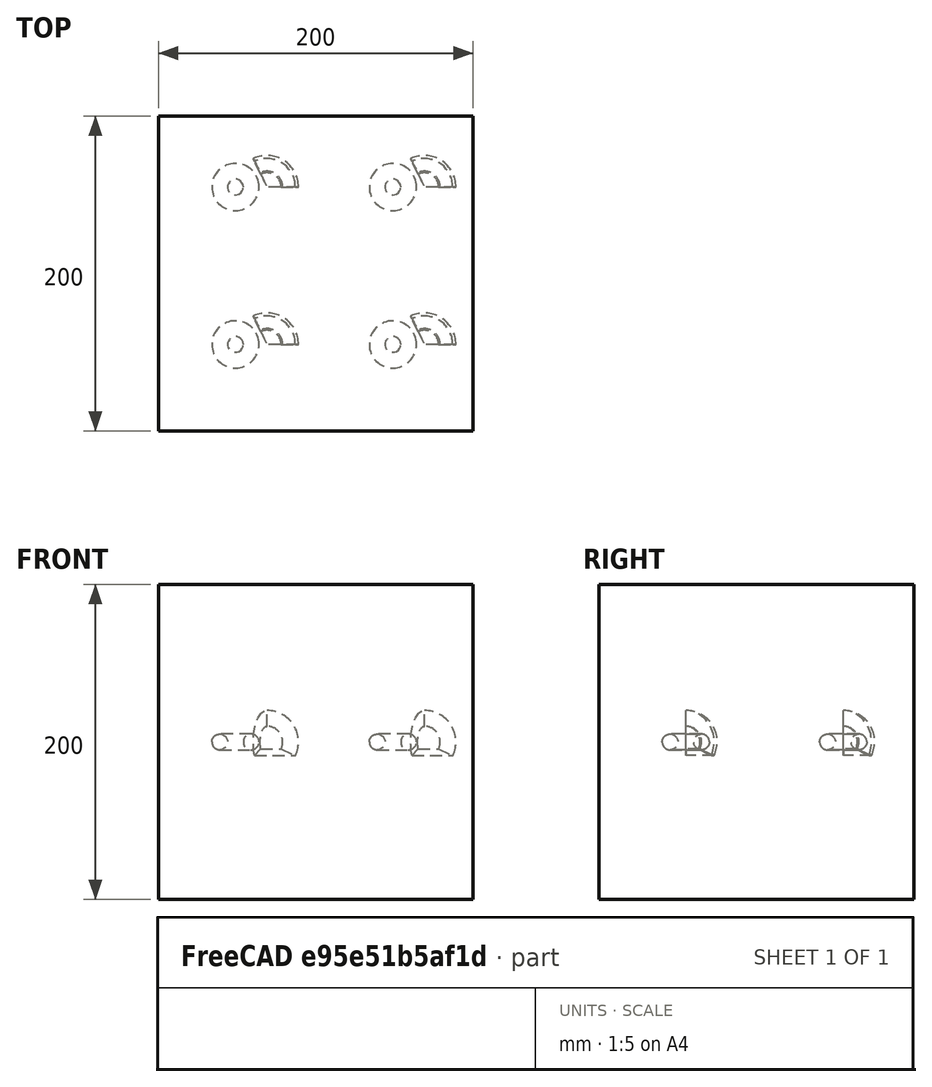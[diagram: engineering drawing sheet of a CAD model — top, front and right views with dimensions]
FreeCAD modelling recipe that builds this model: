
FCSTD DOCUMENT  (FreeCAD 0.19RUnknown)
Label: arrayTest-6
License: All rights reserved
LicenseURL: http://en.wikipedia.org/wiki/All_rights_reserved
objects: App::DocumentObjectGroupPython×1248, Part::FeaturePython×4, App::Part×2, Part::MultiFuse×1
note: 5 computed .brp shape members not serialized (recipe doc carries the construction recipe); baked Part::Feature solids carry a one-line shape summary decoded from their .brp

FEATURE [App::DocumentObjectGroupPython] HALFPI  # scripted group (container) (typed FeaturePython)
  name = HALFPI
  value = pi/2.
FEATURE [App::DocumentObjectGroupPython] PI  # scripted group (container) (typed FeaturePython)
  name = PI
  value = 1.*pi
FEATURE [App::DocumentObjectGroupPython] TWOPI  # scripted group (container) (typed FeaturePython)
  name = TWOPI
  value = 2.*pi
FEATURE [App::DocumentObjectGroupPython] Constants  # scripted group (container) (typed FeaturePython)
  Group = -> [HALFPI,PI,TWOPI]
FEATURE [App::DocumentObjectGroupPython] Variables  # scripted group (container) (typed FeaturePython)
FEATURE [App::DocumentObjectGroupPython] Quantities  # scripted group (container) (typed FeaturePython)
FEATURE [App::DocumentObjectGroupPython] Isotopes  # scripted group (container) (typed FeaturePython)
FEATURE [App::DocumentObjectGroupPython] Elements  # scripted group (container) (typed FeaturePython)
FEATURE [App::DocumentObjectGroupPython] G4Isotopes  # scripted group (container) (typed FeaturePython)
FEATURE [App::DocumentObjectGroupPython] H_element  # scripted group (container) (typed FeaturePython)
  Z = 1
  atom_value = 1.008
  formula = H
  name = H_element
FEATURE [App::DocumentObjectGroupPython] He_element  # scripted group (container) (typed FeaturePython)
  Z = 2
  atom_value = 4.0026
  formula = He
  name = He_element
FEATURE [App::DocumentObjectGroupPython] Li_element  # scripted group (container) (typed FeaturePython)
  Z = 3
  atom_value = 6.94
  formula = Li
  name = Li_element
FEATURE [App::DocumentObjectGroupPython] Be_element  # scripted group (container) (typed FeaturePython)
  Z = 4
  atom_value = 9.01218
  formula = Be
  name = Be_element
FEATURE [App::DocumentObjectGroupPython] B_element  # scripted group (container) (typed FeaturePython)
  Z = 5
  atom_value = 10.81
  formula = B
  name = B_element
FEATURE [App::DocumentObjectGroupPython] C_element  # scripted group (container) (typed FeaturePython)
  Z = 6
  atom_value = 12.011
  formula = C
  name = C_element
FEATURE [App::DocumentObjectGroupPython] N_element  # scripted group (container) (typed FeaturePython)
  Z = 7
  atom_value = 14.007
  formula = N
  name = N_element
FEATURE [App::DocumentObjectGroupPython] O_element  # scripted group (container) (typed FeaturePython)
  Z = 8
  atom_value = 15.999
  formula = O
  name = O_element
FEATURE [App::DocumentObjectGroupPython] F_element  # scripted group (container) (typed FeaturePython)
  Z = 9
  atom_value = 18.9984
  formula = F
  name = F_element
FEATURE [App::DocumentObjectGroupPython] Ne_element  # scripted group (container) (typed FeaturePython)
  Z = 10
  atom_value = 20.1797
  formula = Ne
  name = Ne_element
FEATURE [App::DocumentObjectGroupPython] Na_element  # scripted group (container) (typed FeaturePython)
  Z = 11
  atom_value = 22.9898
  formula = Na
  name = Na_element
FEATURE [App::DocumentObjectGroupPython] Mg_element  # scripted group (container) (typed FeaturePython)
  Z = 12
  atom_value = 24.305
  formula = Mg
  name = Mg_element
FEATURE [App::DocumentObjectGroupPython] Al_element  # scripted group (container) (typed FeaturePython)
  Z = 13
  atom_value = 26.9815
  formula = Al
  name = Al_element
FEATURE [App::DocumentObjectGroupPython] Si_element  # scripted group (container) (typed FeaturePython)
  Z = 14
  atom_value = 28.085
  formula = Si
  name = Si_element
FEATURE [App::DocumentObjectGroupPython] P_element  # scripted group (container) (typed FeaturePython)
  Z = 15
  atom_value = 30.9738
  formula = P
  name = P_element
FEATURE [App::DocumentObjectGroupPython] S_element  # scripted group (container) (typed FeaturePython)
  Z = 16
  atom_value = 32.06
  formula = S
  name = S_element
FEATURE [App::DocumentObjectGroupPython] Cl_element  # scripted group (container) (typed FeaturePython)
  Z = 17
  atom_value = 35.45
  formula = Cl
  name = Cl_element
FEATURE [App::DocumentObjectGroupPython] Ar_element  # scripted group (container) (typed FeaturePython)
  Z = 18
  atom_value = 39.95
  formula = Ar
  name = Ar_element
FEATURE [App::DocumentObjectGroupPython] K_element  # scripted group (container) (typed FeaturePython)
  Z = 19
  atom_value = 39.0983
  formula = K
  name = K_element
FEATURE [App::DocumentObjectGroupPython] Ca_element  # scripted group (container) (typed FeaturePython)
  Z = 20
  atom_value = 40.078
  formula = Ca
  name = Ca_element
FEATURE [App::DocumentObjectGroupPython] Sc_element  # scripted group (container) (typed FeaturePython)
  Z = 21
  atom_value = 44.9559
  formula = Sc
  name = Sc_element
FEATURE [App::DocumentObjectGroupPython] Ti_element  # scripted group (container) (typed FeaturePython)
  Z = 22
  atom_value = 47.867
  formula = Ti
  name = Ti_element
FEATURE [App::DocumentObjectGroupPython] V_element  # scripted group (container) (typed FeaturePython)
  Z = 23
  atom_value = 50.9415
  formula = V
  name = V_element
FEATURE [App::DocumentObjectGroupPython] Cr_element  # scripted group (container) (typed FeaturePython)
  Z = 24
  atom_value = 51.9961
  formula = Cr
  name = Cr_element
FEATURE [App::DocumentObjectGroupPython] Mn_element  # scripted group (container) (typed FeaturePython)
  Z = 25
  atom_value = 54.938
  formula = Mn
  name = Mn_element
FEATURE [App::DocumentObjectGroupPython] Fe_element  # scripted group (container) (typed FeaturePython)
  Z = 26
  atom_value = 55.845
  formula = Fe
  name = Fe_element
FEATURE [App::DocumentObjectGroupPython] Co_element  # scripted group (container) (typed FeaturePython)
  Z = 27
  atom_value = 58.9332
  formula = Co
  name = Co_element
FEATURE [App::DocumentObjectGroupPython] Ni_element  # scripted group (container) (typed FeaturePython)
  Z = 28
  atom_value = 58.6934
  formula = Ni
  name = Ni_element
FEATURE [App::DocumentObjectGroupPython] Cu_element  # scripted group (container) (typed FeaturePython)
  Z = 29
  atom_value = 63.546
  formula = Cu
  name = Cu_element
FEATURE [App::DocumentObjectGroupPython] Zn_element  # scripted group (container) (typed FeaturePython)
  Z = 30
  atom_value = 65.38
  formula = Zn
  name = Zn_element
FEATURE [App::DocumentObjectGroupPython] Ga_element  # scripted group (container) (typed FeaturePython)
  Z = 31
  atom_value = 69.723
  formula = Ga
  name = Ga_element
FEATURE [App::DocumentObjectGroupPython] Ge_element  # scripted group (container) (typed FeaturePython)
  Z = 32
  atom_value = 72.63
  formula = Ge
  name = Ge_element
FEATURE [App::DocumentObjectGroupPython] As_element  # scripted group (container) (typed FeaturePython)
  Z = 33
  atom_value = 74.9216
  formula = As
  name = As_element
FEATURE [App::DocumentObjectGroupPython] Se_element  # scripted group (container) (typed FeaturePython)
  Z = 34
  atom_value = 78.971
  formula = Se
  name = Se_element
FEATURE [App::DocumentObjectGroupPython] Br_element  # scripted group (container) (typed FeaturePython)
  Z = 35
  atom_value = 79.904
  formula = Br
  name = Br_element
FEATURE [App::DocumentObjectGroupPython] Kr_element  # scripted group (container) (typed FeaturePython)
  Z = 36
  atom_value = 83.798
  formula = Kr
  name = Kr_element
FEATURE [App::DocumentObjectGroupPython] Rb_element  # scripted group (container) (typed FeaturePython)
  Z = 37
  atom_value = 85.4678
  formula = Rb
  name = Rb_element
FEATURE [App::DocumentObjectGroupPython] Sr_element  # scripted group (container) (typed FeaturePython)
  Z = 38
  atom_value = 87.62
  formula = Sr
  name = Sr_element
FEATURE [App::DocumentObjectGroupPython] Y_element  # scripted group (container) (typed FeaturePython)
  Z = 39
  atom_value = 88.9058
  formula = Y
  name = Y_element
FEATURE [App::DocumentObjectGroupPython] Zr_element  # scripted group (container) (typed FeaturePython)
  Z = 40
  atom_value = 91.224
  formula = Zr
  name = Zr_element
FEATURE [App::DocumentObjectGroupPython] Nb_element  # scripted group (container) (typed FeaturePython)
  Z = 41
  atom_value = 92.9064
  formula = Nb
  name = Nb_element
FEATURE [App::DocumentObjectGroupPython] Mo_element  # scripted group (container) (typed FeaturePython)
  Z = 42
  atom_value = 95.95
  formula = Mo
  name = Mo_element
FEATURE [App::DocumentObjectGroupPython] Tc_element  # scripted group (container) (typed FeaturePython)
  Z = 43
  atom_value = 97
  formula = Tc
  name = Tc_element
FEATURE [App::DocumentObjectGroupPython] Ru_element  # scripted group (container) (typed FeaturePython)
  Z = 44
  atom_value = 101.07
  formula = Ru
  name = Ru_element
FEATURE [App::DocumentObjectGroupPython] Rh_element  # scripted group (container) (typed FeaturePython)
  Z = 45
  atom_value = 102.905
  formula = Rh
  name = Rh_element
FEATURE [App::DocumentObjectGroupPython] Pd_element  # scripted group (container) (typed FeaturePython)
  Z = 46
  atom_value = 106.42
  formula = Pd
  name = Pd_element
FEATURE [App::DocumentObjectGroupPython] Ag_element  # scripted group (container) (typed FeaturePython)
  Z = 47
  atom_value = 107.868
  formula = Ag
  name = Ag_element
FEATURE [App::DocumentObjectGroupPython] Cd_element  # scripted group (container) (typed FeaturePython)
  Z = 48
  atom_value = 112.414
  formula = Cd
  name = Cd_element
FEATURE [App::DocumentObjectGroupPython] In_element  # scripted group (container) (typed FeaturePython)
  Z = 49
  atom_value = 114.818
  formula = In
  name = In_element
FEATURE [App::DocumentObjectGroupPython] Sn_element  # scripted group (container) (typed FeaturePython)
  Z = 50
  atom_value = 118.71
  formula = Sn
  name = Sn_element
FEATURE [App::DocumentObjectGroupPython] Sb_element  # scripted group (container) (typed FeaturePython)
  Z = 51
  atom_value = 121.76
  formula = Sb
  name = Sb_element
FEATURE [App::DocumentObjectGroupPython] Te_element  # scripted group (container) (typed FeaturePython)
  Z = 52
  atom_value = 127.6
  formula = Te
  name = Te_element
FEATURE [App::DocumentObjectGroupPython] I_element  # scripted group (container) (typed FeaturePython)
  Z = 53
  atom_value = 126.904
  formula = I
  name = I_element
FEATURE [App::DocumentObjectGroupPython] Xe_element  # scripted group (container) (typed FeaturePython)
  Z = 54
  atom_value = 131.293
  formula = Xe
  name = Xe_element
FEATURE [App::DocumentObjectGroupPython] Cs_element  # scripted group (container) (typed FeaturePython)
  Z = 55
  atom_value = 132.905
  formula = Cs
  name = Cs_element
FEATURE [App::DocumentObjectGroupPython] Ba_element  # scripted group (container) (typed FeaturePython)
  Z = 56
  atom_value = 137.327
  formula = Ba
  name = Ba_element
FEATURE [App::DocumentObjectGroupPython] La_element  # scripted group (container) (typed FeaturePython)
  Z = 57
  atom_value = 138.905
  formula = La
  name = La_element
FEATURE [App::DocumentObjectGroupPython] Ce_element  # scripted group (container) (typed FeaturePython)
  Z = 58
  atom_value = 140.116
  formula = Ce
  name = Ce_element
FEATURE [App::DocumentObjectGroupPython] Pr_element  # scripted group (container) (typed FeaturePython)
  Z = 59
  atom_value = 140.908
  formula = Pr
  name = Pr_element
FEATURE [App::DocumentObjectGroupPython] Nd_element  # scripted group (container) (typed FeaturePython)
  Z = 60
  atom_value = 144.242
  formula = Nd
  name = Nd_element
FEATURE [App::DocumentObjectGroupPython] Pm_element  # scripted group (container) (typed FeaturePython)
  Z = 61
  atom_value = 145
  formula = Pm
  name = Pm_element
FEATURE [App::DocumentObjectGroupPython] Sm_element  # scripted group (container) (typed FeaturePython)
  Z = 62
  atom_value = 150.36
  formula = Sm
  name = Sm_element
FEATURE [App::DocumentObjectGroupPython] Eu_element  # scripted group (container) (typed FeaturePython)
  Z = 63
  atom_value = 151.964
  formula = Eu
  name = Eu_element
FEATURE [App::DocumentObjectGroupPython] Gd_element  # scripted group (container) (typed FeaturePython)
  Z = 64
  atom_value = 157.25
  formula = Gd
  name = Gd_element
FEATURE [App::DocumentObjectGroupPython] Tb_element  # scripted group (container) (typed FeaturePython)
  Z = 65
  atom_value = 158.925
  formula = Tb
  name = Tb_element
FEATURE [App::DocumentObjectGroupPython] Dy_element  # scripted group (container) (typed FeaturePython)
  Z = 66
  atom_value = 162.5
  formula = Dy
  name = Dy_element
FEATURE [App::DocumentObjectGroupPython] Ho_element  # scripted group (container) (typed FeaturePython)
  Z = 67
  atom_value = 164.93
  formula = Ho
  name = Ho_element
FEATURE [App::DocumentObjectGroupPython] Er_element  # scripted group (container) (typed FeaturePython)
  Z = 68
  atom_value = 167.259
  formula = Er
  name = Er_element
FEATURE [App::DocumentObjectGroupPython] Tm_element  # scripted group (container) (typed FeaturePython)
  Z = 69
  atom_value = 168.934
  formula = Tm
  name = Tm_element
FEATURE [App::DocumentObjectGroupPython] Yb_element  # scripted group (container) (typed FeaturePython)
  Z = 70
  atom_value = 173.045
  formula = Yb
  name = Yb_element
FEATURE [App::DocumentObjectGroupPython] Lu_element  # scripted group (container) (typed FeaturePython)
  Z = 71
  atom_value = 174.967
  formula = Lu
  name = Lu_element
FEATURE [App::DocumentObjectGroupPython] Hf_element  # scripted group (container) (typed FeaturePython)
  Z = 72
  atom_value = 178.49
  formula = Hf
  name = Hf_element
FEATURE [App::DocumentObjectGroupPython] Ta_element  # scripted group (container) (typed FeaturePython)
  Z = 73
  atom_value = 180.948
  formula = Ta
  name = Ta_element
FEATURE [App::DocumentObjectGroupPython] W_element  # scripted group (container) (typed FeaturePython)
  Z = 74
  atom_value = 183.84
  formula = W
  name = W_element
FEATURE [App::DocumentObjectGroupPython] Re_element  # scripted group (container) (typed FeaturePython)
  Z = 75
  atom_value = 186.207
  formula = Re
  name = Re_element
FEATURE [App::DocumentObjectGroupPython] Os_element  # scripted group (container) (typed FeaturePython)
  Z = 76
  atom_value = 190.23
  formula = Os
  name = Os_element
FEATURE [App::DocumentObjectGroupPython] Ir_element  # scripted group (container) (typed FeaturePython)
  Z = 77
  atom_value = 192.217
  formula = Ir
  name = Ir_element
FEATURE [App::DocumentObjectGroupPython] Pt_element  # scripted group (container) (typed FeaturePython)
  Z = 78
  atom_value = 195.084
  formula = Pt
  name = Pt_element
FEATURE [App::DocumentObjectGroupPython] Au_element  # scripted group (container) (typed FeaturePython)
  Z = 79
  atom_value = 196.967
  formula = Au
  name = Au_element
FEATURE [App::DocumentObjectGroupPython] Hg_element  # scripted group (container) (typed FeaturePython)
  Z = 80
  atom_value = 200.592
  formula = Hg
  name = Hg_element
FEATURE [App::DocumentObjectGroupPython] Tl_element  # scripted group (container) (typed FeaturePython)
  Z = 81
  atom_value = 204.38
  formula = Tl
  name = Tl_element
FEATURE [App::DocumentObjectGroupPython] Pb_element  # scripted group (container) (typed FeaturePython)
  Z = 82
  atom_value = 207.2
  formula = Pb
  name = Pb_element
FEATURE [App::DocumentObjectGroupPython] Bi_element  # scripted group (container) (typed FeaturePython)
  Z = 83
  atom_value = 208.98
  formula = Bi
  name = Bi_element
FEATURE [App::DocumentObjectGroupPython] Po_element  # scripted group (container) (typed FeaturePython)
  Z = 84
  atom_value = 209
  formula = Po
  name = Po_element
FEATURE [App::DocumentObjectGroupPython] At_element  # scripted group (container) (typed FeaturePython)
  Z = 85
  atom_value = 210
  formula = At
  name = At_element
FEATURE [App::DocumentObjectGroupPython] Rn_element  # scripted group (container) (typed FeaturePython)
  Z = 86
  atom_value = 222
  formula = Rn
  name = Rn_element
FEATURE [App::DocumentObjectGroupPython] Fr_element  # scripted group (container) (typed FeaturePython)
  Z = 87
  atom_value = 223
  formula = Fr
  name = Fr_element
FEATURE [App::DocumentObjectGroupPython] Ra_element  # scripted group (container) (typed FeaturePython)
  Z = 88
  atom_value = 226
  formula = Ra
  name = Ra_element
FEATURE [App::DocumentObjectGroupPython] Ac_element  # scripted group (container) (typed FeaturePython)
  Z = 89
  atom_value = 227
  formula = Ac
  name = Ac_element
FEATURE [App::DocumentObjectGroupPython] Th_element  # scripted group (container) (typed FeaturePython)
  Z = 90
  atom_value = 232.038
  formula = Th
  name = Th_element
FEATURE [App::DocumentObjectGroupPython] Pa_element  # scripted group (container) (typed FeaturePython)
  Z = 91
  atom_value = 231.036
  formula = Pa
  name = Pa_element
FEATURE [App::DocumentObjectGroupPython] U_element  # scripted group (container) (typed FeaturePython)
  Z = 92
  atom_value = 238.029
  formula = U
  name = U_element
FEATURE [App::DocumentObjectGroupPython] Np_element  # scripted group (container) (typed FeaturePython)
  Z = 93
  atom_value = 237
  formula = Np
  name = Np_element
FEATURE [App::DocumentObjectGroupPython] Pu_element  # scripted group (container) (typed FeaturePython)
  Z = 94
  atom_value = 244
  formula = Pu
  name = Pu_element
FEATURE [App::DocumentObjectGroupPython] Am_element  # scripted group (container) (typed FeaturePython)
  Z = 95
  atom_value = 243
  formula = Am
  name = Am_element
FEATURE [App::DocumentObjectGroupPython] Cm_element  # scripted group (container) (typed FeaturePython)
  Z = 96
  atom_value = 247
  formula = Cm
  name = Cm_element
FEATURE [App::DocumentObjectGroupPython] Bk_element  # scripted group (container) (typed FeaturePython)
  Z = 97
  atom_value = 247
  formula = Bk
  name = Bk_element
FEATURE [App::DocumentObjectGroupPython] Cf_element  # scripted group (container) (typed FeaturePython)
  Z = 98
  atom_value = 251
  formula = Cf
  name = Cf_element
FEATURE [App::DocumentObjectGroupPython] G4Elements  # scripted group (container) (typed FeaturePython)
  Group = -> [H_element,He_element,Li_element,Be_element,B_element,C_element,N_element,O_element,F_element,Ne_element,Na_element,Mg_element,Al_element,Si_element,P_element,S_element,Cl_element,Ar_element,K_element,Ca_element,Sc_element,Ti_element,V_element,Cr_element,Mn_element,Fe_element,Co_element,Ni_element,Cu_element,Zn_element,Ga_element,Ge_element,As_element,Se_element,Br_element,Kr_element,Rb_element,+61 more]
FEATURE [App::DocumentObjectGroupPython] H_element001  label="H_element : 0.101"  # scripted group (container) (typed FeaturePython)
  n = 0.101327
FEATURE [App::DocumentObjectGroupPython] C_element001  label="C_element : 0.775"  # scripted group (container) (typed FeaturePython)
  n = 0.7755
FEATURE [App::DocumentObjectGroupPython] N_element001  label="N_element : 0.035"  # scripted group (container) (typed FeaturePython)
  n = 0.035057
FEATURE [App::DocumentObjectGroupPython] O_element001  label="O_element : 0.052"  # scripted group (container) (typed FeaturePython)
  n = 0.0523159
FEATURE [App::DocumentObjectGroupPython] F_element001  label="F_element : 0.017"  # scripted group (container) (typed FeaturePython)
  n = 0.017422
FEATURE [App::DocumentObjectGroupPython] Ca_element001  label="Ca_element : 0.018"  # scripted group (container) (typed FeaturePython)
  n = 0.018378
FEATURE [App::DocumentObjectGroupPython] G4_A_150_TISSUE  label="G4_A-150_TISSUE"  # scripted group (container) (typed FeaturePython)
  Dunit = g/cm3
  Dvalue = 1.127
  Group = -> [H_element001,C_element001,N_element001,O_element001,F_element001,Ca_element001]
  conduct = 2
  density = 1
  expand = 3
  formula = G4_A-150_TISSUE
  name = G4_A-150_TISSUE
  specific = 4
FEATURE [App::DocumentObjectGroupPython] C_element002  label="C_element : 3"  # scripted group (container) (typed FeaturePython)
  n = 3
  ref = C_element
FEATURE [App::DocumentObjectGroupPython] H_element002  label="H_element : 6"  # scripted group (container) (typed FeaturePython)
  n = 6
  ref = H_element
FEATURE [App::DocumentObjectGroupPython] O_element002  label="O_element : 1"  # scripted group (container) (typed FeaturePython)
  n = 1
  ref = O_element
FEATURE [App::DocumentObjectGroupPython] G4_ACETONE  # scripted group (container) (typed FeaturePython)
  Dunit = g/cm3
  Dvalue = 0.7899
  Group = -> [C_element002,H_element002,O_element002]
  conduct = 2
  density = 1
  expand = 3
  formula = G4_ACETONE
  name = G4_ACETONE
  specific = 4
FEATURE [App::DocumentObjectGroupPython] C_element003  label="C_element : 2"  # scripted group (container) (typed FeaturePython)
  n = 2
  ref = C_element
FEATURE [App::DocumentObjectGroupPython] H_element003  label="H_element : 2"  # scripted group (container) (typed FeaturePython)
  n = 2
  ref = H_element
FEATURE [App::DocumentObjectGroupPython] G4_ACETYLENE  # scripted group (container) (typed FeaturePython)
  Dunit = g/cm3
  Dvalue = 0.0010967
  Group = -> [C_element003,H_element003]
  conduct = 2
  density = 1
  expand = 3
  formula = G4_ACETYLENE
  name = G4_ACETYLENE
  specific = 4
FEATURE [App::DocumentObjectGroupPython] C_element004  label="C_element : 5"  # scripted group (container) (typed FeaturePython)
  n = 5
  ref = C_element
FEATURE [App::DocumentObjectGroupPython] H_element004  label="H_element : 5"  # scripted group (container) (typed FeaturePython)
  n = 5
  ref = H_element
FEATURE [App::DocumentObjectGroupPython] N_element002  label="N_element : 5"  # scripted group (container) (typed FeaturePython)
  n = 5
  ref = N_element
FEATURE [App::DocumentObjectGroupPython] G4_ADENINE  # scripted group (container) (typed FeaturePython)
  Dunit = g/cm3
  Dvalue = 1.6
  Group = -> [C_element004,H_element004,N_element002]
  conduct = 2
  density = 1
  expand = 3
  formula = G4_ADENINE
  name = G4_ADENINE
  specific = 4
FEATURE [App::DocumentObjectGroupPython] H_element005  label="H_element : 0.114"  # scripted group (container) (typed FeaturePython)
  n = 0.114
FEATURE [App::DocumentObjectGroupPython] C_element005  label="C_element : 0.598"  # scripted group (container) (typed FeaturePython)
  n = 0.598
FEATURE [App::DocumentObjectGroupPython] N_element003  label="N_element : 0.007"  # scripted group (container) (typed FeaturePython)
  n = 0.007
FEATURE [App::DocumentObjectGroupPython] O_element003  label="O_element : 0.278"  # scripted group (container) (typed FeaturePython)
  n = 0.278
FEATURE [App::DocumentObjectGroupPython] Na_element001  label="Na_element : 0.001"  # scripted group (container) (typed FeaturePython)
  n = 0.001
FEATURE [App::DocumentObjectGroupPython] S_element001  label="S_element : 0.001"  # scripted group (container) (typed FeaturePython)
  n = 0.001
FEATURE [App::DocumentObjectGroupPython] Cl_element001  label="Cl_element : 0.001"  # scripted group (container) (typed FeaturePython)
  n = 0.001
FEATURE [App::DocumentObjectGroupPython] G4_ADIPOSE_TISSUE_ICRP  # scripted group (container) (typed FeaturePython)
  Dunit = g/cm3
  Dvalue = 0.95
  Group = -> [H_element005,C_element005,N_element003,O_element003,Na_element001,S_element001,Cl_element001]
  conduct = 2
  density = 1
  expand = 3
  formula = G4_ADIPOSE_TISSUE_ICRP
  name = G4_ADIPOSE_TISSUE_ICRP
  specific = 4
FEATURE [App::DocumentObjectGroupPython] C_element006  label="C_element : 0.000"  # scripted group (container) (typed FeaturePython)
  n = 0.000124
FEATURE [App::DocumentObjectGroupPython] N_element004  label="N_element : 0.755"  # scripted group (container) (typed FeaturePython)
  n = 0.755268
FEATURE [App::DocumentObjectGroupPython] O_element004  label="O_element : 0.232"  # scripted group (container) (typed FeaturePython)
  n = 0.231781
FEATURE [App::DocumentObjectGroupPython] Ar_element001  label="Ar_element : 0.013"  # scripted group (container) (typed FeaturePython)
  n = 0.012827
FEATURE [App::DocumentObjectGroupPython] G4_AIR  # scripted group (container) (typed FeaturePython)
  Dunit = g/cm3
  Dvalue = 0.00120479
  Group = -> [C_element006,N_element004,O_element004,Ar_element001]
  conduct = 2
  density = 1
  expand = 3
  formula = G4_AIR
  name = G4_AIR
  specific = 4
FEATURE [App::DocumentObjectGroupPython] C_element007  label="C_element : 006"  # scripted group (container) (typed FeaturePython)
  n = 3
  ref = C_element
FEATURE [App::DocumentObjectGroupPython] H_element006  label="H_element : 7"  # scripted group (container) (typed FeaturePython)
  n = 7
  ref = H_element
FEATURE [App::DocumentObjectGroupPython] N_element005  label="N_element : 1"  # scripted group (container) (typed FeaturePython)
  n = 1
  ref = N_element
FEATURE [App::DocumentObjectGroupPython] O_element005  label="O_element : 2"  # scripted group (container) (typed FeaturePython)
  n = 2
  ref = O_element
FEATURE [App::DocumentObjectGroupPython] G4_ALANINE  # scripted group (container) (typed FeaturePython)
  Dunit = g/cm3
  Dvalue = 1.42
  Group = -> [C_element007,H_element006,N_element005,O_element005]
  conduct = 2
  density = 1
  expand = 3
  formula = G4_ALANINE
  name = G4_ALANINE
  specific = 4
FEATURE [App::DocumentObjectGroupPython] Al_element001  label="Al_element : 2"  # scripted group (container) (typed FeaturePython)
  n = 2
  ref = Al_element
FEATURE [App::DocumentObjectGroupPython] O_element006  label="O_element : 3"  # scripted group (container) (typed FeaturePython)
  n = 3
  ref = O_element
FEATURE [App::DocumentObjectGroupPython] G4_ALUMINUM_OXIDE  # scripted group (container) (typed FeaturePython)
  Dunit = g/cm3
  Dvalue = 3.97
  Group = -> [Al_element001,O_element006]
  conduct = 2
  density = 1
  expand = 3
  formula = G4_ALUMINUM_OXIDE
  name = G4_ALUMINUM_OXIDE
  specific = 4
FEATURE [App::DocumentObjectGroupPython] H_element007  label="H_element : 0.106"  # scripted group (container) (typed FeaturePython)
  n = 0.10593
FEATURE [App::DocumentObjectGroupPython] C_element008  label="C_element : 0.789"  # scripted group (container) (typed FeaturePython)
  n = 0.788974
FEATURE [App::DocumentObjectGroupPython] O_element007  label="O_element : 0.105"  # scripted group (container) (typed FeaturePython)
  n = 0.105096
FEATURE [App::DocumentObjectGroupPython] G4_AMBER  # scripted group (container) (typed FeaturePython)
  Dunit = g/cm3
  Dvalue = 1.1
  Group = -> [H_element007,C_element008,O_element007]
  conduct = 2
  density = 1
  expand = 3
  formula = G4_AMBER
  name = G4_AMBER
  specific = 4
FEATURE [App::DocumentObjectGroupPython] N_element006  label="N_element : 006"  # scripted group (container) (typed FeaturePython)
  n = 1
  ref = N_element
FEATURE [App::DocumentObjectGroupPython] H_element008  label="H_element : 3"  # scripted group (container) (typed FeaturePython)
  n = 3
  ref = H_element
FEATURE [App::DocumentObjectGroupPython] G4_AMMONIA  # scripted group (container) (typed FeaturePython)
  Dunit = g/cm3
  Dvalue = 0.000826019
  Group = -> [N_element006,H_element008]
  conduct = 2
  density = 1
  expand = 3
  formula = G4_AMMONIA
  name = G4_AMMONIA
  specific = 4
FEATURE [App::DocumentObjectGroupPython] C_element009  label="C_element : 6"  # scripted group (container) (typed FeaturePython)
  n = 6
  ref = C_element
FEATURE [App::DocumentObjectGroupPython] H_element009  label="H_element : 008"  # scripted group (container) (typed FeaturePython)
  n = 7
  ref = H_element
FEATURE [App::DocumentObjectGroupPython] N_element007  label="N_element : 007"  # scripted group (container) (typed FeaturePython)
  n = 1
  ref = N_element
FEATURE [App::DocumentObjectGroupPython] G4_ANILINE  # scripted group (container) (typed FeaturePython)
  Dunit = g/cm3
  Dvalue = 1.0235
  Group = -> [C_element009,H_element009,N_element007]
  conduct = 2
  density = 1
  expand = 3
  formula = G4_ANILINE
  name = G4_ANILINE
  specific = 4
FEATURE [App::DocumentObjectGroupPython] C_element010  label="C_element : 14"  # scripted group (container) (typed FeaturePython)
  n = 14
  ref = C_element
FEATURE [App::DocumentObjectGroupPython] H_element010  label="H_element : 10"  # scripted group (container) (typed FeaturePython)
  n = 10
  ref = H_element
FEATURE [App::DocumentObjectGroupPython] G4_ANTHRACENE  # scripted group (container) (typed FeaturePython)
  Dunit = g/cm3
  Dvalue = 1.283
  Group = -> [C_element010,H_element010]
  conduct = 2
  density = 1
  expand = 3
  formula = G4_ANTHRACENE
  name = G4_ANTHRACENE
  specific = 4
FEATURE [App::DocumentObjectGroupPython] H_element011  label="H_element : 0.065"  # scripted group (container) (typed FeaturePython)
  n = 0.0654709
FEATURE [App::DocumentObjectGroupPython] C_element011  label="C_element : 0.537"  # scripted group (container) (typed FeaturePython)
  n = 0.536944
FEATURE [App::DocumentObjectGroupPython] N_element008  label="N_element : 0.021"  # scripted group (container) (typed FeaturePython)
  n = 0.0215
FEATURE [App::DocumentObjectGroupPython] O_element008  label="O_element : 0.032"  # scripted group (container) (typed FeaturePython)
  n = 0.032085
FEATURE [App::DocumentObjectGroupPython] F_element002  label="F_element : 0.167"  # scripted group (container) (typed FeaturePython)
  n = 0.167411
FEATURE [App::DocumentObjectGroupPython] Ca_element002  label="Ca_element : 0.177"  # scripted group (container) (typed FeaturePython)
  n = 0.176589
FEATURE [App::DocumentObjectGroupPython] G4_B_100_BONE  label="G4_B-100_BONE"  # scripted group (container) (typed FeaturePython)
  Dunit = g/cm3
  Dvalue = 1.45
  Group = -> [H_element011,C_element011,N_element008,O_element008,F_element002,Ca_element002]
  conduct = 2
  density = 1
  expand = 3
  formula = G4_B-100_BONE
  name = G4_B-100_BONE
  specific = 4
FEATURE [App::DocumentObjectGroupPython] H_element012  label="H_element : 0.057"  # scripted group (container) (typed FeaturePython)
  n = 0.057441
FEATURE [App::DocumentObjectGroupPython] C_element012  label="C_element : 0.790"  # scripted group (container) (typed FeaturePython)
  n = 0.774591
FEATURE [App::DocumentObjectGroupPython] O_element009  label="O_element : 0.168"  # scripted group (container) (typed FeaturePython)
  n = 0.167968
FEATURE [App::DocumentObjectGroupPython] G4_BAKELITE  # scripted group (container) (typed FeaturePython)
  Dunit = g/cm3
  Dvalue = 1.25
  Group = -> [H_element012,C_element012,O_element009]
  conduct = 2
  density = 1
  expand = 3
  formula = G4_BAKELITE
  name = G4_BAKELITE
  specific = 4
FEATURE [App::DocumentObjectGroupPython] Ba_element001  label="Ba_element : 1"  # scripted group (container) (typed FeaturePython)
  n = 1
  ref = Ba_element
FEATURE [App::DocumentObjectGroupPython] F_element003  label="F_element : 2"  # scripted group (container) (typed FeaturePython)
  n = 2
  ref = F_element
FEATURE [App::DocumentObjectGroupPython] G4_BARIUM_FLUORIDE  # scripted group (container) (typed FeaturePython)
  Dunit = g/cm3
  Dvalue = 4.89
  Group = -> [Ba_element001,F_element003]
  conduct = 2
  density = 1
  expand = 3
  formula = G4_BARIUM_FLUORIDE
  name = G4_BARIUM_FLUORIDE
  specific = 4
FEATURE [App::DocumentObjectGroupPython] Ba_element002  label="Ba_element : 002"  # scripted group (container) (typed FeaturePython)
  n = 1
  ref = Ba_element
FEATURE [App::DocumentObjectGroupPython] S_element002  label="S_element : 1"  # scripted group (container) (typed FeaturePython)
  n = 1
  ref = S_element
FEATURE [App::DocumentObjectGroupPython] O_element010  label="O_element : 4"  # scripted group (container) (typed FeaturePython)
  n = 4
  ref = O_element
FEATURE [App::DocumentObjectGroupPython] G4_BARIUM_SULFATE  # scripted group (container) (typed FeaturePython)
  Dunit = g/cm3
  Dvalue = 4.5
  Group = -> [Ba_element002,S_element002,O_element010]
  conduct = 2
  density = 1
  expand = 3
  formula = G4_BARIUM_SULFATE
  name = G4_BARIUM_SULFATE
  specific = 4
FEATURE [App::DocumentObjectGroupPython] C_element013  label="C_element : 007"  # scripted group (container) (typed FeaturePython)
  n = 6
  ref = C_element
FEATURE [App::DocumentObjectGroupPython] H_element013  label="H_element : 009"  # scripted group (container) (typed FeaturePython)
  n = 6
  ref = H_element
FEATURE [App::DocumentObjectGroupPython] G4_BENZENE  # scripted group (container) (typed FeaturePython)
  Dunit = g/cm3
  Dvalue = 0.87865
  Group = -> [C_element013,H_element013]
  conduct = 2
  density = 1
  expand = 3
  formula = G4_BENZENE
  name = G4_BENZENE
  specific = 4
FEATURE [App::DocumentObjectGroupPython] Be_element001  label="Be_element : 1"  # scripted group (container) (typed FeaturePython)
  n = 1
  ref = Be_element
FEATURE [App::DocumentObjectGroupPython] O_element011  label="O_element : 005"  # scripted group (container) (typed FeaturePython)
  n = 1
  ref = O_element
FEATURE [App::DocumentObjectGroupPython] G4_BERYLLIUM_OXIDE  # scripted group (container) (typed FeaturePython)
  Dunit = g/cm3
  Dvalue = 3.01
  Group = -> [Be_element001,O_element011]
  conduct = 2
  density = 1
  expand = 3
  formula = G4_BERYLLIUM_OXIDE
  name = G4_BERYLLIUM_OXIDE
  specific = 4
FEATURE [App::DocumentObjectGroupPython] Bi_element001  label="Bi_element : 4"  # scripted group (container) (typed FeaturePython)
  n = 4
  ref = Bi_element
FEATURE [App::DocumentObjectGroupPython] Ge_element001  label="Ge_element : 3"  # scripted group (container) (typed FeaturePython)
  n = 3
  ref = Ge_element
FEATURE [App::DocumentObjectGroupPython] O_element012  label="O_element : 12"  # scripted group (container) (typed FeaturePython)
  n = 12
  ref = O_element
FEATURE [App::DocumentObjectGroupPython] G4_BGO  # scripted group (container) (typed FeaturePython)
  Dunit = g/cm3
  Dvalue = 7.13
  Group = -> [Bi_element001,Ge_element001,O_element012]
  conduct = 2
  density = 1
  expand = 3
  formula = G4_BGO
  name = G4_BGO
  specific = 4
FEATURE [App::DocumentObjectGroupPython] H_element014  label="H_element : 0.102"  # scripted group (container) (typed FeaturePython)
  n = 0.102
FEATURE [App::DocumentObjectGroupPython] C_element014  label="C_element : 0.110"  # scripted group (container) (typed FeaturePython)
  n = 0.11
FEATURE [App::DocumentObjectGroupPython] N_element009  label="N_element : 0.033"  # scripted group (container) (typed FeaturePython)
  n = 0.033
FEATURE [App::DocumentObjectGroupPython] O_element013  label="O_element : 0.745"  # scripted group (container) (typed FeaturePython)
  n = 0.745
FEATURE [App::DocumentObjectGroupPython] Na_element002  label="Na_element : 0.002"  # scripted group (container) (typed FeaturePython)
  n = 0.001
FEATURE [App::DocumentObjectGroupPython] P_element001  label="P_element : 0.001"  # scripted group (container) (typed FeaturePython)
  n = 0.001
FEATURE [App::DocumentObjectGroupPython] S_element003  label="S_element : 0.002"  # scripted group (container) (typed FeaturePython)
  n = 0.002
FEATURE [App::DocumentObjectGroupPython] Cl_element002  label="Cl_element : 0.003"  # scripted group (container) (typed FeaturePython)
  n = 0.003
FEATURE [App::DocumentObjectGroupPython] K_element001  label="K_element : 0.002"  # scripted group (container) (typed FeaturePython)
  n = 0.002
FEATURE [App::DocumentObjectGroupPython] Fe_element001  label="Fe_element : 0.001"  # scripted group (container) (typed FeaturePython)
  n = 0.001
FEATURE [App::DocumentObjectGroupPython] G4_BLOOD_ICRP  # scripted group (container) (typed FeaturePython)
  Dunit = g/cm3
  Dvalue = 1.06
  Group = -> [H_element014,C_element014,N_element009,O_element013,Na_element002,P_element001,S_element003,Cl_element002,K_element001,Fe_element001]
  conduct = 2
  density = 1
  expand = 3
  formula = G4_BLOOD_ICRP
  name = G4_BLOOD_ICRP
  specific = 4
FEATURE [App::DocumentObjectGroupPython] H_element015  label="H_element : 0.064"  # scripted group (container) (typed FeaturePython)
  n = 0.064
FEATURE [App::DocumentObjectGroupPython] C_element015  label="C_element : 0.278"  # scripted group (container) (typed FeaturePython)
  n = 0.278
FEATURE [App::DocumentObjectGroupPython] N_element010  label="N_element : 0.027"  # scripted group (container) (typed FeaturePython)
  n = 0.027
FEATURE [App::DocumentObjectGroupPython] O_element014  label="O_element : 0.410"  # scripted group (container) (typed FeaturePython)
  n = 0.41
FEATURE [App::DocumentObjectGroupPython] Mg_element001  label="Mg_element : 0.002"  # scripted group (container) (typed FeaturePython)
  n = 0.002
FEATURE [App::DocumentObjectGroupPython] P_element002  label="P_element : 0.070"  # scripted group (container) (typed FeaturePython)
  n = 0.07
FEATURE [App::DocumentObjectGroupPython] S_element004  label="S_element : 0.003"  # scripted group (container) (typed FeaturePython)
  n = 0.002
FEATURE [App::DocumentObjectGroupPython] Ca_element003  label="Ca_element : 0.147"  # scripted group (container) (typed FeaturePython)
  n = 0.147
FEATURE [App::DocumentObjectGroupPython] G4_BONE_COMPACT_ICRU  # scripted group (container) (typed FeaturePython)
  Dunit = g/cm3
  Dvalue = 1.85
  Group = -> [H_element015,C_element015,N_element010,O_element014,Mg_element001,P_element002,S_element004,Ca_element003]
  conduct = 2
  density = 1
  expand = 3
  formula = G4_BONE_COMPACT_ICRU
  name = G4_BONE_COMPACT_ICRU
  specific = 4
FEATURE [App::DocumentObjectGroupPython] H_element016  label="H_element : 0.034"  # scripted group (container) (typed FeaturePython)
  n = 0.034
FEATURE [App::DocumentObjectGroupPython] C_element016  label="C_element : 0.155"  # scripted group (container) (typed FeaturePython)
  n = 0.155
FEATURE [App::DocumentObjectGroupPython] N_element011  label="N_element : 0.042"  # scripted group (container) (typed FeaturePython)
  n = 0.042
FEATURE [App::DocumentObjectGroupPython] O_element015  label="O_element : 0.435"  # scripted group (container) (typed FeaturePython)
  n = 0.435
FEATURE [App::DocumentObjectGroupPython] Na_element003  label="Na_element : 0.003"  # scripted group (container) (typed FeaturePython)
  n = 0.001
FEATURE [App::DocumentObjectGroupPython] Mg_element002  label="Mg_element : 0.003"  # scripted group (container) (typed FeaturePython)
  n = 0.002
FEATURE [App::DocumentObjectGroupPython] P_element003  label="P_element : 0.103"  # scripted group (container) (typed FeaturePython)
  n = 0.103
FEATURE [App::DocumentObjectGroupPython] S_element005  label="S_element : 0.004"  # scripted group (container) (typed FeaturePython)
  n = 0.003
FEATURE [App::DocumentObjectGroupPython] Ca_element004  label="Ca_element : 0.225"  # scripted group (container) (typed FeaturePython)
  n = 0.225
FEATURE [App::DocumentObjectGroupPython] G4_BONE_CORTICAL_ICRP  # scripted group (container) (typed FeaturePython)
  Dunit = g/cm3
  Dvalue = 1.92
  Group = -> [H_element016,C_element016,N_element011,O_element015,Na_element003,Mg_element002,P_element003,S_element005,Ca_element004]
  conduct = 2
  density = 1
  expand = 3
  formula = G4_BONE_CORTICAL_ICRP
  name = G4_BONE_CORTICAL_ICRP
  specific = 4
FEATURE [App::DocumentObjectGroupPython] B_element001  label="B_element : 4"  # scripted group (container) (typed FeaturePython)
  n = 4
  ref = B_element
FEATURE [App::DocumentObjectGroupPython] C_element017  label="C_element : 1"  # scripted group (container) (typed FeaturePython)
  n = 1
  ref = C_element
FEATURE [App::DocumentObjectGroupPython] G4_BORON_CARBIDE  # scripted group (container) (typed FeaturePython)
  Dunit = g/cm3
  Dvalue = 2.52
  Group = -> [B_element001,C_element017]
  conduct = 2
  density = 1
  expand = 3
  formula = G4_BORON_CARBIDE
  name = G4_BORON_CARBIDE
  specific = 4
FEATURE [App::DocumentObjectGroupPython] B_element002  label="B_element : 2"  # scripted group (container) (typed FeaturePython)
  n = 2
  ref = B_element
FEATURE [App::DocumentObjectGroupPython] O_element016  label="O_element : 006"  # scripted group (container) (typed FeaturePython)
  n = 3
  ref = O_element
FEATURE [App::DocumentObjectGroupPython] G4_BORON_OXIDE  # scripted group (container) (typed FeaturePython)
  Dunit = g/cm3
  Dvalue = 1.812
  Group = -> [B_element002,O_element016]
  conduct = 2
  density = 1
  expand = 3
  formula = G4_BORON_OXIDE
  name = G4_BORON_OXIDE
  specific = 4
FEATURE [App::DocumentObjectGroupPython] H_element017  label="H_element : 0.107"  # scripted group (container) (typed FeaturePython)
  n = 0.107
FEATURE [App::DocumentObjectGroupPython] C_element018  label="C_element : 0.145"  # scripted group (container) (typed FeaturePython)
  n = 0.145
FEATURE [App::DocumentObjectGroupPython] N_element012  label="N_element : 0.022"  # scripted group (container) (typed FeaturePython)
  n = 0.022
FEATURE [App::DocumentObjectGroupPython] O_element017  label="O_element : 0.712"  # scripted group (container) (typed FeaturePython)
  n = 0.712
FEATURE [App::DocumentObjectGroupPython] Na_element004  label="Na_element : 0.004"  # scripted group (container) (typed FeaturePython)
  n = 0.002
FEATURE [App::DocumentObjectGroupPython] P_element004  label="P_element : 0.004"  # scripted group (container) (typed FeaturePython)
  n = 0.004
FEATURE [App::DocumentObjectGroupPython] S_element006  label="S_element : 0.005"  # scripted group (container) (typed FeaturePython)
  n = 0.002
FEATURE [App::DocumentObjectGroupPython] Cl_element003  label="Cl_element : 0.004"  # scripted group (container) (typed FeaturePython)
  n = 0.003
FEATURE [App::DocumentObjectGroupPython] K_element002  label="K_element : 0.003"  # scripted group (container) (typed FeaturePython)
  n = 0.003
FEATURE [App::DocumentObjectGroupPython] G4_BRAIN_ICRP  # scripted group (container) (typed FeaturePython)
  Dunit = g/cm3
  Dvalue = 1.04
  Group = -> [H_element017,C_element018,N_element012,O_element017,Na_element004,P_element004,S_element006,Cl_element003,K_element002]
  conduct = 2
  density = 1
  expand = 3
  formula = G4_BRAIN_ICRP
  name = G4_BRAIN_ICRP
  specific = 4
FEATURE [App::DocumentObjectGroupPython] C_element019  label="C_element : 4"  # scripted group (container) (typed FeaturePython)
  n = 4
  ref = C_element
FEATURE [App::DocumentObjectGroupPython] H_element018  label="H_element : 010"  # scripted group (container) (typed FeaturePython)
  n = 10
  ref = H_element
FEATURE [App::DocumentObjectGroupPython] G4_BUTANE  # scripted group (container) (typed FeaturePython)
  Dunit = g/cm3
  Dvalue = 0.00249343
  Group = -> [C_element019,H_element018]
  conduct = 2
  density = 1
  expand = 3
  formula = G4_BUTANE
  name = G4_BUTANE
  specific = 4
FEATURE [App::DocumentObjectGroupPython] C_element020  label="C_element : 008"  # scripted group (container) (typed FeaturePython)
  n = 4
  ref = C_element
FEATURE [App::DocumentObjectGroupPython] H_element019  label="H_element : 011"  # scripted group (container) (typed FeaturePython)
  n = 10
  ref = H_element
FEATURE [App::DocumentObjectGroupPython] O_element018  label="O_element : 007"  # scripted group (container) (typed FeaturePython)
  n = 1
  ref = O_element
FEATURE [App::DocumentObjectGroupPython] G4_N_BUTYL_ALCOHOL  label="G4_N-BUTYL_ALCOHOL"  # scripted group (container) (typed FeaturePython)
  Dunit = g/cm3
  Dvalue = 0.8098
  Group = -> [C_element020,H_element019,O_element018]
  conduct = 2
  density = 1
  expand = 3
  formula = G4_N-BUTYL_ALCOHOL
  name = G4_N-BUTYL_ALCOHOL
  specific = 4
FEATURE [App::DocumentObjectGroupPython] H_element020  label="H_element : 0.025"  # scripted group (container) (typed FeaturePython)
  n = 0.02468
FEATURE [App::DocumentObjectGroupPython] C_element021  label="C_element : 0.502"  # scripted group (container) (typed FeaturePython)
  n = 0.501611
FEATURE [App::DocumentObjectGroupPython] O_element019  label="O_element : 0.005"  # scripted group (container) (typed FeaturePython)
  n = 0.004527
FEATURE [App::DocumentObjectGroupPython] F_element004  label="F_element : 0.465"  # scripted group (container) (typed FeaturePython)
  n = 0.465209
FEATURE [App::DocumentObjectGroupPython] Si_element001  label="Si_element : 0.004"  # scripted group (container) (typed FeaturePython)
  n = 0.003973
FEATURE [App::DocumentObjectGroupPython] G4_C_552  label="G4_C-552"  # scripted group (container) (typed FeaturePython)
  Dunit = g/cm3
  Dvalue = 1.76
  Group = -> [H_element020,C_element021,O_element019,F_element004,Si_element001]
  conduct = 2
  density = 1
  expand = 3
  formula = G4_C-552
  name = G4_C-552
  specific = 4
FEATURE [App::DocumentObjectGroupPython] Cd_element001  label="Cd_element : 1"  # scripted group (container) (typed FeaturePython)
  n = 1
  ref = Cd_element
FEATURE [App::DocumentObjectGroupPython] Te_element001  label="Te_element : 1"  # scripted group (container) (typed FeaturePython)
  n = 1
  ref = Te_element
FEATURE [App::DocumentObjectGroupPython] G4_CADMIUM_TELLURIDE  # scripted group (container) (typed FeaturePython)
  Dunit = g/cm3
  Dvalue = 6.2
  Group = -> [Cd_element001,Te_element001]
  conduct = 2
  density = 1
  expand = 3
  formula = G4_CADMIUM_TELLURIDE
  name = G4_CADMIUM_TELLURIDE
  specific = 4
FEATURE [App::DocumentObjectGroupPython] Cd_element002  label="Cd_element : 002"  # scripted group (container) (typed FeaturePython)
  n = 1
  ref = Cd_element
FEATURE [App::DocumentObjectGroupPython] W_element001  label="W_element : 1"  # scripted group (container) (typed FeaturePython)
  n = 1
  ref = W_element
FEATURE [App::DocumentObjectGroupPython] O_element020  label="O_element : 008"  # scripted group (container) (typed FeaturePython)
  n = 4
  ref = O_element
FEATURE [App::DocumentObjectGroupPython] G4_CADMIUM_TUNGSTATE  # scripted group (container) (typed FeaturePython)
  Dunit = g/cm3
  Dvalue = 7.9
  Group = -> [Cd_element002,W_element001,O_element020]
  conduct = 2
  density = 1
  expand = 3
  formula = G4_CADMIUM_TUNGSTATE
  name = G4_CADMIUM_TUNGSTATE
  specific = 4
FEATURE [App::DocumentObjectGroupPython] Ca_element005  label="Ca_element : 1"  # scripted group (container) (typed FeaturePython)
  n = 1
  ref = Ca_element
FEATURE [App::DocumentObjectGroupPython] C_element022  label="C_element : 009"  # scripted group (container) (typed FeaturePython)
  n = 1
  ref = C_element
FEATURE [App::DocumentObjectGroupPython] O_element021  label="O_element : 009"  # scripted group (container) (typed FeaturePython)
  n = 3
  ref = O_element
FEATURE [App::DocumentObjectGroupPython] G4_CALCIUM_CARBONATE  # scripted group (container) (typed FeaturePython)
  Dunit = g/cm3
  Dvalue = 2.8
  Group = -> [Ca_element005,C_element022,O_element021]
  conduct = 2
  density = 1
  expand = 3
  formula = G4_CALCIUM_CARBONATE
  name = G4_CALCIUM_CARBONATE
  specific = 4
FEATURE [App::DocumentObjectGroupPython] Ca_element006  label="Ca_element : 002"  # scripted group (container) (typed FeaturePython)
  n = 1
  ref = Ca_element
FEATURE [App::DocumentObjectGroupPython] F_element005  label="F_element : 003"  # scripted group (container) (typed FeaturePython)
  n = 2
  ref = F_element
FEATURE [App::DocumentObjectGroupPython] G4_CALCIUM_FLUORIDE  # scripted group (container) (typed FeaturePython)
  Dunit = g/cm3
  Dvalue = 3.18
  Group = -> [Ca_element006,F_element005]
  conduct = 2
  density = 1
  expand = 3
  formula = G4_CALCIUM_FLUORIDE
  name = G4_CALCIUM_FLUORIDE
  specific = 4
FEATURE [App::DocumentObjectGroupPython] Ca_element007  label="Ca_element : 003"  # scripted group (container) (typed FeaturePython)
  n = 1
  ref = Ca_element
FEATURE [App::DocumentObjectGroupPython] O_element022  label="O_element : 010"  # scripted group (container) (typed FeaturePython)
  n = 1
  ref = O_element
FEATURE [App::DocumentObjectGroupPython] G4_CALCIUM_OXIDE  # scripted group (container) (typed FeaturePython)
  Dunit = g/cm3
  Dvalue = 3.3
  Group = -> [Ca_element007,O_element022]
  conduct = 2
  density = 1
  expand = 3
  formula = G4_CALCIUM_OXIDE
  name = G4_CALCIUM_OXIDE
  specific = 4
FEATURE [App::DocumentObjectGroupPython] Ca_element008  label="Ca_element : 004"  # scripted group (container) (typed FeaturePython)
  n = 1
  ref = Ca_element
FEATURE [App::DocumentObjectGroupPython] S_element007  label="S_element : 002"  # scripted group (container) (typed FeaturePython)
  n = 1
  ref = S_element
FEATURE [App::DocumentObjectGroupPython] O_element023  label="O_element : 011"  # scripted group (container) (typed FeaturePython)
  n = 4
  ref = O_element
FEATURE [App::DocumentObjectGroupPython] G4_CALCIUM_SULFATE  # scripted group (container) (typed FeaturePython)
  Dunit = g/cm3
  Dvalue = 2.96
  Group = -> [Ca_element008,S_element007,O_element023]
  conduct = 2
  density = 1
  expand = 3
  formula = G4_CALCIUM_SULFATE
  name = G4_CALCIUM_SULFATE
  specific = 4
FEATURE [App::DocumentObjectGroupPython] Ca_element009  label="Ca_element : 005"  # scripted group (container) (typed FeaturePython)
  n = 1
  ref = Ca_element
FEATURE [App::DocumentObjectGroupPython] W_element002  label="W_element : 002"  # scripted group (container) (typed FeaturePython)
  n = 1
  ref = W_element
FEATURE [App::DocumentObjectGroupPython] O_element024  label="O_element : 012"  # scripted group (container) (typed FeaturePython)
  n = 4
  ref = O_element
FEATURE [App::DocumentObjectGroupPython] G4_CALCIUM_TUNGSTATE  # scripted group (container) (typed FeaturePython)
  Dunit = g/cm3
  Dvalue = 6.062
  Group = -> [Ca_element009,W_element002,O_element024]
  conduct = 2
  density = 1
  expand = 3
  formula = G4_CALCIUM_TUNGSTATE
  name = G4_CALCIUM_TUNGSTATE
  specific = 4
FEATURE [App::DocumentObjectGroupPython] C_element023  label="C_element : 010"  # scripted group (container) (typed FeaturePython)
  n = 1
  ref = C_element
FEATURE [App::DocumentObjectGroupPython] O_element025  label="O_element : 013"  # scripted group (container) (typed FeaturePython)
  n = 2
  ref = O_element
FEATURE [App::DocumentObjectGroupPython] G4_CARBON_DIOXIDE  # scripted group (container) (typed FeaturePython)
  Dunit = g/cm3
  Dvalue = 0.00184212
  Group = -> [C_element023,O_element025]
  conduct = 2
  density = 1
  expand = 3
  formula = G4_CARBON_DIOXIDE
  name = G4_CARBON_DIOXIDE
  specific = 4
FEATURE [App::DocumentObjectGroupPython] C_element024  label="C_element : 011"  # scripted group (container) (typed FeaturePython)
  n = 1
  ref = C_element
FEATURE [App::DocumentObjectGroupPython] Cl_element004  label="Cl_element : 4"  # scripted group (container) (typed FeaturePython)
  n = 4
  ref = Cl_element
FEATURE [App::DocumentObjectGroupPython] G4_CARBON_TETRACHLORIDE  # scripted group (container) (typed FeaturePython)
  Dunit = g/cm3
  Dvalue = 1.594
  Group = -> [C_element024,Cl_element004]
  conduct = 2
  density = 1
  expand = 3
  formula = G4_CARBON_TETRACHLORIDE
  name = G4_CARBON_TETRACHLORIDE
  specific = 4
FEATURE [App::DocumentObjectGroupPython] C_element025  label="C_element : 012"  # scripted group (container) (typed FeaturePython)
  n = 6
  ref = C_element
FEATURE [App::DocumentObjectGroupPython] H_element021  label="H_element : 012"  # scripted group (container) (typed FeaturePython)
  n = 10
  ref = H_element
FEATURE [App::DocumentObjectGroupPython] O_element026  label="O_element : 5"  # scripted group (container) (typed FeaturePython)
  n = 5
  ref = O_element
FEATURE [App::DocumentObjectGroupPython] G4_CELLULOSE_CELLOPHANE  # scripted group (container) (typed FeaturePython)
  Dunit = g/cm3
  Dvalue = 1.42
  Group = -> [C_element025,H_element021,O_element026]
  conduct = 2
  density = 1
  expand = 3
  formula = G4_CELLULOSE_CELLOPHANE
  name = G4_CELLULOSE_CELLOPHANE
  specific = 4
FEATURE [App::DocumentObjectGroupPython] H_element022  label="H_element : 0.067"  # scripted group (container) (typed FeaturePython)
  n = 0.067125
FEATURE [App::DocumentObjectGroupPython] C_element026  label="C_element : 0.545"  # scripted group (container) (typed FeaturePython)
  n = 0.545403
FEATURE [App::DocumentObjectGroupPython] O_element027  label="O_element : 0.387"  # scripted group (container) (typed FeaturePython)
  n = 0.387472
FEATURE [App::DocumentObjectGroupPython] G4_CELLULOSE_BUTYRATE  # scripted group (container) (typed FeaturePython)
  Dunit = g/cm3
  Dvalue = 1.2
  Group = -> [H_element022,C_element026,O_element027]
  conduct = 2
  density = 1
  expand = 3
  formula = G4_CELLULOSE_BUTYRATE
  name = G4_CELLULOSE_BUTYRATE
  specific = 4
FEATURE [App::DocumentObjectGroupPython] H_element023  label="H_element : 0.029"  # scripted group (container) (typed FeaturePython)
  n = 0.029216
FEATURE [App::DocumentObjectGroupPython] C_element027  label="C_element : 0.271"  # scripted group (container) (typed FeaturePython)
  n = 0.271296
FEATURE [App::DocumentObjectGroupPython] N_element013  label="N_element : 0.121"  # scripted group (container) (typed FeaturePython)
  n = 0.121276
FEATURE [App::DocumentObjectGroupPython] O_element028  label="O_element : 0.578"  # scripted group (container) (typed FeaturePython)
  n = 0.578212
FEATURE [App::DocumentObjectGroupPython] G4_CELLULOSE_NITRATE  # scripted group (container) (typed FeaturePython)
  Dunit = g/cm3
  Dvalue = 1.49
  Group = -> [H_element023,C_element027,N_element013,O_element028]
  conduct = 2
  density = 1
  expand = 3
  formula = G4_CELLULOSE_NITRATE
  name = G4_CELLULOSE_NITRATE
  specific = 4
FEATURE [App::DocumentObjectGroupPython] H_element024  label="H_element : 0.108"  # scripted group (container) (typed FeaturePython)
  n = 0.107596
FEATURE [App::DocumentObjectGroupPython] N_element014  label="N_element : 0.001"  # scripted group (container) (typed FeaturePython)
  n = 0.0008
FEATURE [App::DocumentObjectGroupPython] O_element029  label="O_element : 0.875"  # scripted group (container) (typed FeaturePython)
  n = 0.874976
FEATURE [App::DocumentObjectGroupPython] S_element008  label="S_element : 0.015"  # scripted group (container) (typed FeaturePython)
  n = 0.014627
FEATURE [App::DocumentObjectGroupPython] Ce_element001  label="Ce_element : 0.002"  # scripted group (container) (typed FeaturePython)
  n = 0.002001
FEATURE [App::DocumentObjectGroupPython] G4_CERIC_SULFATE  # scripted group (container) (typed FeaturePython)
  Dunit = g/cm3
  Dvalue = 1.03
  Group = -> [H_element024,N_element014,O_element029,S_element008,Ce_element001]
  conduct = 2
  density = 1
  expand = 3
  formula = G4_CERIC_SULFATE
  name = G4_CERIC_SULFATE
  specific = 4
FEATURE [App::DocumentObjectGroupPython] Cs_element001  label="Cs_element : 1"  # scripted group (container) (typed FeaturePython)
  n = 1
  ref = Cs_element
FEATURE [App::DocumentObjectGroupPython] F_element006  label="F_element : 1"  # scripted group (container) (typed FeaturePython)
  n = 1
  ref = F_element
FEATURE [App::DocumentObjectGroupPython] G4_CESIUM_FLUORIDE  # scripted group (container) (typed FeaturePython)
  Dunit = g/cm3
  Dvalue = 4.115
  Group = -> [Cs_element001,F_element006]
  conduct = 2
  density = 1
  expand = 3
  formula = G4_CESIUM_FLUORIDE
  name = G4_CESIUM_FLUORIDE
  specific = 4
FEATURE [App::DocumentObjectGroupPython] Cs_element002  label="Cs_element : 002"  # scripted group (container) (typed FeaturePython)
  n = 1
  ref = Cs_element
FEATURE [App::DocumentObjectGroupPython] I_element001  label="I_element : 1"  # scripted group (container) (typed FeaturePython)
  n = 1
  ref = I_element
FEATURE [App::DocumentObjectGroupPython] G4_CESIUM_IODIDE  # scripted group (container) (typed FeaturePython)
  Dunit = g/cm3
  Dvalue = 4.51
  Group = -> [Cs_element002,I_element001]
  conduct = 2
  density = 1
  expand = 3
  formula = G4_CESIUM_IODIDE
  name = G4_CESIUM_IODIDE
  specific = 4
FEATURE [App::DocumentObjectGroupPython] C_element028  label="C_element : 013"  # scripted group (container) (typed FeaturePython)
  n = 6
  ref = C_element
FEATURE [App::DocumentObjectGroupPython] H_element025  label="H_element : 013"  # scripted group (container) (typed FeaturePython)
  n = 5
  ref = H_element
FEATURE [App::DocumentObjectGroupPython] Cl_element005  label="Cl_element : 1"  # scripted group (container) (typed FeaturePython)
  n = 1
  ref = Cl_element
FEATURE [App::DocumentObjectGroupPython] G4_CHLOROBENZENE  # scripted group (container) (typed FeaturePython)
  Dunit = g/cm3
  Dvalue = 1.1058
  Group = -> [C_element028,H_element025,Cl_element005]
  conduct = 2
  density = 1
  expand = 3
  formula = G4_CHLOROBENZENE
  name = G4_CHLOROBENZENE
  specific = 4
FEATURE [App::DocumentObjectGroupPython] C_element029  label="C_element : 014"  # scripted group (container) (typed FeaturePython)
  n = 1
  ref = C_element
FEATURE [App::DocumentObjectGroupPython] H_element026  label="H_element : 1"  # scripted group (container) (typed FeaturePython)
  n = 1
  ref = H_element
FEATURE [App::DocumentObjectGroupPython] Cl_element006  label="Cl_element : 3"  # scripted group (container) (typed FeaturePython)
  n = 3
  ref = Cl_element
FEATURE [App::DocumentObjectGroupPython] G4_CHLOROFORM  # scripted group (container) (typed FeaturePython)
  Dunit = g/cm3
  Dvalue = 1.4832
  Group = -> [C_element029,H_element026,Cl_element006]
  conduct = 2
  density = 1
  expand = 3
  formula = G4_CHLOROFORM
  name = G4_CHLOROFORM
  specific = 4
FEATURE [App::DocumentObjectGroupPython] H_element027  label="H_element : 0.010"  # scripted group (container) (typed FeaturePython)
  n = 0.01
FEATURE [App::DocumentObjectGroupPython] C_element030  label="C_element : 0.001"  # scripted group (container) (typed FeaturePython)
  n = 0.001
FEATURE [App::DocumentObjectGroupPython] O_element030  label="O_element : 0.529"  # scripted group (container) (typed FeaturePython)
  n = 0.529107
FEATURE [App::DocumentObjectGroupPython] Na_element005  label="Na_element : 0.016"  # scripted group (container) (typed FeaturePython)
  n = 0.016
FEATURE [App::DocumentObjectGroupPython] Mg_element003  label="Mg_element : 0.004"  # scripted group (container) (typed FeaturePython)
  n = 0.002
FEATURE [App::DocumentObjectGroupPython] Al_element002  label="Al_element : 0.034"  # scripted group (container) (typed FeaturePython)
  n = 0.033872
FEATURE [App::DocumentObjectGroupPython] Si_element002  label="Si_element : 0.337"  # scripted group (container) (typed FeaturePython)
  n = 0.337021
FEATURE [App::DocumentObjectGroupPython] K_element003  label="K_element : 0.013"  # scripted group (container) (typed FeaturePython)
  n = 0.013
FEATURE [App::DocumentObjectGroupPython] Ca_element010  label="Ca_element : 0.044"  # scripted group (container) (typed FeaturePython)
  n = 0.044
FEATURE [App::DocumentObjectGroupPython] Fe_element002  label="Fe_element : 0.014"  # scripted group (container) (typed FeaturePython)
  n = 0.014
FEATURE [App::DocumentObjectGroupPython] G4_CONCRETE  # scripted group (container) (typed FeaturePython)
  Dunit = g/cm3
  Dvalue = 2.3
  Group = -> [H_element027,C_element030,O_element030,Na_element005,Mg_element003,Al_element002,Si_element002,K_element003,Ca_element010,Fe_element002]
  conduct = 2
  density = 1
  expand = 3
  formula = G4_CONCRETE
  name = G4_CONCRETE
  specific = 4
FEATURE [App::DocumentObjectGroupPython] C_element031  label="C_element : 015"  # scripted group (container) (typed FeaturePython)
  n = 6
  ref = C_element
FEATURE [App::DocumentObjectGroupPython] H_element028  label="H_element : 12"  # scripted group (container) (typed FeaturePython)
  n = 12
  ref = H_element
FEATURE [App::DocumentObjectGroupPython] G4_CYCLOHEXANE  # scripted group (container) (typed FeaturePython)
  Dunit = g/cm3
  Dvalue = 0.779
  Group = -> [C_element031,H_element028]
  conduct = 2
  density = 1
  expand = 3
  formula = G4_CYCLOHEXANE
  name = G4_CYCLOHEXANE
  specific = 4
FEATURE [App::DocumentObjectGroupPython] C_element032  label="C_element : 016"  # scripted group (container) (typed FeaturePython)
  n = 6
  ref = C_element
FEATURE [App::DocumentObjectGroupPython] H_element029  label="H_element : 4"  # scripted group (container) (typed FeaturePython)
  n = 4
  ref = H_element
FEATURE [App::DocumentObjectGroupPython] Cl_element007  label="Cl_element : 2"  # scripted group (container) (typed FeaturePython)
  n = 2
  ref = Cl_element
FEATURE [App::DocumentObjectGroupPython] G4_1_2_DICHLOROBENZENE  label="G4_1.2-DICHLOROBENZENE"  # scripted group (container) (typed FeaturePython)
  Dunit = g/cm3
  Dvalue = 1.3048
  Group = -> [C_element032,H_element029,Cl_element007]
  conduct = 2
  density = 1
  expand = 3
  formula = G4_1.2-DICHLOROBENZENE
  name = G4_1.2-DICHLOROBENZENE
  specific = 4
FEATURE [App::DocumentObjectGroupPython] C_element033  label="C_element : 017"  # scripted group (container) (typed FeaturePython)
  n = 4
  ref = C_element
FEATURE [App::DocumentObjectGroupPython] H_element030  label="H_element : 8"  # scripted group (container) (typed FeaturePython)
  n = 8
  ref = H_element
FEATURE [App::DocumentObjectGroupPython] O_element031  label="O_element : 014"  # scripted group (container) (typed FeaturePython)
  n = 1
  ref = O_element
FEATURE [App::DocumentObjectGroupPython] Cl_element008  label="Cl_element : 005"  # scripted group (container) (typed FeaturePython)
  n = 2
  ref = Cl_element
FEATURE [App::DocumentObjectGroupPython] G4_DICHLORODIETHYL_ETHER  # scripted group (container) (typed FeaturePython)
  Dunit = g/cm3
  Dvalue = 1.2199
  Group = -> [C_element033,H_element030,O_element031,Cl_element008]
  conduct = 2
  density = 1
  expand = 3
  formula = G4_DICHLORODIETHYL_ETHER
  name = G4_DICHLORODIETHYL_ETHER
  specific = 4
FEATURE [App::DocumentObjectGroupPython] C_element034  label="C_element : 018"  # scripted group (container) (typed FeaturePython)
  n = 2
  ref = C_element
FEATURE [App::DocumentObjectGroupPython] H_element031  label="H_element : 014"  # scripted group (container) (typed FeaturePython)
  n = 4
  ref = H_element
FEATURE [App::DocumentObjectGroupPython] Cl_element009  label="Cl_element : 006"  # scripted group (container) (typed FeaturePython)
  n = 2
  ref = Cl_element
FEATURE [App::DocumentObjectGroupPython] G4_1_2_DICHLOROETHANE  label="G4_1.2-DICHLOROETHANE"  # scripted group (container) (typed FeaturePython)
  Dunit = g/cm3
  Dvalue = 1.2351
  Group = -> [C_element034,H_element031,Cl_element009]
  conduct = 2
  density = 1
  expand = 3
  formula = G4_1.2-DICHLOROETHANE
  name = G4_1.2-DICHLOROETHANE
  specific = 4
FEATURE [App::DocumentObjectGroupPython] C_element035  label="C_element : 019"  # scripted group (container) (typed FeaturePython)
  n = 4
  ref = C_element
FEATURE [App::DocumentObjectGroupPython] H_element032  label="H_element : 015"  # scripted group (container) (typed FeaturePython)
  n = 10
  ref = H_element
FEATURE [App::DocumentObjectGroupPython] O_element032  label="O_element : 015"  # scripted group (container) (typed FeaturePython)
  n = 1
  ref = O_element
FEATURE [App::DocumentObjectGroupPython] G4_DIETHYL_ETHER  # scripted group (container) (typed FeaturePython)
  Dunit = g/cm3
  Dvalue = 0.71378
  Group = -> [C_element035,H_element032,O_element032]
  conduct = 2
  density = 1
  expand = 3
  formula = G4_DIETHYL_ETHER
  name = G4_DIETHYL_ETHER
  specific = 4
FEATURE [App::DocumentObjectGroupPython] C_element036  label="C_element : 020"  # scripted group (container) (typed FeaturePython)
  n = 3
  ref = C_element
FEATURE [App::DocumentObjectGroupPython] H_element033  label="H_element : 016"  # scripted group (container) (typed FeaturePython)
  n = 7
  ref = H_element
FEATURE [App::DocumentObjectGroupPython] N_element015  label="N_element : 008"  # scripted group (container) (typed FeaturePython)
  n = 1
  ref = N_element
FEATURE [App::DocumentObjectGroupPython] O_element033  label="O_element : 016"  # scripted group (container) (typed FeaturePython)
  n = 1
  ref = O_element
FEATURE [App::DocumentObjectGroupPython] G4_N_N_DIMETHYL_FORMAMIDE  label="G4_N.N-DIMETHYL_FORMAMIDE"  # scripted group (container) (typed FeaturePython)
  Dunit = g/cm3
  Dvalue = 0.9487
  Group = -> [C_element036,H_element033,N_element015,O_element033]
  conduct = 2
  density = 1
  expand = 3
  formula = G4_N.N-DIMETHYL_FORMAMIDE
  name = G4_N.N-DIMETHYL_FORMAMIDE
  specific = 4
FEATURE [App::DocumentObjectGroupPython] C_element037  label="C_element : 021"  # scripted group (container) (typed FeaturePython)
  n = 2
  ref = C_element
FEATURE [App::DocumentObjectGroupPython] H_element034  label="H_element : 017"  # scripted group (container) (typed FeaturePython)
  n = 6
  ref = H_element
FEATURE [App::DocumentObjectGroupPython] O_element034  label="O_element : 017"  # scripted group (container) (typed FeaturePython)
  n = 1
  ref = O_element
FEATURE [App::DocumentObjectGroupPython] S_element009  label="S_element : 003"  # scripted group (container) (typed FeaturePython)
  n = 1
  ref = S_element
FEATURE [App::DocumentObjectGroupPython] G4_DIMETHYL_SULFOXIDE  # scripted group (container) (typed FeaturePython)
  Dunit = g/cm3
  Dvalue = 1.1014
  Group = -> [C_element037,H_element034,O_element034,S_element009]
  conduct = 2
  density = 1
  expand = 3
  formula = G4_DIMETHYL_SULFOXIDE
  name = G4_DIMETHYL_SULFOXIDE
  specific = 4
FEATURE [App::DocumentObjectGroupPython] C_element038  label="C_element : 022"  # scripted group (container) (typed FeaturePython)
  n = 2
  ref = C_element
FEATURE [App::DocumentObjectGroupPython] H_element035  label="H_element : 018"  # scripted group (container) (typed FeaturePython)
  n = 6
  ref = H_element
FEATURE [App::DocumentObjectGroupPython] G4_ETHANE  # scripted group (container) (typed FeaturePython)
  Dunit = g/cm3
  Dvalue = 0.00125324
  Group = -> [C_element038,H_element035]
  conduct = 2
  density = 1
  expand = 3
  formula = G4_ETHANE
  name = G4_ETHANE
  specific = 4
FEATURE [App::DocumentObjectGroupPython] C_element039  label="C_element : 023"  # scripted group (container) (typed FeaturePython)
  n = 2
  ref = C_element
FEATURE [App::DocumentObjectGroupPython] H_element036  label="H_element : 019"  # scripted group (container) (typed FeaturePython)
  n = 6
  ref = H_element
FEATURE [App::DocumentObjectGroupPython] O_element035  label="O_element : 018"  # scripted group (container) (typed FeaturePython)
  n = 1
  ref = O_element
FEATURE [App::DocumentObjectGroupPython] G4_ETHYL_ALCOHOL  # scripted group (container) (typed FeaturePython)
  Dunit = g/cm3
  Dvalue = 0.7893
  Group = -> [C_element039,H_element036,O_element035]
  conduct = 2
  density = 1
  expand = 3
  formula = G4_ETHYL_ALCOHOL
  name = G4_ETHYL_ALCOHOL
  specific = 4
FEATURE [App::DocumentObjectGroupPython] H_element037  label="H_element : 0.090"  # scripted group (container) (typed FeaturePython)
  n = 0.090027
FEATURE [App::DocumentObjectGroupPython] C_element040  label="C_element : 0.585"  # scripted group (container) (typed FeaturePython)
  n = 0.585182
FEATURE [App::DocumentObjectGroupPython] O_element036  label="O_element : 0.325"  # scripted group (container) (typed FeaturePython)
  n = 0.324791
FEATURE [App::DocumentObjectGroupPython] G4_ETHYL_CELLULOSE  # scripted group (container) (typed FeaturePython)
  Dunit = g/cm3
  Dvalue = 1.13
  Group = -> [H_element037,C_element040,O_element036]
  conduct = 2
  density = 1
  expand = 3
  formula = G4_ETHYL_CELLULOSE
  name = G4_ETHYL_CELLULOSE
  specific = 4
FEATURE [App::DocumentObjectGroupPython] C_element041  label="C_element : 024"  # scripted group (container) (typed FeaturePython)
  n = 2
  ref = C_element
FEATURE [App::DocumentObjectGroupPython] H_element038  label="H_element : 020"  # scripted group (container) (typed FeaturePython)
  n = 4
  ref = H_element
FEATURE [App::DocumentObjectGroupPython] G4_ETHYLENE  # scripted group (container) (typed FeaturePython)
  Dunit = g/cm3
  Dvalue = 0.00117497
  Group = -> [C_element041,H_element038]
  conduct = 2
  density = 1
  expand = 3
  formula = G4_ETHYLENE
  name = G4_ETHYLENE
  specific = 4
FEATURE [App::DocumentObjectGroupPython] H_element039  label="H_element : 0.096"  # scripted group (container) (typed FeaturePython)
  n = 0.096
FEATURE [App::DocumentObjectGroupPython] C_element042  label="C_element : 0.195"  # scripted group (container) (typed FeaturePython)
  n = 0.195
FEATURE [App::DocumentObjectGroupPython] N_element016  label="N_element : 0.057"  # scripted group (container) (typed FeaturePython)
  n = 0.057
FEATURE [App::DocumentObjectGroupPython] O_element037  label="O_element : 0.646"  # scripted group (container) (typed FeaturePython)
  n = 0.646
FEATURE [App::DocumentObjectGroupPython] Na_element006  label="Na_element : 0.017"  # scripted group (container) (typed FeaturePython)
  n = 0.001
FEATURE [App::DocumentObjectGroupPython] P_element005  label="P_element : 0.104"  # scripted group (container) (typed FeaturePython)
  n = 0.001
FEATURE [App::DocumentObjectGroupPython] S_element010  label="S_element : 0.016"  # scripted group (container) (typed FeaturePython)
  n = 0.003
FEATURE [App::DocumentObjectGroupPython] Cl_element010  label="Cl_element : 0.005"  # scripted group (container) (typed FeaturePython)
  n = 0.001
FEATURE [App::DocumentObjectGroupPython] G4_EYE_LENS_ICRP  # scripted group (container) (typed FeaturePython)
  Dunit = g/cm3
  Dvalue = 1.07
  Group = -> [H_element039,C_element042,N_element016,O_element037,Na_element006,P_element005,S_element010,Cl_element010]
  conduct = 2
  density = 1
  expand = 3
  formula = G4_EYE_LENS_ICRP
  name = G4_EYE_LENS_ICRP
  specific = 4
FEATURE [App::DocumentObjectGroupPython] Fe_element003  label="Fe_element : 2"  # scripted group (container) (typed FeaturePython)
  n = 2
  ref = Fe_element
FEATURE [App::DocumentObjectGroupPython] O_element038  label="O_element : 019"  # scripted group (container) (typed FeaturePython)
  n = 3
  ref = O_element
FEATURE [App::DocumentObjectGroupPython] G4_FERRIC_OXIDE  # scripted group (container) (typed FeaturePython)
  Dunit = g/cm3
  Dvalue = 5.2
  Group = -> [Fe_element003,O_element038]
  conduct = 2
  density = 1
  expand = 3
  formula = G4_FERRIC_OXIDE
  name = G4_FERRIC_OXIDE
  specific = 4
FEATURE [App::DocumentObjectGroupPython] Fe_element004  label="Fe_element : 1"  # scripted group (container) (typed FeaturePython)
  n = 1
  ref = Fe_element
FEATURE [App::DocumentObjectGroupPython] B_element003  label="B_element : 1"  # scripted group (container) (typed FeaturePython)
  n = 1
  ref = B_element
FEATURE [App::DocumentObjectGroupPython] G4_FERROBORIDE  # scripted group (container) (typed FeaturePython)
  Dunit = g/cm3
  Dvalue = 7.15
  Group = -> [Fe_element004,B_element003]
  conduct = 2
  density = 1
  expand = 3
  formula = G4_FERROBORIDE
  name = G4_FERROBORIDE
  specific = 4
FEATURE [App::DocumentObjectGroupPython] Fe_element005  label="Fe_element : 003"  # scripted group (container) (typed FeaturePython)
  n = 1
  ref = Fe_element
FEATURE [App::DocumentObjectGroupPython] O_element039  label="O_element : 020"  # scripted group (container) (typed FeaturePython)
  n = 1
  ref = O_element
FEATURE [App::DocumentObjectGroupPython] G4_FERROUS_OXIDE  # scripted group (container) (typed FeaturePython)
  Dunit = g/cm3
  Dvalue = 5.7
  Group = -> [Fe_element005,O_element039]
  conduct = 2
  density = 1
  expand = 3
  formula = G4_FERROUS_OXIDE
  name = G4_FERROUS_OXIDE
  specific = 4
FEATURE [App::DocumentObjectGroupPython] H_element040  label="H_element : 0.115"  # scripted group (container) (typed FeaturePython)
  n = 0.108259
FEATURE [App::DocumentObjectGroupPython] N_element017  label="N_element : 0.000"  # scripted group (container) (typed FeaturePython)
  n = 2.7e-05
FEATURE [App::DocumentObjectGroupPython] O_element040  label="O_element : 0.879"  # scripted group (container) (typed FeaturePython)
  n = 0.878636
FEATURE [App::DocumentObjectGroupPython] Na_element007  label="Na_element : 0.000"  # scripted group (container) (typed FeaturePython)
  n = 2.2e-05
FEATURE [App::DocumentObjectGroupPython] S_element011  label="S_element : 0.013"  # scripted group (container) (typed FeaturePython)
  n = 0.012968
FEATURE [App::DocumentObjectGroupPython] Cl_element011  label="Cl_element : 0.000"  # scripted group (container) (typed FeaturePython)
  n = 3.4e-05
FEATURE [App::DocumentObjectGroupPython] Fe_element006  label="Fe_element : 0.000"  # scripted group (container) (typed FeaturePython)
  n = 5.4e-05
FEATURE [App::DocumentObjectGroupPython] G4_FERROUS_SULFATE  # scripted group (container) (typed FeaturePython)
  Dunit = g/cm3
  Dvalue = 1.024
  Group = -> [H_element040,N_element017,O_element040,Na_element007,S_element011,Cl_element011,Fe_element006]
  conduct = 2
  density = 1
  expand = 3
  formula = G4_FERROUS_SULFATE
  name = G4_FERROUS_SULFATE
  specific = 4
FEATURE [App::DocumentObjectGroupPython] C_element043  label="C_element : 0.099"  # scripted group (container) (typed FeaturePython)
  n = 0.099335
FEATURE [App::DocumentObjectGroupPython] F_element007  label="F_element : 0.314"  # scripted group (container) (typed FeaturePython)
  n = 0.314247
FEATURE [App::DocumentObjectGroupPython] Cl_element012  label="Cl_element : 0.586"  # scripted group (container) (typed FeaturePython)
  n = 0.586418
FEATURE [App::DocumentObjectGroupPython] G4_FREON_12  label="G4_FREON-12"  # scripted group (container) (typed FeaturePython)
  Dunit = g/cm3
  Dvalue = 1.12
  Group = -> [C_element043,F_element007,Cl_element012]
  conduct = 2
  density = 1
  expand = 3
  formula = G4_FREON-12
  name = G4_FREON-12
  specific = 4
FEATURE [App::DocumentObjectGroupPython] C_element044  label="C_element : 0.057"  # scripted group (container) (typed FeaturePython)
  n = 0.057245
FEATURE [App::DocumentObjectGroupPython] F_element008  label="F_element : 0.181"  # scripted group (container) (typed FeaturePython)
  n = 0.181096
FEATURE [App::DocumentObjectGroupPython] Br_element001  label="Br_element : 0.762"  # scripted group (container) (typed FeaturePython)
  n = 0.761659
FEATURE [App::DocumentObjectGroupPython] G4_FREON_12B2  label="G4_FREON-12B2"  # scripted group (container) (typed FeaturePython)
  Dunit = g/cm3
  Dvalue = 1.8
  Group = -> [C_element044,F_element008,Br_element001]
  conduct = 2
  density = 1
  expand = 3
  formula = G4_FREON-12B2
  name = G4_FREON-12B2
  specific = 4
FEATURE [App::DocumentObjectGroupPython] C_element045  label="C_element : 0.115"  # scripted group (container) (typed FeaturePython)
  n = 0.114983
FEATURE [App::DocumentObjectGroupPython] F_element009  label="F_element : 0.546"  # scripted group (container) (typed FeaturePython)
  n = 0.545621
FEATURE [App::DocumentObjectGroupPython] Cl_element013  label="Cl_element : 0.339"  # scripted group (container) (typed FeaturePython)
  n = 0.339396
FEATURE [App::DocumentObjectGroupPython] G4_FREON_13  label="G4_FREON-13"  # scripted group (container) (typed FeaturePython)
  Dunit = g/cm3
  Dvalue = 0.95
  Group = -> [C_element045,F_element009,Cl_element013]
  conduct = 2
  density = 1
  expand = 3
  formula = G4_FREON-13
  name = G4_FREON-13
  specific = 4
FEATURE [App::DocumentObjectGroupPython] C_element046  label="C_element : 025"  # scripted group (container) (typed FeaturePython)
  n = 1
  ref = C_element
FEATURE [App::DocumentObjectGroupPython] F_element010  label="F_element : 3"  # scripted group (container) (typed FeaturePython)
  n = 3
  ref = F_element
FEATURE [App::DocumentObjectGroupPython] Br_element002  label="Br_element : 1"  # scripted group (container) (typed FeaturePython)
  n = 1
  ref = Br_element
FEATURE [App::DocumentObjectGroupPython] G4_FREON_13B1  label="G4_FREON-13B1"  # scripted group (container) (typed FeaturePython)
  Dunit = g/cm3
  Dvalue = 1.5
  Group = -> [C_element046,F_element010,Br_element002]
  conduct = 2
  density = 1
  expand = 3
  formula = G4_FREON-13B1
  name = G4_FREON-13B1
  specific = 4
FEATURE [App::DocumentObjectGroupPython] C_element047  label="C_element : 0.061"  # scripted group (container) (typed FeaturePython)
  n = 0.061309
FEATURE [App::DocumentObjectGroupPython] F_element011  label="F_element : 0.291"  # scripted group (container) (typed FeaturePython)
  n = 0.290924
FEATURE [App::DocumentObjectGroupPython] I_element002  label="I_element : 0.648"  # scripted group (container) (typed FeaturePython)
  n = 0.647767
FEATURE [App::DocumentObjectGroupPython] G4_FREON_13I1  label="G4_FREON-13I1"  # scripted group (container) (typed FeaturePython)
  Dunit = g/cm3
  Dvalue = 1.8
  Group = -> [C_element047,F_element011,I_element002]
  conduct = 2
  density = 1
  expand = 3
  formula = G4_FREON-13I1
  name = G4_FREON-13I1
  specific = 4
FEATURE [App::DocumentObjectGroupPython] Gd_element001  label="Gd_element : 2"  # scripted group (container) (typed FeaturePython)
  n = 2
  ref = Gd_element
FEATURE [App::DocumentObjectGroupPython] O_element041  label="O_element : 021"  # scripted group (container) (typed FeaturePython)
  n = 2
  ref = O_element
FEATURE [App::DocumentObjectGroupPython] S_element012  label="S_element : 004"  # scripted group (container) (typed FeaturePython)
  n = 1
  ref = S_element
FEATURE [App::DocumentObjectGroupPython] G4_GADOLINIUM_OXYSULFIDE  # scripted group (container) (typed FeaturePython)
  Dunit = g/cm3
  Dvalue = 7.44
  Group = -> [Gd_element001,O_element041,S_element012]
  conduct = 2
  density = 1
  expand = 3
  formula = G4_GADOLINIUM_OXYSULFIDE
  name = G4_GADOLINIUM_OXYSULFIDE
  specific = 4
FEATURE [App::DocumentObjectGroupPython] Ga_element001  label="Ga_element : 1"  # scripted group (container) (typed FeaturePython)
  n = 1
  ref = Ga_element
FEATURE [App::DocumentObjectGroupPython] As_element001  label="As_element : 1"  # scripted group (container) (typed FeaturePython)
  n = 1
  ref = As_element
FEATURE [App::DocumentObjectGroupPython] G4_GALLIUM_ARSENIDE  # scripted group (container) (typed FeaturePython)
  Dunit = g/cm3
  Dvalue = 5.31
  Group = -> [Ga_element001,As_element001]
  conduct = 2
  density = 1
  expand = 3
  formula = G4_GALLIUM_ARSENIDE
  name = G4_GALLIUM_ARSENIDE
  specific = 4
FEATURE [App::DocumentObjectGroupPython] H_element041  label="H_element : 0.081"  # scripted group (container) (typed FeaturePython)
  n = 0.08118
FEATURE [App::DocumentObjectGroupPython] C_element048  label="C_element : 0.416"  # scripted group (container) (typed FeaturePython)
  n = 0.41606
FEATURE [App::DocumentObjectGroupPython] N_element018  label="N_element : 0.111"  # scripted group (container) (typed FeaturePython)
  n = 0.11124
FEATURE [App::DocumentObjectGroupPython] O_element042  label="O_element : 0.381"  # scripted group (container) (typed FeaturePython)
  n = 0.38064
FEATURE [App::DocumentObjectGroupPython] S_element013  label="S_element : 0.011"  # scripted group (container) (typed FeaturePython)
  n = 0.01088
FEATURE [App::DocumentObjectGroupPython] G4_GEL_PHOTO_EMULSION  # scripted group (container) (typed FeaturePython)
  Dunit = g/cm3
  Dvalue = 1.2914
  Group = -> [H_element041,C_element048,N_element018,O_element042,S_element013]
  conduct = 2
  density = 1
  expand = 3
  formula = G4_GEL_PHOTO_EMULSION
  name = G4_GEL_PHOTO_EMULSION
  specific = 4
FEATURE [App::DocumentObjectGroupPython] B_element004  label="B_element : 0.040"  # scripted group (container) (typed FeaturePython)
  n = 0.0400639
FEATURE [App::DocumentObjectGroupPython] O_element043  label="O_element : 0.540"  # scripted group (container) (typed FeaturePython)
  n = 0.539561
FEATURE [App::DocumentObjectGroupPython] Na_element008  label="Na_element : 0.028"  # scripted group (container) (typed FeaturePython)
  n = 0.0281909
FEATURE [App::DocumentObjectGroupPython] Al_element003  label="Al_element : 0.012"  # scripted group (container) (typed FeaturePython)
  n = 0.011644
FEATURE [App::DocumentObjectGroupPython] Si_element003  label="Si_element : 0.377"  # scripted group (container) (typed FeaturePython)
  n = 0.377219
FEATURE [App::DocumentObjectGroupPython] K_element004  label="K_element : 0.014"  # scripted group (container) (typed FeaturePython)
  n = 0.00332099
FEATURE [App::DocumentObjectGroupPython] G4_Pyrex_Glass  # scripted group (container) (typed FeaturePython)
  Dunit = g/cm3
  Dvalue = 2.23
  Group = -> [B_element004,O_element043,Na_element008,Al_element003,Si_element003,K_element004]
  conduct = 2
  density = 1
  expand = 3
  formula = G4_Pyrex_Glass
  name = G4_Pyrex_Glass
  specific = 4
FEATURE [App::DocumentObjectGroupPython] O_element044  label="O_element : 0.156"  # scripted group (container) (typed FeaturePython)
  n = 0.156453
FEATURE [App::DocumentObjectGroupPython] Si_element004  label="Si_element : 0.081"  # scripted group (container) (typed FeaturePython)
  n = 0.080866
FEATURE [App::DocumentObjectGroupPython] Ti_element001  label="Ti_element : 0.008"  # scripted group (container) (typed FeaturePython)
  n = 0.008092
FEATURE [App::DocumentObjectGroupPython] As_element002  label="As_element : 0.003"  # scripted group (container) (typed FeaturePython)
  n = 0.002651
FEATURE [App::DocumentObjectGroupPython] Pb_element001  label="Pb_element : 0.752"  # scripted group (container) (typed FeaturePython)
  n = 0.751938
FEATURE [App::DocumentObjectGroupPython] G4_GLASS_LEAD  # scripted group (container) (typed FeaturePython)
  Dunit = g/cm3
  Dvalue = 6.22
  Group = -> [O_element044,Si_element004,Ti_element001,As_element002,Pb_element001]
  conduct = 2
  density = 1
  expand = 3
  formula = G4_GLASS_LEAD
  name = G4_GLASS_LEAD
  specific = 4
FEATURE [App::DocumentObjectGroupPython] O_element045  label="O_element : 0.460"  # scripted group (container) (typed FeaturePython)
  n = 0.4598
FEATURE [App::DocumentObjectGroupPython] Na_element009  label="Na_element : 0.096"  # scripted group (container) (typed FeaturePython)
  n = 0.0964411
FEATURE [App::DocumentObjectGroupPython] Si_element005  label="Si_element : 0.378"  # scripted group (container) (typed FeaturePython)
  n = 0.336553
FEATURE [App::DocumentObjectGroupPython] Ca_element011  label="Ca_element : 0.107"  # scripted group (container) (typed FeaturePython)
  n = 0.107205
FEATURE [App::DocumentObjectGroupPython] G4_GLASS_PLATE  # scripted group (container) (typed FeaturePython)
  Dunit = g/cm3
  Dvalue = 2.4
  Group = -> [O_element045,Na_element009,Si_element005,Ca_element011]
  conduct = 2
  density = 1
  expand = 3
  formula = G4_GLASS_PLATE
  name = G4_GLASS_PLATE
  specific = 4
FEATURE [App::DocumentObjectGroupPython] C_element049  label="C_element : 026"  # scripted group (container) (typed FeaturePython)
  n = 5
  ref = C_element
FEATURE [App::DocumentObjectGroupPython] H_element042  label="H_element : 021"  # scripted group (container) (typed FeaturePython)
  n = 10
  ref = H_element
FEATURE [App::DocumentObjectGroupPython] N_element019  label="N_element : 2"  # scripted group (container) (typed FeaturePython)
  n = 2
  ref = N_element
FEATURE [App::DocumentObjectGroupPython] O_element046  label="O_element : 022"  # scripted group (container) (typed FeaturePython)
  n = 3
  ref = O_element
FEATURE [App::DocumentObjectGroupPython] G4_GLUTAMINE  # scripted group (container) (typed FeaturePython)
  Dunit = g/cm3
  Dvalue = 1.46
  Group = -> [C_element049,H_element042,N_element019,O_element046]
  conduct = 2
  density = 1
  expand = 3
  formula = G4_GLUTAMINE
  name = G4_GLUTAMINE
  specific = 4
FEATURE [App::DocumentObjectGroupPython] C_element050  label="C_element : 027"  # scripted group (container) (typed FeaturePython)
  n = 3
  ref = C_element
FEATURE [App::DocumentObjectGroupPython] H_element043  label="H_element : 022"  # scripted group (container) (typed FeaturePython)
  n = 8
  ref = H_element
FEATURE [App::DocumentObjectGroupPython] O_element047  label="O_element : 023"  # scripted group (container) (typed FeaturePython)
  n = 3
  ref = O_element
FEATURE [App::DocumentObjectGroupPython] G4_GLYCEROL  # scripted group (container) (typed FeaturePython)
  Dunit = g/cm3
  Dvalue = 1.2613
  Group = -> [C_element050,H_element043,O_element047]
  conduct = 2
  density = 1
  expand = 3
  formula = G4_GLYCEROL
  name = G4_GLYCEROL
  specific = 4
FEATURE [App::DocumentObjectGroupPython] C_element051  label="C_element : 028"  # scripted group (container) (typed FeaturePython)
  n = 5
  ref = C_element
FEATURE [App::DocumentObjectGroupPython] H_element044  label="H_element : 023"  # scripted group (container) (typed FeaturePython)
  n = 5
  ref = H_element
FEATURE [App::DocumentObjectGroupPython] N_element020  label="N_element : 009"  # scripted group (container) (typed FeaturePython)
  n = 5
  ref = N_element
FEATURE [App::DocumentObjectGroupPython] O_element048  label="O_element : 024"  # scripted group (container) (typed FeaturePython)
  n = 1
  ref = O_element
FEATURE [App::DocumentObjectGroupPython] G4_GUANINE  # scripted group (container) (typed FeaturePython)
  Dunit = g/cm3
  Dvalue = 2.2
  Group = -> [C_element051,H_element044,N_element020,O_element048]
  conduct = 2
  density = 1
  expand = 3
  formula = G4_GUANINE
  name = G4_GUANINE
  specific = 4
FEATURE [App::DocumentObjectGroupPython] Ca_element012  label="Ca_element : 006"  # scripted group (container) (typed FeaturePython)
  n = 1
  ref = Ca_element
FEATURE [App::DocumentObjectGroupPython] S_element014  label="S_element : 005"  # scripted group (container) (typed FeaturePython)
  n = 1
  ref = S_element
FEATURE [App::DocumentObjectGroupPython] O_element049  label="O_element : 6"  # scripted group (container) (typed FeaturePython)
  n = 6
  ref = O_element
FEATURE [App::DocumentObjectGroupPython] H_element045  label="H_element : 024"  # scripted group (container) (typed FeaturePython)
  n = 4
  ref = H_element
FEATURE [App::DocumentObjectGroupPython] G4_GYPSUM  # scripted group (container) (typed FeaturePython)
  Dunit = g/cm3
  Dvalue = 2.32
  Group = -> [Ca_element012,S_element014,O_element049,H_element045]
  conduct = 2
  density = 1
  expand = 3
  formula = G4_GYPSUM
  name = G4_GYPSUM
  specific = 4
FEATURE [App::DocumentObjectGroupPython] C_element052  label="C_element : 7"  # scripted group (container) (typed FeaturePython)
  n = 7
  ref = C_element
FEATURE [App::DocumentObjectGroupPython] H_element046  label="H_element : 16"  # scripted group (container) (typed FeaturePython)
  n = 16
  ref = H_element
FEATURE [App::DocumentObjectGroupPython] G4_N_HEPTANE  label="G4_N-HEPTANE"  # scripted group (container) (typed FeaturePython)
  Dunit = g/cm3
  Dvalue = 0.68376
  Group = -> [C_element052,H_element046]
  conduct = 2
  density = 1
  expand = 3
  formula = G4_N-HEPTANE
  name = G4_N-HEPTANE
  specific = 4
FEATURE [App::DocumentObjectGroupPython] C_element053  label="C_element : 029"  # scripted group (container) (typed FeaturePython)
  n = 6
  ref = C_element
FEATURE [App::DocumentObjectGroupPython] H_element047  label="H_element : 14"  # scripted group (container) (typed FeaturePython)
  n = 14
  ref = H_element
FEATURE [App::DocumentObjectGroupPython] G4_N_HEXANE  label="G4_N-HEXANE"  # scripted group (container) (typed FeaturePython)
  Dunit = g/cm3
  Dvalue = 0.6603
  Group = -> [C_element053,H_element047]
  conduct = 2
  density = 1
  expand = 3
  formula = G4_N-HEXANE
  name = G4_N-HEXANE
  specific = 4
FEATURE [App::DocumentObjectGroupPython] C_element054  label="C_element : 22"  # scripted group (container) (typed FeaturePython)
  n = 22
  ref = C_element
FEATURE [App::DocumentObjectGroupPython] H_element048  label="H_element : 025"  # scripted group (container) (typed FeaturePython)
  n = 10
  ref = H_element
FEATURE [App::DocumentObjectGroupPython] N_element021  label="N_element : 010"  # scripted group (container) (typed FeaturePython)
  n = 2
  ref = N_element
FEATURE [App::DocumentObjectGroupPython] O_element050  label="O_element : 025"  # scripted group (container) (typed FeaturePython)
  n = 5
  ref = O_element
FEATURE [App::DocumentObjectGroupPython] G4_KAPTON  # scripted group (container) (typed FeaturePython)
  Dunit = g/cm3
  Dvalue = 1.42
  Group = -> [C_element054,H_element048,N_element021,O_element050]
  conduct = 2
  density = 1
  expand = 3
  formula = G4_KAPTON
  name = G4_KAPTON
  specific = 4
FEATURE [App::DocumentObjectGroupPython] La_element001  label="La_element : 1"  # scripted group (container) (typed FeaturePython)
  n = 1
  ref = La_element
FEATURE [App::DocumentObjectGroupPython] Br_element003  label="Br_element : 002"  # scripted group (container) (typed FeaturePython)
  n = 1
  ref = Br_element
FEATURE [App::DocumentObjectGroupPython] O_element051  label="O_element : 026"  # scripted group (container) (typed FeaturePython)
  n = 1
  ref = O_element
FEATURE [App::DocumentObjectGroupPython] G4_LANTHANUM_OXYBROMIDE  # scripted group (container) (typed FeaturePython)
  Dunit = g/cm3
  Dvalue = 6.28
  Group = -> [La_element001,Br_element003,O_element051]
  conduct = 2
  density = 1
  expand = 3
  formula = G4_LANTHANUM_OXYBROMIDE
  name = G4_LANTHANUM_OXYBROMIDE
  specific = 4
FEATURE [App::DocumentObjectGroupPython] La_element002  label="La_element : 2"  # scripted group (container) (typed FeaturePython)
  n = 2
  ref = La_element
FEATURE [App::DocumentObjectGroupPython] O_element052  label="O_element : 027"  # scripted group (container) (typed FeaturePython)
  n = 2
  ref = O_element
FEATURE [App::DocumentObjectGroupPython] S_element015  label="S_element : 006"  # scripted group (container) (typed FeaturePython)
  n = 1
  ref = S_element
FEATURE [App::DocumentObjectGroupPython] G4_LANTHANUM_OXYSULFIDE  # scripted group (container) (typed FeaturePython)
  Dunit = g/cm3
  Dvalue = 5.86
  Group = -> [La_element002,O_element052,S_element015]
  conduct = 2
  density = 1
  expand = 3
  formula = G4_LANTHANUM_OXYSULFIDE
  name = G4_LANTHANUM_OXYSULFIDE
  specific = 4
FEATURE [App::DocumentObjectGroupPython] O_element053  label="O_element : 0.072"  # scripted group (container) (typed FeaturePython)
  n = 0.071682
FEATURE [App::DocumentObjectGroupPython] Pb_element002  label="Pb_element : 0.928"  # scripted group (container) (typed FeaturePython)
  n = 0.928318
FEATURE [App::DocumentObjectGroupPython] G4_LEAD_OXIDE  # scripted group (container) (typed FeaturePython)
  Dunit = g/cm3
  Dvalue = 9.53
  Group = -> [O_element053,Pb_element002]
  conduct = 2
  density = 1
  expand = 3
  formula = G4_LEAD_OXIDE
  name = G4_LEAD_OXIDE
  specific = 4
FEATURE [App::DocumentObjectGroupPython] Li_element001  label="Li_element : 1"  # scripted group (container) (typed FeaturePython)
  n = 1
  ref = Li_element
FEATURE [App::DocumentObjectGroupPython] N_element022  label="N_element : 011"  # scripted group (container) (typed FeaturePython)
  n = 1
  ref = N_element
FEATURE [App::DocumentObjectGroupPython] H_element049  label="H_element : 026"  # scripted group (container) (typed FeaturePython)
  n = 2
  ref = H_element
FEATURE [App::DocumentObjectGroupPython] G4_LITHIUM_AMIDE  # scripted group (container) (typed FeaturePython)
  Dunit = g/cm3
  Dvalue = 1.178
  Group = -> [Li_element001,N_element022,H_element049]
  conduct = 2
  density = 1
  expand = 3
  formula = G4_LITHIUM_AMIDE
  name = G4_LITHIUM_AMIDE
  specific = 4
FEATURE [App::DocumentObjectGroupPython] Li_element002  label="Li_element : 2"  # scripted group (container) (typed FeaturePython)
  n = 2
  ref = Li_element
FEATURE [App::DocumentObjectGroupPython] C_element055  label="C_element : 030"  # scripted group (container) (typed FeaturePython)
  n = 1
  ref = C_element
FEATURE [App::DocumentObjectGroupPython] O_element054  label="O_element : 028"  # scripted group (container) (typed FeaturePython)
  n = 3
  ref = O_element
FEATURE [App::DocumentObjectGroupPython] G4_LITHIUM_CARBONATE  # scripted group (container) (typed FeaturePython)
  Dunit = g/cm3
  Dvalue = 2.11
  Group = -> [Li_element002,C_element055,O_element054]
  conduct = 2
  density = 1
  expand = 3
  formula = G4_LITHIUM_CARBONATE
  name = G4_LITHIUM_CARBONATE
  specific = 4
FEATURE [App::DocumentObjectGroupPython] Li_element003  label="Li_element : 003"  # scripted group (container) (typed FeaturePython)
  n = 1
  ref = Li_element
FEATURE [App::DocumentObjectGroupPython] F_element012  label="F_element : 004"  # scripted group (container) (typed FeaturePython)
  n = 1
  ref = F_element
FEATURE [App::DocumentObjectGroupPython] G4_LITHIUM_FLUORIDE  # scripted group (container) (typed FeaturePython)
  Dunit = g/cm3
  Dvalue = 2.635
  Group = -> [Li_element003,F_element012]
  conduct = 2
  density = 1
  expand = 3
  formula = G4_LITHIUM_FLUORIDE
  name = G4_LITHIUM_FLUORIDE
  specific = 4
FEATURE [App::DocumentObjectGroupPython] Li_element004  label="Li_element : 004"  # scripted group (container) (typed FeaturePython)
  n = 1
  ref = Li_element
FEATURE [App::DocumentObjectGroupPython] H_element050  label="H_element : 027"  # scripted group (container) (typed FeaturePython)
  n = 1
  ref = H_element
FEATURE [App::DocumentObjectGroupPython] G4_LITHIUM_HYDRIDE  # scripted group (container) (typed FeaturePython)
  Dunit = g/cm3
  Dvalue = 0.82
  Group = -> [Li_element004,H_element050]
  conduct = 2
  density = 1
  expand = 3
  formula = G4_LITHIUM_HYDRIDE
  name = G4_LITHIUM_HYDRIDE
  specific = 4
FEATURE [App::DocumentObjectGroupPython] Li_element005  label="Li_element : 005"  # scripted group (container) (typed FeaturePython)
  n = 1
  ref = Li_element
FEATURE [App::DocumentObjectGroupPython] I_element003  label="I_element : 002"  # scripted group (container) (typed FeaturePython)
  n = 1
  ref = I_element
FEATURE [App::DocumentObjectGroupPython] G4_LITHIUM_IODIDE  # scripted group (container) (typed FeaturePython)
  Dunit = g/cm3
  Dvalue = 3.494
  Group = -> [Li_element005,I_element003]
  conduct = 2
  density = 1
  expand = 3
  formula = G4_LITHIUM_IODIDE
  name = G4_LITHIUM_IODIDE
  specific = 4
FEATURE [App::DocumentObjectGroupPython] Li_element006  label="Li_element : 006"  # scripted group (container) (typed FeaturePython)
  n = 2
  ref = Li_element
FEATURE [App::DocumentObjectGroupPython] O_element055  label="O_element : 029"  # scripted group (container) (typed FeaturePython)
  n = 1
  ref = O_element
FEATURE [App::DocumentObjectGroupPython] G4_LITHIUM_OXIDE  # scripted group (container) (typed FeaturePython)
  Dunit = g/cm3
  Dvalue = 2.013
  Group = -> [Li_element006,O_element055]
  conduct = 2
  density = 1
  expand = 3
  formula = G4_LITHIUM_OXIDE
  name = G4_LITHIUM_OXIDE
  specific = 4
FEATURE [App::DocumentObjectGroupPython] Li_element007  label="Li_element : 007"  # scripted group (container) (typed FeaturePython)
  n = 2
  ref = Li_element
FEATURE [App::DocumentObjectGroupPython] B_element005  label="B_element : 005"  # scripted group (container) (typed FeaturePython)
  n = 4
  ref = B_element
FEATURE [App::DocumentObjectGroupPython] O_element056  label="O_element : 7"  # scripted group (container) (typed FeaturePython)
  n = 7
  ref = O_element
FEATURE [App::DocumentObjectGroupPython] G4_LITHIUM_TETRABORATE  # scripted group (container) (typed FeaturePython)
  Dunit = g/cm3
  Dvalue = 2.44
  Group = -> [Li_element007,B_element005,O_element056]
  conduct = 2
  density = 1
  expand = 3
  formula = G4_LITHIUM_TETRABORATE
  name = G4_LITHIUM_TETRABORATE
  specific = 4
FEATURE [App::DocumentObjectGroupPython] H_element051  label="H_element : 0.105"  # scripted group (container) (typed FeaturePython)
  n = 0.105
FEATURE [App::DocumentObjectGroupPython] C_element056  label="C_element : 0.083"  # scripted group (container) (typed FeaturePython)
  n = 0.083
FEATURE [App::DocumentObjectGroupPython] N_element023  label="N_element : 0.023"  # scripted group (container) (typed FeaturePython)
  n = 0.023
FEATURE [App::DocumentObjectGroupPython] O_element057  label="O_element : 0.779"  # scripted group (container) (typed FeaturePython)
  n = 0.779
FEATURE [App::DocumentObjectGroupPython] Na_element010  label="Na_element : 0.097"  # scripted group (container) (typed FeaturePython)
  n = 0.002
FEATURE [App::DocumentObjectGroupPython] P_element006  label="P_element : 0.105"  # scripted group (container) (typed FeaturePython)
  n = 0.001
FEATURE [App::DocumentObjectGroupPython] S_element016  label="S_element : 0.017"  # scripted group (container) (typed FeaturePython)
  n = 0.002
FEATURE [App::DocumentObjectGroupPython] Cl_element014  label="Cl_element : 0.587"  # scripted group (container) (typed FeaturePython)
  n = 0.003
FEATURE [App::DocumentObjectGroupPython] K_element005  label="K_element : 0.015"  # scripted group (container) (typed FeaturePython)
  n = 0.002
FEATURE [App::DocumentObjectGroupPython] G4_LUNG_ICRP  # scripted group (container) (typed FeaturePython)
  Dunit = g/cm3
  Dvalue = 1.04
  Group = -> [H_element051,C_element056,N_element023,O_element057,Na_element010,P_element006,S_element016,Cl_element014,K_element005]
  conduct = 2
  density = 1
  expand = 3
  formula = G4_LUNG_ICRP
  name = G4_LUNG_ICRP
  specific = 4
FEATURE [App::DocumentObjectGroupPython] H_element052  label="H_element : 0.116"  # scripted group (container) (typed FeaturePython)
  n = 0.114318
FEATURE [App::DocumentObjectGroupPython] C_element057  label="C_element : 0.656"  # scripted group (container) (typed FeaturePython)
  n = 0.655824
FEATURE [App::DocumentObjectGroupPython] O_element058  label="O_element : 0.092"  # scripted group (container) (typed FeaturePython)
  n = 0.0921831
FEATURE [App::DocumentObjectGroupPython] Mg_element004  label="Mg_element : 0.135"  # scripted group (container) (typed FeaturePython)
  n = 0.134792
FEATURE [App::DocumentObjectGroupPython] Ca_element013  label="Ca_element : 0.003"  # scripted group (container) (typed FeaturePython)
  n = 0.002883
FEATURE [App::DocumentObjectGroupPython] G4_M3_WAX  # scripted group (container) (typed FeaturePython)
  Dunit = g/cm3
  Dvalue = 1.05
  Group = -> [H_element052,C_element057,O_element058,Mg_element004,Ca_element013]
  conduct = 2
  density = 1
  expand = 3
  formula = G4_M3_WAX
  name = G4_M3_WAX
  specific = 4
FEATURE [App::DocumentObjectGroupPython] Mg_element005  label="Mg_element : 1"  # scripted group (container) (typed FeaturePython)
  n = 1
  ref = Mg_element
FEATURE [App::DocumentObjectGroupPython] C_element058  label="C_element : 031"  # scripted group (container) (typed FeaturePython)
  n = 1
  ref = C_element
FEATURE [App::DocumentObjectGroupPython] O_element059  label="O_element : 030"  # scripted group (container) (typed FeaturePython)
  n = 3
  ref = O_element
FEATURE [App::DocumentObjectGroupPython] G4_MAGNESIUM_CARBONATE  # scripted group (container) (typed FeaturePython)
  Dunit = g/cm3
  Dvalue = 2.958
  Group = -> [Mg_element005,C_element058,O_element059]
  conduct = 2
  density = 1
  expand = 3
  formula = G4_MAGNESIUM_CARBONATE
  name = G4_MAGNESIUM_CARBONATE
  specific = 4
FEATURE [App::DocumentObjectGroupPython] Mg_element006  label="Mg_element : 002"  # scripted group (container) (typed FeaturePython)
  n = 1
  ref = Mg_element
FEATURE [App::DocumentObjectGroupPython] F_element013  label="F_element : 005"  # scripted group (container) (typed FeaturePython)
  n = 2
  ref = F_element
FEATURE [App::DocumentObjectGroupPython] G4_MAGNESIUM_FLUORIDE  # scripted group (container) (typed FeaturePython)
  Dunit = g/cm3
  Dvalue = 3
  Group = -> [Mg_element006,F_element013]
  conduct = 2
  density = 1
  expand = 3
  formula = G4_MAGNESIUM_FLUORIDE
  name = G4_MAGNESIUM_FLUORIDE
  specific = 4
FEATURE [App::DocumentObjectGroupPython] Mg_element007  label="Mg_element : 003"  # scripted group (container) (typed FeaturePython)
  n = 1
  ref = Mg_element
FEATURE [App::DocumentObjectGroupPython] O_element060  label="O_element : 031"  # scripted group (container) (typed FeaturePython)
  n = 1
  ref = O_element
FEATURE [App::DocumentObjectGroupPython] G4_MAGNESIUM_OXIDE  # scripted group (container) (typed FeaturePython)
  Dunit = g/cm3
  Dvalue = 3.58
  Group = -> [Mg_element007,O_element060]
  conduct = 2
  density = 1
  expand = 3
  formula = G4_MAGNESIUM_OXIDE
  name = G4_MAGNESIUM_OXIDE
  specific = 4
FEATURE [App::DocumentObjectGroupPython] Mg_element008  label="Mg_element : 004"  # scripted group (container) (typed FeaturePython)
  n = 1
  ref = Mg_element
FEATURE [App::DocumentObjectGroupPython] B_element006  label="B_element : 006"  # scripted group (container) (typed FeaturePython)
  n = 4
  ref = B_element
FEATURE [App::DocumentObjectGroupPython] O_element061  label="O_element : 032"  # scripted group (container) (typed FeaturePython)
  n = 7
  ref = O_element
FEATURE [App::DocumentObjectGroupPython] G4_MAGNESIUM_TETRABORATE  # scripted group (container) (typed FeaturePython)
  Dunit = g/cm3
  Dvalue = 2.53
  Group = -> [Mg_element008,B_element006,O_element061]
  conduct = 2
  density = 1
  expand = 3
  formula = G4_MAGNESIUM_TETRABORATE
  name = G4_MAGNESIUM_TETRABORATE
  specific = 4
FEATURE [App::DocumentObjectGroupPython] Hg_element001  label="Hg_element : 1"  # scripted group (container) (typed FeaturePython)
  n = 1
  ref = Hg_element
FEATURE [App::DocumentObjectGroupPython] I_element004  label="I_element : 2"  # scripted group (container) (typed FeaturePython)
  n = 2
  ref = I_element
FEATURE [App::DocumentObjectGroupPython] G4_MERCURIC_IODIDE  # scripted group (container) (typed FeaturePython)
  Dunit = g/cm3
  Dvalue = 6.36
  Group = -> [Hg_element001,I_element004]
  conduct = 2
  density = 1
  expand = 3
  formula = G4_MERCURIC_IODIDE
  name = G4_MERCURIC_IODIDE
  specific = 4
FEATURE [App::DocumentObjectGroupPython] C_element059  label="C_element : 032"  # scripted group (container) (typed FeaturePython)
  n = 1
  ref = C_element
FEATURE [App::DocumentObjectGroupPython] H_element053  label="H_element : 028"  # scripted group (container) (typed FeaturePython)
  n = 4
  ref = H_element
FEATURE [App::DocumentObjectGroupPython] G4_METHANE  # scripted group (container) (typed FeaturePython)
  Dunit = g/cm3
  Dvalue = 0.000667151
  Group = -> [C_element059,H_element053]
  conduct = 2
  density = 1
  expand = 3
  formula = G4_METHANE
  name = G4_METHANE
  specific = 4
FEATURE [App::DocumentObjectGroupPython] C_element060  label="C_element : 033"  # scripted group (container) (typed FeaturePython)
  n = 1
  ref = C_element
FEATURE [App::DocumentObjectGroupPython] H_element054  label="H_element : 029"  # scripted group (container) (typed FeaturePython)
  n = 4
  ref = H_element
FEATURE [App::DocumentObjectGroupPython] O_element062  label="O_element : 033"  # scripted group (container) (typed FeaturePython)
  n = 1
  ref = O_element
FEATURE [App::DocumentObjectGroupPython] G4_METHANOL  # scripted group (container) (typed FeaturePython)
  Dunit = g/cm3
  Dvalue = 0.7914
  Group = -> [C_element060,H_element054,O_element062]
  conduct = 2
  density = 1
  expand = 3
  formula = G4_METHANOL
  name = G4_METHANOL
  specific = 4
FEATURE [App::DocumentObjectGroupPython] H_element055  label="H_element : 0.134"  # scripted group (container) (typed FeaturePython)
  n = 0.13404
FEATURE [App::DocumentObjectGroupPython] C_element061  label="C_element : 0.778"  # scripted group (container) (typed FeaturePython)
  n = 0.77796
FEATURE [App::DocumentObjectGroupPython] O_element063  label="O_element : 0.035"  # scripted group (container) (typed FeaturePython)
  n = 0.03502
FEATURE [App::DocumentObjectGroupPython] Mg_element009  label="Mg_element : 0.039"  # scripted group (container) (typed FeaturePython)
  n = 0.038594
FEATURE [App::DocumentObjectGroupPython] Ti_element002  label="Ti_element : 0.014"  # scripted group (container) (typed FeaturePython)
  n = 0.014386
FEATURE [App::DocumentObjectGroupPython] G4_MIX_D_WAX  # scripted group (container) (typed FeaturePython)
  Dunit = g/cm3
  Dvalue = 0.99
  Group = -> [H_element055,C_element061,O_element063,Mg_element009,Ti_element002]
  conduct = 2
  density = 1
  expand = 3
  formula = G4_MIX_D_WAX
  name = G4_MIX_D_WAX
  specific = 4
FEATURE [App::DocumentObjectGroupPython] H_element056  label="H_element : 0.135"  # scripted group (container) (typed FeaturePython)
  n = 0.081192
FEATURE [App::DocumentObjectGroupPython] C_element062  label="C_element : 0.583"  # scripted group (container) (typed FeaturePython)
  n = 0.583442
FEATURE [App::DocumentObjectGroupPython] N_element024  label="N_element : 0.018"  # scripted group (container) (typed FeaturePython)
  n = 0.017798
FEATURE [App::DocumentObjectGroupPython] O_element064  label="O_element : 0.186"  # scripted group (container) (typed FeaturePython)
  n = 0.186381
FEATURE [App::DocumentObjectGroupPython] Mg_element010  label="Mg_element : 0.130"  # scripted group (container) (typed FeaturePython)
  n = 0.130287
FEATURE [App::DocumentObjectGroupPython] Cl_element015  label="Cl_element : 0.588"  # scripted group (container) (typed FeaturePython)
  n = 0.0009
FEATURE [App::DocumentObjectGroupPython] G4_MS20_TISSUE  # scripted group (container) (typed FeaturePython)
  Dunit = g/cm3
  Dvalue = 1
  Group = -> [H_element056,C_element062,N_element024,O_element064,Mg_element010,Cl_element015]
  conduct = 2
  density = 1
  expand = 3
  formula = G4_MS20_TISSUE
  name = G4_MS20_TISSUE
  specific = 4
FEATURE [App::DocumentObjectGroupPython] H_element057  label="H_element : 0.136"  # scripted group (container) (typed FeaturePython)
  n = 0.102
FEATURE [App::DocumentObjectGroupPython] C_element063  label="C_element : 0.143"  # scripted group (container) (typed FeaturePython)
  n = 0.143
FEATURE [App::DocumentObjectGroupPython] N_element025  label="N_element : 0.034"  # scripted group (container) (typed FeaturePython)
  n = 0.034
FEATURE [App::DocumentObjectGroupPython] O_element065  label="O_element : 0.710"  # scripted group (container) (typed FeaturePython)
  n = 0.71
FEATURE [App::DocumentObjectGroupPython] Na_element011  label="Na_element : 0.098"  # scripted group (container) (typed FeaturePython)
  n = 0.001
FEATURE [App::DocumentObjectGroupPython] P_element007  label="P_element : 0.002"  # scripted group (container) (typed FeaturePython)
  n = 0.002
FEATURE [App::DocumentObjectGroupPython] S_element017  label="S_element : 0.018"  # scripted group (container) (typed FeaturePython)
  n = 0.003
FEATURE [App::DocumentObjectGroupPython] Cl_element016  label="Cl_element : 0.589"  # scripted group (container) (typed FeaturePython)
  n = 0.001
FEATURE [App::DocumentObjectGroupPython] K_element006  label="K_element : 0.004"  # scripted group (container) (typed FeaturePython)
  n = 0.004
FEATURE [App::DocumentObjectGroupPython] G4_MUSCLE_SKELETAL_ICRP  # scripted group (container) (typed FeaturePython)
  Dunit = g/cm3
  Dvalue = 1.05
  Group = -> [H_element057,C_element063,N_element025,O_element065,Na_element011,P_element007,S_element017,Cl_element016,K_element006]
  conduct = 2
  density = 1
  expand = 3
  formula = G4_MUSCLE_SKELETAL_ICRP
  name = G4_MUSCLE_SKELETAL_ICRP
  specific = 4
FEATURE [App::DocumentObjectGroupPython] H_element058  label="H_element : 0.137"  # scripted group (container) (typed FeaturePython)
  n = 0.102102
FEATURE [App::DocumentObjectGroupPython] C_element064  label="C_element : 0.123"  # scripted group (container) (typed FeaturePython)
  n = 0.123123
FEATURE [App::DocumentObjectGroupPython] N_element026  label="N_element : 0.756"  # scripted group (container) (typed FeaturePython)
  n = 0.035035
FEATURE [App::DocumentObjectGroupPython] O_element066  label="O_element : 0.730"  # scripted group (container) (typed FeaturePython)
  n = 0.72973
FEATURE [App::DocumentObjectGroupPython] Na_element012  label="Na_element : 0.099"  # scripted group (container) (typed FeaturePython)
  n = 0.001001
FEATURE [App::DocumentObjectGroupPython] P_element008  label="P_element : 0.106"  # scripted group (container) (typed FeaturePython)
  n = 0.002002
FEATURE [App::DocumentObjectGroupPython] S_element018  label="S_element : 0.019"  # scripted group (container) (typed FeaturePython)
  n = 0.004004
FEATURE [App::DocumentObjectGroupPython] K_element007  label="K_element : 0.016"  # scripted group (container) (typed FeaturePython)
  n = 0.003003
FEATURE [App::DocumentObjectGroupPython] G4_MUSCLE_STRIATED_ICRU  # scripted group (container) (typed FeaturePython)
  Dunit = g/cm3
  Dvalue = 1.04
  Group = -> [H_element058,C_element064,N_element026,O_element066,Na_element012,P_element008,S_element018,K_element007]
  conduct = 2
  density = 1
  expand = 3
  formula = G4_MUSCLE_STRIATED_ICRU
  name = G4_MUSCLE_STRIATED_ICRU
  specific = 4
FEATURE [App::DocumentObjectGroupPython] H_element059  label="H_element : 0.098"  # scripted group (container) (typed FeaturePython)
  n = 0.0982341
FEATURE [App::DocumentObjectGroupPython] C_element065  label="C_element : 0.156"  # scripted group (container) (typed FeaturePython)
  n = 0.156214
FEATURE [App::DocumentObjectGroupPython] N_element027  label="N_element : 0.757"  # scripted group (container) (typed FeaturePython)
  n = 0.035451
FEATURE [App::DocumentObjectGroupPython] O_element067  label="O_element : 0.880"  # scripted group (container) (typed FeaturePython)
  n = 0.710101
FEATURE [App::DocumentObjectGroupPython] G4_MUSCLE_WITH_SUCROSE  # scripted group (container) (typed FeaturePython)
  Dunit = g/cm3
  Dvalue = 1.11
  Group = -> [H_element059,C_element065,N_element027,O_element067]
  conduct = 2
  density = 1
  expand = 3
  formula = G4_MUSCLE_WITH_SUCROSE
  name = G4_MUSCLE_WITH_SUCROSE
  specific = 4
FEATURE [App::DocumentObjectGroupPython] H_element060  label="H_element : 0.138"  # scripted group (container) (typed FeaturePython)
  n = 0.101969
FEATURE [App::DocumentObjectGroupPython] C_element066  label="C_element : 0.120"  # scripted group (container) (typed FeaturePython)
  n = 0.120058
FEATURE [App::DocumentObjectGroupPython] N_element028  label="N_element : 0.758"  # scripted group (container) (typed FeaturePython)
  n = 0.035451
FEATURE [App::DocumentObjectGroupPython] O_element068  label="O_element : 0.743"  # scripted group (container) (typed FeaturePython)
  n = 0.742522
FEATURE [App::DocumentObjectGroupPython] G4_MUSCLE_WITHOUT_SUCROSE  # scripted group (container) (typed FeaturePython)
  Dunit = g/cm3
  Dvalue = 1.07
  Group = -> [H_element060,C_element066,N_element028,O_element068]
  conduct = 2
  density = 1
  expand = 3
  formula = G4_MUSCLE_WITHOUT_SUCROSE
  name = G4_MUSCLE_WITHOUT_SUCROSE
  specific = 4
FEATURE [App::DocumentObjectGroupPython] C_element067  label="C_element : 10"  # scripted group (container) (typed FeaturePython)
  n = 10
  ref = C_element
FEATURE [App::DocumentObjectGroupPython] H_element061  label="H_element : 030"  # scripted group (container) (typed FeaturePython)
  n = 8
  ref = H_element
FEATURE [App::DocumentObjectGroupPython] G4_NAPHTHALENE  # scripted group (container) (typed FeaturePython)
  Dunit = g/cm3
  Dvalue = 1.145
  Group = -> [C_element067,H_element061]
  conduct = 2
  density = 1
  expand = 3
  formula = G4_NAPHTHALENE
  name = G4_NAPHTHALENE
  specific = 4
FEATURE [App::DocumentObjectGroupPython] C_element068  label="C_element : 034"  # scripted group (container) (typed FeaturePython)
  n = 6
  ref = C_element
FEATURE [App::DocumentObjectGroupPython] H_element062  label="H_element : 031"  # scripted group (container) (typed FeaturePython)
  n = 5
  ref = H_element
FEATURE [App::DocumentObjectGroupPython] N_element029  label="N_element : 012"  # scripted group (container) (typed FeaturePython)
  n = 1
  ref = N_element
FEATURE [App::DocumentObjectGroupPython] O_element069  label="O_element : 034"  # scripted group (container) (typed FeaturePython)
  n = 2
  ref = O_element
FEATURE [App::DocumentObjectGroupPython] G4_NITROBENZENE  # scripted group (container) (typed FeaturePython)
  Dunit = g/cm3
  Dvalue = 1.19867
  Group = -> [C_element068,H_element062,N_element029,O_element069]
  conduct = 2
  density = 1
  expand = 3
  formula = G4_NITROBENZENE
  name = G4_NITROBENZENE
  specific = 4
FEATURE [App::DocumentObjectGroupPython] N_element030  label="N_element : 013"  # scripted group (container) (typed FeaturePython)
  n = 2
  ref = N_element
FEATURE [App::DocumentObjectGroupPython] O_element070  label="O_element : 035"  # scripted group (container) (typed FeaturePython)
  n = 1
  ref = O_element
FEATURE [App::DocumentObjectGroupPython] G4_NITROUS_OXIDE  # scripted group (container) (typed FeaturePython)
  Dunit = g/cm3
  Dvalue = 0.00183094
  Group = -> [N_element030,O_element070]
  conduct = 2
  density = 1
  expand = 3
  formula = G4_NITROUS_OXIDE
  name = G4_NITROUS_OXIDE
  specific = 4
FEATURE [App::DocumentObjectGroupPython] H_element063  label="H_element : 0.104"  # scripted group (container) (typed FeaturePython)
  n = 0.103509
FEATURE [App::DocumentObjectGroupPython] C_element069  label="C_element : 0.648"  # scripted group (container) (typed FeaturePython)
  n = 0.648416
FEATURE [App::DocumentObjectGroupPython] N_element031  label="N_element : 0.100"  # scripted group (container) (typed FeaturePython)
  n = 0.0995361
FEATURE [App::DocumentObjectGroupPython] O_element071  label="O_element : 0.149"  # scripted group (container) (typed FeaturePython)
  n = 0.148539
FEATURE [App::DocumentObjectGroupPython] G4_NYLON_8062  label="G4_NYLON-8062"  # scripted group (container) (typed FeaturePython)
  Dunit = g/cm3
  Dvalue = 1.08
  Group = -> [H_element063,C_element069,N_element031,O_element071]
  conduct = 2
  density = 1
  expand = 3
  formula = G4_NYLON-8062
  name = G4_NYLON-8062
  specific = 4
FEATURE [App::DocumentObjectGroupPython] C_element070  label="C_element : 035"  # scripted group (container) (typed FeaturePython)
  n = 6
  ref = C_element
FEATURE [App::DocumentObjectGroupPython] H_element064  label="H_element : 11"  # scripted group (container) (typed FeaturePython)
  n = 11
  ref = H_element
FEATURE [App::DocumentObjectGroupPython] N_element032  label="N_element : 014"  # scripted group (container) (typed FeaturePython)
  n = 1
  ref = N_element
FEATURE [App::DocumentObjectGroupPython] O_element072  label="O_element : 036"  # scripted group (container) (typed FeaturePython)
  n = 1
  ref = O_element
FEATURE [App::DocumentObjectGroupPython] G4_NYLON_6_6  label="G4_NYLON-6-6"  # scripted group (container) (typed FeaturePython)
  Dunit = g/cm3
  Dvalue = 1.14
  Group = -> [C_element070,H_element064,N_element032,O_element072]
  conduct = 2
  density = 1
  expand = 3
  formula = G4_NYLON-6-6
  name = G4_NYLON-6-6
  specific = 4
FEATURE [App::DocumentObjectGroupPython] H_element065  label="H_element : 0.139"  # scripted group (container) (typed FeaturePython)
  n = 0.107062
FEATURE [App::DocumentObjectGroupPython] C_element071  label="C_element : 0.680"  # scripted group (container) (typed FeaturePython)
  n = 0.680449
FEATURE [App::DocumentObjectGroupPython] N_element033  label="N_element : 0.099"  # scripted group (container) (typed FeaturePython)
  n = 0.099189
FEATURE [App::DocumentObjectGroupPython] O_element073  label="O_element : 0.113"  # scripted group (container) (typed FeaturePython)
  n = 0.1133
FEATURE [App::DocumentObjectGroupPython] G4_NYLON_6_10  label="G4_NYLON-6-10"  # scripted group (container) (typed FeaturePython)
  Dunit = g/cm3
  Dvalue = 1.14
  Group = -> [H_element065,C_element071,N_element033,O_element073]
  conduct = 2
  density = 1
  expand = 3
  formula = G4_NYLON-6-10
  name = G4_NYLON-6-10
  specific = 4
FEATURE [App::DocumentObjectGroupPython] H_element066  label="H_element : 0.140"  # scripted group (container) (typed FeaturePython)
  n = 0.115476
FEATURE [App::DocumentObjectGroupPython] C_element072  label="C_element : 0.721"  # scripted group (container) (typed FeaturePython)
  n = 0.720818
FEATURE [App::DocumentObjectGroupPython] N_element034  label="N_element : 0.076"  # scripted group (container) (typed FeaturePython)
  n = 0.0764169
FEATURE [App::DocumentObjectGroupPython] O_element074  label="O_element : 0.087"  # scripted group (container) (typed FeaturePython)
  n = 0.0872889
FEATURE [App::DocumentObjectGroupPython] G4_NYLON_11_RILSAN  label="G4_NYLON-11_RILSAN"  # scripted group (container) (typed FeaturePython)
  Dunit = g/cm3
  Dvalue = 1.425
  Group = -> [H_element066,C_element072,N_element034,O_element074]
  conduct = 2
  density = 1
  expand = 3
  formula = G4_NYLON-11_RILSAN
  name = G4_NYLON-11_RILSAN
  specific = 4
FEATURE [App::DocumentObjectGroupPython] C_element073  label="C_element : 8"  # scripted group (container) (typed FeaturePython)
  n = 8
  ref = C_element
FEATURE [App::DocumentObjectGroupPython] H_element067  label="H_element : 18"  # scripted group (container) (typed FeaturePython)
  n = 18
  ref = H_element
FEATURE [App::DocumentObjectGroupPython] G4_OCTANE  # scripted group (container) (typed FeaturePython)
  Dunit = g/cm3
  Dvalue = 0.7026
  Group = -> [C_element073,H_element067]
  conduct = 2
  density = 1
  expand = 3
  formula = G4_OCTANE
  name = G4_OCTANE
  specific = 4
FEATURE [App::DocumentObjectGroupPython] C_element074  label="C_element : 25"  # scripted group (container) (typed FeaturePython)
  n = 25
  ref = C_element
FEATURE [App::DocumentObjectGroupPython] H_element068  label="H_element : 52"  # scripted group (container) (typed FeaturePython)
  n = 52
  ref = H_element
FEATURE [App::DocumentObjectGroupPython] G4_PARAFFIN  # scripted group (container) (typed FeaturePython)
  Dunit = g/cm3
  Dvalue = 0.93
  Group = -> [C_element074,H_element068]
  conduct = 2
  density = 1
  expand = 3
  formula = G4_PARAFFIN
  name = G4_PARAFFIN
  specific = 4
FEATURE [App::DocumentObjectGroupPython] C_element075  label="C_element : 036"  # scripted group (container) (typed FeaturePython)
  n = 5
  ref = C_element
FEATURE [App::DocumentObjectGroupPython] H_element069  label="H_element : 032"  # scripted group (container) (typed FeaturePython)
  n = 12
  ref = H_element
FEATURE [App::DocumentObjectGroupPython] G4_N_PENTANE  label="G4_N-PENTANE"  # scripted group (container) (typed FeaturePython)
  Dunit = g/cm3
  Dvalue = 0.6262
  Group = -> [C_element075,H_element069]
  conduct = 2
  density = 1
  expand = 3
  formula = G4_N-PENTANE
  name = G4_N-PENTANE
  specific = 4
FEATURE [App::DocumentObjectGroupPython] H_element070  label="H_element : 0.014"  # scripted group (container) (typed FeaturePython)
  n = 0.0141
FEATURE [App::DocumentObjectGroupPython] C_element076  label="C_element : 0.072"  # scripted group (container) (typed FeaturePython)
  n = 0.072261
FEATURE [App::DocumentObjectGroupPython] N_element035  label="N_element : 0.019"  # scripted group (container) (typed FeaturePython)
  n = 0.01932
FEATURE [App::DocumentObjectGroupPython] O_element075  label="O_element : 0.066"  # scripted group (container) (typed FeaturePython)
  n = 0.066101
FEATURE [App::DocumentObjectGroupPython] S_element019  label="S_element : 0.020"  # scripted group (container) (typed FeaturePython)
  n = 0.00189
FEATURE [App::DocumentObjectGroupPython] Br_element004  label="Br_element : 0.349"  # scripted group (container) (typed FeaturePython)
  n = 0.349103
FEATURE [App::DocumentObjectGroupPython] Ag_element001  label="Ag_element : 0.474"  # scripted group (container) (typed FeaturePython)
  n = 0.474105
FEATURE [App::DocumentObjectGroupPython] I_element005  label="I_element : 0.003"  # scripted group (container) (typed FeaturePython)
  n = 0.00312
FEATURE [App::DocumentObjectGroupPython] G4_PHOTO_EMULSION  # scripted group (container) (typed FeaturePython)
  Dunit = g/cm3
  Dvalue = 3.815
  Group = -> [H_element070,C_element076,N_element035,O_element075,S_element019,Br_element004,Ag_element001,I_element005]
  conduct = 2
  density = 1
  expand = 3
  formula = G4_PHOTO_EMULSION
  name = G4_PHOTO_EMULSION
  specific = 4
FEATURE [App::DocumentObjectGroupPython] C_element077  label="C_element : 9"  # scripted group (container) (typed FeaturePython)
  n = 9
  ref = C_element
FEATURE [App::DocumentObjectGroupPython] H_element071  label="H_element : 033"  # scripted group (container) (typed FeaturePython)
  n = 10
  ref = H_element
FEATURE [App::DocumentObjectGroupPython] G4_PLASTIC_SC_VINYLTOLUENE  # scripted group (container) (typed FeaturePython)
  Dunit = g/cm3
  Dvalue = 1.032
  Group = -> [C_element077,H_element071]
  conduct = 2
  density = 1
  expand = 3
  formula = G4_PLASTIC_SC_VINYLTOLUENE
  name = G4_PLASTIC_SC_VINYLTOLUENE
  specific = 4
FEATURE [App::DocumentObjectGroupPython] Pu_element001  label="Pu_element : 1"  # scripted group (container) (typed FeaturePython)
  n = 1
  ref = Pu_element
FEATURE [App::DocumentObjectGroupPython] O_element076  label="O_element : 037"  # scripted group (container) (typed FeaturePython)
  n = 2
  ref = O_element
FEATURE [App::DocumentObjectGroupPython] G4_PLUTONIUM_DIOXIDE  # scripted group (container) (typed FeaturePython)
  Dunit = g/cm3
  Dvalue = 11.46
  Group = -> [Pu_element001,O_element076]
  conduct = 2
  density = 1
  expand = 3
  formula = G4_PLUTONIUM_DIOXIDE
  name = G4_PLUTONIUM_DIOXIDE
  specific = 4
FEATURE [App::DocumentObjectGroupPython] C_element078  label="C_element : 037"  # scripted group (container) (typed FeaturePython)
  n = 3
  ref = C_element
FEATURE [App::DocumentObjectGroupPython] H_element072  label="H_element : 034"  # scripted group (container) (typed FeaturePython)
  n = 3
  ref = H_element
FEATURE [App::DocumentObjectGroupPython] N_element036  label="N_element : 015"  # scripted group (container) (typed FeaturePython)
  n = 1
  ref = N_element
FEATURE [App::DocumentObjectGroupPython] G4_POLYACRYLONITRILE  # scripted group (container) (typed FeaturePython)
  Dunit = g/cm3
  Dvalue = 1.17
  Group = -> [C_element078,H_element072,N_element036]
  conduct = 2
  density = 1
  expand = 3
  formula = G4_POLYACRYLONITRILE
  name = G4_POLYACRYLONITRILE
  specific = 4
FEATURE [App::DocumentObjectGroupPython] C_element079  label="C_element : 16"  # scripted group (container) (typed FeaturePython)
  n = 16
  ref = C_element
FEATURE [App::DocumentObjectGroupPython] H_element073  label="H_element : 035"  # scripted group (container) (typed FeaturePython)
  n = 14
  ref = H_element
FEATURE [App::DocumentObjectGroupPython] O_element077  label="O_element : 038"  # scripted group (container) (typed FeaturePython)
  n = 3
  ref = O_element
FEATURE [App::DocumentObjectGroupPython] G4_POLYCARBONATE  # scripted group (container) (typed FeaturePython)
  Dunit = g/cm3
  Dvalue = 1.2
  Group = -> [C_element079,H_element073,O_element077]
  conduct = 2
  density = 1
  expand = 3
  formula = G4_POLYCARBONATE
  name = G4_POLYCARBONATE
  specific = 4
FEATURE [App::DocumentObjectGroupPython] C_element080  label="C_element : 038"  # scripted group (container) (typed FeaturePython)
  n = 8
  ref = C_element
FEATURE [App::DocumentObjectGroupPython] H_element074  label="H_element : 036"  # scripted group (container) (typed FeaturePython)
  n = 7
  ref = H_element
FEATURE [App::DocumentObjectGroupPython] Cl_element017  label="Cl_element : 007"  # scripted group (container) (typed FeaturePython)
  n = 1
  ref = Cl_element
FEATURE [App::DocumentObjectGroupPython] G4_POLYCHLOROSTYRENE  # scripted group (container) (typed FeaturePython)
  Dunit = g/cm3
  Dvalue = 1.3
  Group = -> [C_element080,H_element074,Cl_element017]
  conduct = 2
  density = 1
  expand = 3
  formula = G4_POLYCHLOROSTYRENE
  name = G4_POLYCHLOROSTYRENE
  specific = 4
FEATURE [App::DocumentObjectGroupPython] C_element081  label="C_element : 039"  # scripted group (container) (typed FeaturePython)
  n = 1
  ref = C_element
FEATURE [App::DocumentObjectGroupPython] H_element075  label="H_element : 037"  # scripted group (container) (typed FeaturePython)
  n = 2
  ref = H_element
FEATURE [App::DocumentObjectGroupPython] G4_POLYETHYLENE  # scripted group (container) (typed FeaturePython)
  Dunit = g/cm3
  Dvalue = 0.94
  Group = -> [C_element081,H_element075]
  conduct = 2
  density = 1
  expand = 3
  formula = G4_POLYETHYLENE
  name = G4_POLYETHYLENE
  specific = 4
FEATURE [App::DocumentObjectGroupPython] C_element082  label="C_element : 040"  # scripted group (container) (typed FeaturePython)
  n = 10
  ref = C_element
FEATURE [App::DocumentObjectGroupPython] H_element076  label="H_element : 038"  # scripted group (container) (typed FeaturePython)
  n = 8
  ref = H_element
FEATURE [App::DocumentObjectGroupPython] O_element078  label="O_element : 039"  # scripted group (container) (typed FeaturePython)
  n = 4
  ref = O_element
FEATURE [App::DocumentObjectGroupPython] G4_MYLAR  # scripted group (container) (typed FeaturePython)
  Dunit = g/cm3
  Dvalue = 1.4
  Group = -> [C_element082,H_element076,O_element078]
  conduct = 2
  density = 1
  expand = 3
  formula = G4_MYLAR
  name = G4_MYLAR
  specific = 4
FEATURE [App::DocumentObjectGroupPython] C_element083  label="C_element : 041"  # scripted group (container) (typed FeaturePython)
  n = 5
  ref = C_element
FEATURE [App::DocumentObjectGroupPython] H_element077  label="H_element : 039"  # scripted group (container) (typed FeaturePython)
  n = 8
  ref = H_element
FEATURE [App::DocumentObjectGroupPython] O_element079  label="O_element : 040"  # scripted group (container) (typed FeaturePython)
  n = 2
  ref = O_element
FEATURE [App::DocumentObjectGroupPython] G4_PLEXIGLASS  # scripted group (container) (typed FeaturePython)
  Dunit = g/cm3
  Dvalue = 1.19
  Group = -> [C_element083,H_element077,O_element079]
  conduct = 2
  density = 1
  expand = 3
  formula = G4_PLEXIGLASS
  name = G4_PLEXIGLASS
  specific = 4
FEATURE [App::DocumentObjectGroupPython] C_element084  label="C_element : 042"  # scripted group (container) (typed FeaturePython)
  n = 1
  ref = C_element
FEATURE [App::DocumentObjectGroupPython] H_element078  label="H_element : 040"  # scripted group (container) (typed FeaturePython)
  n = 2
  ref = H_element
FEATURE [App::DocumentObjectGroupPython] O_element080  label="O_element : 041"  # scripted group (container) (typed FeaturePython)
  n = 1
  ref = O_element
FEATURE [App::DocumentObjectGroupPython] G4_POLYOXYMETHYLENE  # scripted group (container) (typed FeaturePython)
  Dunit = g/cm3
  Dvalue = 1.425
  Group = -> [C_element084,H_element078,O_element080]
  conduct = 2
  density = 1
  expand = 3
  formula = G4_POLYOXYMETHYLENE
  name = G4_POLYOXYMETHYLENE
  specific = 4
FEATURE [App::DocumentObjectGroupPython] C_element085  label="C_element : 043"  # scripted group (container) (typed FeaturePython)
  n = 2
  ref = C_element
FEATURE [App::DocumentObjectGroupPython] H_element079  label="H_element : 041"  # scripted group (container) (typed FeaturePython)
  n = 4
  ref = H_element
FEATURE [App::DocumentObjectGroupPython] G4_POLYPROPYLENE  # scripted group (container) (typed FeaturePython)
  Dunit = g/cm3
  Dvalue = 0.9
  Group = -> [C_element085,H_element079]
  conduct = 2
  density = 1
  expand = 3
  formula = G4_POLYPROPYLENE
  name = G4_POLYPROPYLENE
  specific = 4
FEATURE [App::DocumentObjectGroupPython] C_element086  label="C_element : 044"  # scripted group (container) (typed FeaturePython)
  n = 8
  ref = C_element
FEATURE [App::DocumentObjectGroupPython] H_element080  label="H_element : 042"  # scripted group (container) (typed FeaturePython)
  n = 8
  ref = H_element
FEATURE [App::DocumentObjectGroupPython] G4_POLYSTYRENE  # scripted group (container) (typed FeaturePython)
  Dunit = g/cm3
  Dvalue = 1.06
  Group = -> [C_element086,H_element080]
  conduct = 2
  density = 1
  expand = 3
  formula = G4_POLYSTYRENE
  name = G4_POLYSTYRENE
  specific = 4
FEATURE [App::DocumentObjectGroupPython] C_element087  label="C_element : 045"  # scripted group (container) (typed FeaturePython)
  n = 2
  ref = C_element
FEATURE [App::DocumentObjectGroupPython] F_element014  label="F_element : 4"  # scripted group (container) (typed FeaturePython)
  n = 4
  ref = F_element
FEATURE [App::DocumentObjectGroupPython] G4_TEFLON  # scripted group (container) (typed FeaturePython)
  Dunit = g/cm3
  Dvalue = 2.2
  Group = -> [C_element087,F_element014]
  conduct = 2
  density = 1
  expand = 3
  formula = G4_TEFLON
  name = G4_TEFLON
  specific = 4
FEATURE [App::DocumentObjectGroupPython] C_element088  label="C_element : 046"  # scripted group (container) (typed FeaturePython)
  n = 2
  ref = C_element
FEATURE [App::DocumentObjectGroupPython] F_element015  label="F_element : 006"  # scripted group (container) (typed FeaturePython)
  n = 3
  ref = F_element
FEATURE [App::DocumentObjectGroupPython] Cl_element018  label="Cl_element : 008"  # scripted group (container) (typed FeaturePython)
  n = 1
  ref = Cl_element
FEATURE [App::DocumentObjectGroupPython] G4_POLYTRIFLUOROCHLOROETHYLENE  # scripted group (container) (typed FeaturePython)
  Dunit = g/cm3
  Dvalue = 2.1
  Group = -> [C_element088,F_element015,Cl_element018]
  conduct = 2
  density = 1
  expand = 3
  formula = G4_POLYTRIFLUOROCHLOROETHYLENE
  name = G4_POLYTRIFLUOROCHLOROETHYLENE
  specific = 4
FEATURE [App::DocumentObjectGroupPython] C_element089  label="C_element : 047"  # scripted group (container) (typed FeaturePython)
  n = 4
  ref = C_element
FEATURE [App::DocumentObjectGroupPython] H_element081  label="H_element : 043"  # scripted group (container) (typed FeaturePython)
  n = 6
  ref = H_element
FEATURE [App::DocumentObjectGroupPython] O_element081  label="O_element : 042"  # scripted group (container) (typed FeaturePython)
  n = 2
  ref = O_element
FEATURE [App::DocumentObjectGroupPython] G4_POLYVINYL_ACETATE  # scripted group (container) (typed FeaturePython)
  Dunit = g/cm3
  Dvalue = 1.19
  Group = -> [C_element089,H_element081,O_element081]
  conduct = 2
  density = 1
  expand = 3
  formula = G4_POLYVINYL_ACETATE
  name = G4_POLYVINYL_ACETATE
  specific = 4
FEATURE [App::DocumentObjectGroupPython] C_element090  label="C_element : 048"  # scripted group (container) (typed FeaturePython)
  n = 2
  ref = C_element
FEATURE [App::DocumentObjectGroupPython] H_element082  label="H_element : 044"  # scripted group (container) (typed FeaturePython)
  n = 4
  ref = H_element
FEATURE [App::DocumentObjectGroupPython] O_element082  label="O_element : 043"  # scripted group (container) (typed FeaturePython)
  n = 1
  ref = O_element
FEATURE [App::DocumentObjectGroupPython] G4_POLYVINYL_ALCOHOL  # scripted group (container) (typed FeaturePython)
  Dunit = g/cm3
  Dvalue = 1.3
  Group = -> [C_element090,H_element082,O_element082]
  conduct = 2
  density = 1
  expand = 3
  formula = G4_POLYVINYL_ALCOHOL
  name = G4_POLYVINYL_ALCOHOL
  specific = 4
FEATURE [App::DocumentObjectGroupPython] C_element091  label="C_element : 049"  # scripted group (container) (typed FeaturePython)
  n = 8
  ref = C_element
FEATURE [App::DocumentObjectGroupPython] H_element083  label="H_element : 045"  # scripted group (container) (typed FeaturePython)
  n = 14
  ref = H_element
FEATURE [App::DocumentObjectGroupPython] O_element083  label="O_element : 044"  # scripted group (container) (typed FeaturePython)
  n = 2
  ref = O_element
FEATURE [App::DocumentObjectGroupPython] G4_POLYVINYL_BUTYRAL  # scripted group (container) (typed FeaturePython)
  Dunit = g/cm3
  Dvalue = 1.12
  Group = -> [C_element091,H_element083,O_element083]
  conduct = 2
  density = 1
  expand = 3
  formula = G4_POLYVINYL_BUTYRAL
  name = G4_POLYVINYL_BUTYRAL
  specific = 4
FEATURE [App::DocumentObjectGroupPython] C_element092  label="C_element : 050"  # scripted group (container) (typed FeaturePython)
  n = 2
  ref = C_element
FEATURE [App::DocumentObjectGroupPython] H_element084  label="H_element : 046"  # scripted group (container) (typed FeaturePython)
  n = 3
  ref = H_element
FEATURE [App::DocumentObjectGroupPython] Cl_element019  label="Cl_element : 009"  # scripted group (container) (typed FeaturePython)
  n = 1
  ref = Cl_element
FEATURE [App::DocumentObjectGroupPython] G4_POLYVINYL_CHLORIDE  # scripted group (container) (typed FeaturePython)
  Dunit = g/cm3
  Dvalue = 1.3
  Group = -> [C_element092,H_element084,Cl_element019]
  conduct = 2
  density = 1
  expand = 3
  formula = G4_POLYVINYL_CHLORIDE
  name = G4_POLYVINYL_CHLORIDE
  specific = 4
FEATURE [App::DocumentObjectGroupPython] C_element093  label="C_element : 051"  # scripted group (container) (typed FeaturePython)
  n = 2
  ref = C_element
FEATURE [App::DocumentObjectGroupPython] H_element085  label="H_element : 047"  # scripted group (container) (typed FeaturePython)
  n = 2
  ref = H_element
FEATURE [App::DocumentObjectGroupPython] Cl_element020  label="Cl_element : 010"  # scripted group (container) (typed FeaturePython)
  n = 2
  ref = Cl_element
FEATURE [App::DocumentObjectGroupPython] G4_POLYVINYLIDENE_CHLORIDE  # scripted group (container) (typed FeaturePython)
  Dunit = g/cm3
  Dvalue = 1.7
  Group = -> [C_element093,H_element085,Cl_element020]
  conduct = 2
  density = 1
  expand = 3
  formula = G4_POLYVINYLIDENE_CHLORIDE
  name = G4_POLYVINYLIDENE_CHLORIDE
  specific = 4
FEATURE [App::DocumentObjectGroupPython] C_element094  label="C_element : 052"  # scripted group (container) (typed FeaturePython)
  n = 2
  ref = C_element
FEATURE [App::DocumentObjectGroupPython] H_element086  label="H_element : 048"  # scripted group (container) (typed FeaturePython)
  n = 2
  ref = H_element
FEATURE [App::DocumentObjectGroupPython] F_element016  label="F_element : 007"  # scripted group (container) (typed FeaturePython)
  n = 2
  ref = F_element
FEATURE [App::DocumentObjectGroupPython] G4_POLYVINYLIDENE_FLUORIDE  # scripted group (container) (typed FeaturePython)
  Dunit = g/cm3
  Dvalue = 1.76
  Group = -> [C_element094,H_element086,F_element016]
  conduct = 2
  density = 1
  expand = 3
  formula = G4_POLYVINYLIDENE_FLUORIDE
  name = G4_POLYVINYLIDENE_FLUORIDE
  specific = 4
FEATURE [App::DocumentObjectGroupPython] C_element095  label="C_element : 053"  # scripted group (container) (typed FeaturePython)
  n = 6
  ref = C_element
FEATURE [App::DocumentObjectGroupPython] H_element087  label="H_element : 9"  # scripted group (container) (typed FeaturePython)
  n = 9
  ref = H_element
FEATURE [App::DocumentObjectGroupPython] N_element037  label="N_element : 016"  # scripted group (container) (typed FeaturePython)
  n = 1
  ref = N_element
FEATURE [App::DocumentObjectGroupPython] O_element084  label="O_element : 045"  # scripted group (container) (typed FeaturePython)
  n = 1
  ref = O_element
FEATURE [App::DocumentObjectGroupPython] G4_POLYVINYL_PYRROLIDONE  # scripted group (container) (typed FeaturePython)
  Dunit = g/cm3
  Dvalue = 1.25
  Group = -> [C_element095,H_element087,N_element037,O_element084]
  conduct = 2
  density = 1
  expand = 3
  formula = G4_POLYVINYL_PYRROLIDONE
  name = G4_POLYVINYL_PYRROLIDONE
  specific = 4
FEATURE [App::DocumentObjectGroupPython] K_element008  label="K_element : 1"  # scripted group (container) (typed FeaturePython)
  n = 1
  ref = K_element
FEATURE [App::DocumentObjectGroupPython] I_element006  label="I_element : 003"  # scripted group (container) (typed FeaturePython)
  n = 1
  ref = I_element
FEATURE [App::DocumentObjectGroupPython] G4_POTASSIUM_IODIDE  # scripted group (container) (typed FeaturePython)
  Dunit = g/cm3
  Dvalue = 3.13
  Group = -> [K_element008,I_element006]
  conduct = 2
  density = 1
  expand = 3
  formula = G4_POTASSIUM_IODIDE
  name = G4_POTASSIUM_IODIDE
  specific = 4
FEATURE [App::DocumentObjectGroupPython] K_element009  label="K_element : 2"  # scripted group (container) (typed FeaturePython)
  n = 2
  ref = K_element
FEATURE [App::DocumentObjectGroupPython] O_element085  label="O_element : 046"  # scripted group (container) (typed FeaturePython)
  n = 1
  ref = O_element
FEATURE [App::DocumentObjectGroupPython] G4_POTASSIUM_OXIDE  # scripted group (container) (typed FeaturePython)
  Dunit = g/cm3
  Dvalue = 2.32
  Group = -> [K_element009,O_element085]
  conduct = 2
  density = 1
  expand = 3
  formula = G4_POTASSIUM_OXIDE
  name = G4_POTASSIUM_OXIDE
  specific = 4
FEATURE [App::DocumentObjectGroupPython] C_element096  label="C_element : 054"  # scripted group (container) (typed FeaturePython)
  n = 3
  ref = C_element
FEATURE [App::DocumentObjectGroupPython] H_element088  label="H_element : 049"  # scripted group (container) (typed FeaturePython)
  n = 8
  ref = H_element
FEATURE [App::DocumentObjectGroupPython] G4_PROPANE  # scripted group (container) (typed FeaturePython)
  Dunit = g/cm3
  Dvalue = 0.00187939
  Group = -> [C_element096,H_element088]
  conduct = 2
  density = 1
  expand = 3
  formula = G4_PROPANE
  name = G4_PROPANE
  specific = 4
FEATURE [App::DocumentObjectGroupPython] C_element097  label="C_element : 055"  # scripted group (container) (typed FeaturePython)
  n = 3
  ref = C_element
FEATURE [App::DocumentObjectGroupPython] H_element089  label="H_element : 050"  # scripted group (container) (typed FeaturePython)
  n = 8
  ref = H_element
FEATURE [App::DocumentObjectGroupPython] G4_lPROPANE  # scripted group (container) (typed FeaturePython)
  Dunit = g/cm3
  Dvalue = 0.43
  Group = -> [C_element097,H_element089]
  conduct = 2
  density = 1
  expand = 3
  formula = G4_lPROPANE
  name = G4_lPROPANE
  specific = 4
FEATURE [App::DocumentObjectGroupPython] C_element098  label="C_element : 056"  # scripted group (container) (typed FeaturePython)
  n = 3
  ref = C_element
FEATURE [App::DocumentObjectGroupPython] H_element090  label="H_element : 051"  # scripted group (container) (typed FeaturePython)
  n = 8
  ref = H_element
FEATURE [App::DocumentObjectGroupPython] O_element086  label="O_element : 047"  # scripted group (container) (typed FeaturePython)
  n = 1
  ref = O_element
FEATURE [App::DocumentObjectGroupPython] G4_N_PROPYL_ALCOHOL  label="G4_N-PROPYL_ALCOHOL"  # scripted group (container) (typed FeaturePython)
  Dunit = g/cm3
  Dvalue = 0.8035
  Group = -> [C_element098,H_element090,O_element086]
  conduct = 2
  density = 1
  expand = 3
  formula = G4_N-PROPYL_ALCOHOL
  name = G4_N-PROPYL_ALCOHOL
  specific = 4
FEATURE [App::DocumentObjectGroupPython] C_element099  label="C_element : 057"  # scripted group (container) (typed FeaturePython)
  n = 5
  ref = C_element
FEATURE [App::DocumentObjectGroupPython] H_element091  label="H_element : 052"  # scripted group (container) (typed FeaturePython)
  n = 5
  ref = H_element
FEATURE [App::DocumentObjectGroupPython] N_element038  label="N_element : 017"  # scripted group (container) (typed FeaturePython)
  n = 1
  ref = N_element
FEATURE [App::DocumentObjectGroupPython] G4_PYRIDINE  # scripted group (container) (typed FeaturePython)
  Dunit = g/cm3
  Dvalue = 0.9819
  Group = -> [C_element099,H_element091,N_element038]
  conduct = 2
  density = 1
  expand = 3
  formula = G4_PYRIDINE
  name = G4_PYRIDINE
  specific = 4
FEATURE [App::DocumentObjectGroupPython] H_element092  label="H_element : 0.144"  # scripted group (container) (typed FeaturePython)
  n = 0.143711
FEATURE [App::DocumentObjectGroupPython] C_element100  label="C_element : 0.856"  # scripted group (container) (typed FeaturePython)
  n = 0.856289
FEATURE [App::DocumentObjectGroupPython] G4_RUBBER_BUTYL  # scripted group (container) (typed FeaturePython)
  Dunit = g/cm3
  Dvalue = 0.92
  Group = -> [H_element092,C_element100]
  conduct = 2
  density = 1
  expand = 3
  formula = G4_RUBBER_BUTYL
  name = G4_RUBBER_BUTYL
  specific = 4
FEATURE [App::DocumentObjectGroupPython] H_element093  label="H_element : 0.118"  # scripted group (container) (typed FeaturePython)
  n = 0.118371
FEATURE [App::DocumentObjectGroupPython] C_element101  label="C_element : 0.882"  # scripted group (container) (typed FeaturePython)
  n = 0.881629
FEATURE [App::DocumentObjectGroupPython] G4_RUBBER_NATURAL  # scripted group (container) (typed FeaturePython)
  Dunit = g/cm3
  Dvalue = 0.92
  Group = -> [H_element093,C_element101]
  conduct = 2
  density = 1
  expand = 3
  formula = G4_RUBBER_NATURAL
  name = G4_RUBBER_NATURAL
  specific = 4
FEATURE [App::DocumentObjectGroupPython] H_element094  label="H_element : 0.145"  # scripted group (container) (typed FeaturePython)
  n = 0.05692
FEATURE [App::DocumentObjectGroupPython] C_element102  label="C_element : 0.543"  # scripted group (container) (typed FeaturePython)
  n = 0.542646
FEATURE [App::DocumentObjectGroupPython] Cl_element021  label="Cl_element : 0.400"  # scripted group (container) (typed FeaturePython)
  n = 0.400434
FEATURE [App::DocumentObjectGroupPython] G4_RUBBER_NEOPRENE  # scripted group (container) (typed FeaturePython)
  Dunit = g/cm3
  Dvalue = 1.23
  Group = -> [H_element094,C_element102,Cl_element021]
  conduct = 2
  density = 1
  expand = 3
  formula = G4_RUBBER_NEOPRENE
  name = G4_RUBBER_NEOPRENE
  specific = 4
FEATURE [App::DocumentObjectGroupPython] Si_element006  label="Si_element : 1"  # scripted group (container) (typed FeaturePython)
  n = 1
  ref = Si_element
FEATURE [App::DocumentObjectGroupPython] O_element087  label="O_element : 048"  # scripted group (container) (typed FeaturePython)
  n = 2
  ref = O_element
FEATURE [App::DocumentObjectGroupPython] G4_SILICON_DIOXIDE  # scripted group (container) (typed FeaturePython)
  Dunit = g/cm3
  Dvalue = 2.32
  Group = -> [Si_element006,O_element087]
  conduct = 2
  density = 1
  expand = 3
  formula = G4_SILICON_DIOXIDE
  name = G4_SILICON_DIOXIDE
  specific = 4
FEATURE [App::DocumentObjectGroupPython] Ag_element002  label="Ag_element : 1"  # scripted group (container) (typed FeaturePython)
  n = 1
  ref = Ag_element
FEATURE [App::DocumentObjectGroupPython] Br_element005  label="Br_element : 003"  # scripted group (container) (typed FeaturePython)
  n = 1
  ref = Br_element
FEATURE [App::DocumentObjectGroupPython] G4_SILVER_BROMIDE  # scripted group (container) (typed FeaturePython)
  Dunit = g/cm3
  Dvalue = 6.473
  Group = -> [Ag_element002,Br_element005]
  conduct = 2
  density = 1
  expand = 3
  formula = G4_SILVER_BROMIDE
  name = G4_SILVER_BROMIDE
  specific = 4
FEATURE [App::DocumentObjectGroupPython] Ag_element003  label="Ag_element : 002"  # scripted group (container) (typed FeaturePython)
  n = 1
  ref = Ag_element
FEATURE [App::DocumentObjectGroupPython] Cl_element022  label="Cl_element : 011"  # scripted group (container) (typed FeaturePython)
  n = 1
  ref = Cl_element
FEATURE [App::DocumentObjectGroupPython] G4_SILVER_CHLORIDE  # scripted group (container) (typed FeaturePython)
  Dunit = g/cm3
  Dvalue = 5.56
  Group = -> [Ag_element003,Cl_element022]
  conduct = 2
  density = 1
  expand = 3
  formula = G4_SILVER_CHLORIDE
  name = G4_SILVER_CHLORIDE
  specific = 4
FEATURE [App::DocumentObjectGroupPython] Br_element006  label="Br_element : 0.423"  # scripted group (container) (typed FeaturePython)
  n = 0.422895
FEATURE [App::DocumentObjectGroupPython] Ag_element004  label="Ag_element : 0.574"  # scripted group (container) (typed FeaturePython)
  n = 0.573748
FEATURE [App::DocumentObjectGroupPython] I_element007  label="I_element : 0.649"  # scripted group (container) (typed FeaturePython)
  n = 0.003357
FEATURE [App::DocumentObjectGroupPython] G4_SILVER_HALIDES  # scripted group (container) (typed FeaturePython)
  Dunit = g/cm3
  Dvalue = 6.47
  Group = -> [Br_element006,Ag_element004,I_element007]
  conduct = 2
  density = 1
  expand = 3
  formula = G4_SILVER_HALIDES
  name = G4_SILVER_HALIDES
  specific = 4
FEATURE [App::DocumentObjectGroupPython] Ag_element005  label="Ag_element : 003"  # scripted group (container) (typed FeaturePython)
  n = 1
  ref = Ag_element
FEATURE [App::DocumentObjectGroupPython] I_element008  label="I_element : 004"  # scripted group (container) (typed FeaturePython)
  n = 1
  ref = I_element
FEATURE [App::DocumentObjectGroupPython] G4_SILVER_IODIDE  # scripted group (container) (typed FeaturePython)
  Dunit = g/cm3
  Dvalue = 6.01
  Group = -> [Ag_element005,I_element008]
  conduct = 2
  density = 1
  expand = 3
  formula = G4_SILVER_IODIDE
  name = G4_SILVER_IODIDE
  specific = 4
FEATURE [App::DocumentObjectGroupPython] H_element095  label="H_element : 0.100"  # scripted group (container) (typed FeaturePython)
  n = 0.1
FEATURE [App::DocumentObjectGroupPython] C_element103  label="C_element : 0.204"  # scripted group (container) (typed FeaturePython)
  n = 0.204
FEATURE [App::DocumentObjectGroupPython] N_element039  label="N_element : 0.759"  # scripted group (container) (typed FeaturePython)
  n = 0.042
FEATURE [App::DocumentObjectGroupPython] O_element088  label="O_element : 0.645"  # scripted group (container) (typed FeaturePython)
  n = 0.645
FEATURE [App::DocumentObjectGroupPython] Na_element013  label="Na_element : 0.100"  # scripted group (container) (typed FeaturePython)
  n = 0.002
FEATURE [App::DocumentObjectGroupPython] P_element009  label="P_element : 0.107"  # scripted group (container) (typed FeaturePython)
  n = 0.001
FEATURE [App::DocumentObjectGroupPython] S_element020  label="S_element : 0.021"  # scripted group (container) (typed FeaturePython)
  n = 0.002
FEATURE [App::DocumentObjectGroupPython] Cl_element023  label="Cl_element : 0.590"  # scripted group (container) (typed FeaturePython)
  n = 0.003
FEATURE [App::DocumentObjectGroupPython] K_element010  label="K_element : 0.001"  # scripted group (container) (typed FeaturePython)
  n = 0.001
FEATURE [App::DocumentObjectGroupPython] G4_SKIN_ICRP  # scripted group (container) (typed FeaturePython)
  Dunit = g/cm3
  Dvalue = 1.09
  Group = -> [H_element095,C_element103,N_element039,O_element088,Na_element013,P_element009,S_element020,Cl_element023,K_element010]
  conduct = 2
  density = 1
  expand = 3
  formula = G4_SKIN_ICRP
  name = G4_SKIN_ICRP
  specific = 4
FEATURE [App::DocumentObjectGroupPython] Na_element014  label="Na_element : 2"  # scripted group (container) (typed FeaturePython)
  n = 2
  ref = Na_element
FEATURE [App::DocumentObjectGroupPython] C_element104  label="C_element : 058"  # scripted group (container) (typed FeaturePython)
  n = 1
  ref = C_element
FEATURE [App::DocumentObjectGroupPython] O_element089  label="O_element : 049"  # scripted group (container) (typed FeaturePython)
  n = 3
  ref = O_element
FEATURE [App::DocumentObjectGroupPython] G4_SODIUM_CARBONATE  # scripted group (container) (typed FeaturePython)
  Dunit = g/cm3
  Dvalue = 2.532
  Group = -> [Na_element014,C_element104,O_element089]
  conduct = 2
  density = 1
  expand = 3
  formula = G4_SODIUM_CARBONATE
  name = G4_SODIUM_CARBONATE
  specific = 4
FEATURE [App::DocumentObjectGroupPython] Na_element015  label="Na_element : 1"  # scripted group (container) (typed FeaturePython)
  n = 1
  ref = Na_element
FEATURE [App::DocumentObjectGroupPython] I_element009  label="I_element : 005"  # scripted group (container) (typed FeaturePython)
  n = 1
  ref = I_element
FEATURE [App::DocumentObjectGroupPython] G4_SODIUM_IODIDE  # scripted group (container) (typed FeaturePython)
  Dunit = g/cm3
  Dvalue = 3.667
  Group = -> [Na_element015,I_element009]
  conduct = 2
  density = 1
  expand = 3
  formula = G4_SODIUM_IODIDE
  name = G4_SODIUM_IODIDE
  specific = 4
FEATURE [App::DocumentObjectGroupPython] Na_element016  label="Na_element : 003"  # scripted group (container) (typed FeaturePython)
  n = 2
  ref = Na_element
FEATURE [App::DocumentObjectGroupPython] O_element090  label="O_element : 050"  # scripted group (container) (typed FeaturePython)
  n = 1
  ref = O_element
FEATURE [App::DocumentObjectGroupPython] G4_SODIUM_MONOXIDE  # scripted group (container) (typed FeaturePython)
  Dunit = g/cm3
  Dvalue = 2.27
  Group = -> [Na_element016,O_element090]
  conduct = 2
  density = 1
  expand = 3
  formula = G4_SODIUM_MONOXIDE
  name = G4_SODIUM_MONOXIDE
  specific = 4
FEATURE [App::DocumentObjectGroupPython] Na_element017  label="Na_element : 004"  # scripted group (container) (typed FeaturePython)
  n = 1
  ref = Na_element
FEATURE [App::DocumentObjectGroupPython] N_element040  label="N_element : 018"  # scripted group (container) (typed FeaturePython)
  n = 1
  ref = N_element
FEATURE [App::DocumentObjectGroupPython] O_element091  label="O_element : 051"  # scripted group (container) (typed FeaturePython)
  n = 3
  ref = O_element
FEATURE [App::DocumentObjectGroupPython] G4_SODIUM_NITRATE  # scripted group (container) (typed FeaturePython)
  Dunit = g/cm3
  Dvalue = 2.261
  Group = -> [Na_element017,N_element040,O_element091]
  conduct = 2
  density = 1
  expand = 3
  formula = G4_SODIUM_NITRATE
  name = G4_SODIUM_NITRATE
  specific = 4
FEATURE [App::DocumentObjectGroupPython] C_element105  label="C_element : 059"  # scripted group (container) (typed FeaturePython)
  n = 14
  ref = C_element
FEATURE [App::DocumentObjectGroupPython] H_element096  label="H_element : 053"  # scripted group (container) (typed FeaturePython)
  n = 12
  ref = H_element
FEATURE [App::DocumentObjectGroupPython] G4_STILBENE  # scripted group (container) (typed FeaturePython)
  Dunit = g/cm3
  Dvalue = 0.9707
  Group = -> [C_element105,H_element096]
  conduct = 2
  density = 1
  expand = 3
  formula = G4_STILBENE
  name = G4_STILBENE
  specific = 4
FEATURE [App::DocumentObjectGroupPython] C_element106  label="C_element : 12"  # scripted group (container) (typed FeaturePython)
  n = 12
  ref = C_element
FEATURE [App::DocumentObjectGroupPython] H_element097  label="H_element : 22"  # scripted group (container) (typed FeaturePython)
  n = 22
  ref = H_element
FEATURE [App::DocumentObjectGroupPython] O_element092  label="O_element : 11"  # scripted group (container) (typed FeaturePython)
  n = 11
  ref = O_element
FEATURE [App::DocumentObjectGroupPython] G4_SUCROSE  # scripted group (container) (typed FeaturePython)
  Dunit = g/cm3
  Dvalue = 1.5805
  Group = -> [C_element106,H_element097,O_element092]
  conduct = 2
  density = 1
  expand = 3
  formula = G4_SUCROSE
  name = G4_SUCROSE
  specific = 4
FEATURE [App::DocumentObjectGroupPython] C_element107  label="C_element : 18"  # scripted group (container) (typed FeaturePython)
  n = 18
  ref = C_element
FEATURE [App::DocumentObjectGroupPython] H_element098  label="H_element : 054"  # scripted group (container) (typed FeaturePython)
  n = 14
  ref = H_element
FEATURE [App::DocumentObjectGroupPython] G4_TERPHENYL  # scripted group (container) (typed FeaturePython)
  Dunit = g/cm3
  Dvalue = 1.24
  Group = -> [C_element107,H_element098]
  conduct = 2
  density = 1
  expand = 3
  formula = G4_TERPHENYL
  name = G4_TERPHENYL
  specific = 4
FEATURE [App::DocumentObjectGroupPython] H_element099  label="H_element : 0.146"  # scripted group (container) (typed FeaturePython)
  n = 0.106
FEATURE [App::DocumentObjectGroupPython] C_element108  label="C_element : 0.883"  # scripted group (container) (typed FeaturePython)
  n = 0.099
FEATURE [App::DocumentObjectGroupPython] N_element041  label="N_element : 0.020"  # scripted group (container) (typed FeaturePython)
  n = 0.02
FEATURE [App::DocumentObjectGroupPython] O_element093  label="O_element : 0.766"  # scripted group (container) (typed FeaturePython)
  n = 0.766
FEATURE [App::DocumentObjectGroupPython] Na_element018  label="Na_element : 0.101"  # scripted group (container) (typed FeaturePython)
  n = 0.002
FEATURE [App::DocumentObjectGroupPython] P_element010  label="P_element : 0.108"  # scripted group (container) (typed FeaturePython)
  n = 0.001
FEATURE [App::DocumentObjectGroupPython] S_element021  label="S_element : 0.022"  # scripted group (container) (typed FeaturePython)
  n = 0.002
FEATURE [App::DocumentObjectGroupPython] Cl_element024  label="Cl_element : 0.002"  # scripted group (container) (typed FeaturePython)
  n = 0.002
FEATURE [App::DocumentObjectGroupPython] K_element011  label="K_element : 0.017"  # scripted group (container) (typed FeaturePython)
  n = 0.002
FEATURE [App::DocumentObjectGroupPython] G4_TESTIS_ICRP  # scripted group (container) (typed FeaturePython)
  Dunit = g/cm3
  Dvalue = 1.04
  Group = -> [H_element099,C_element108,N_element041,O_element093,Na_element018,P_element010,S_element021,Cl_element024,K_element011]
  conduct = 2
  density = 1
  expand = 3
  formula = G4_TESTIS_ICRP
  name = G4_TESTIS_ICRP
  specific = 4
FEATURE [App::DocumentObjectGroupPython] C_element109  label="C_element : 060"  # scripted group (container) (typed FeaturePython)
  n = 2
  ref = C_element
FEATURE [App::DocumentObjectGroupPython] Cl_element025  label="Cl_element : 012"  # scripted group (container) (typed FeaturePython)
  n = 4
  ref = Cl_element
FEATURE [App::DocumentObjectGroupPython] G4_TETRACHLOROETHYLENE  # scripted group (container) (typed FeaturePython)
  Dunit = g/cm3
  Dvalue = 1.625
  Group = -> [C_element109,Cl_element025]
  conduct = 2
  density = 1
  expand = 3
  formula = G4_TETRACHLOROETHYLENE
  name = G4_TETRACHLOROETHYLENE
  specific = 4
FEATURE [App::DocumentObjectGroupPython] Tl_element001  label="Tl_element : 1"  # scripted group (container) (typed FeaturePython)
  n = 1
  ref = Tl_element
FEATURE [App::DocumentObjectGroupPython] Cl_element026  label="Cl_element : 013"  # scripted group (container) (typed FeaturePython)
  n = 1
  ref = Cl_element
FEATURE [App::DocumentObjectGroupPython] G4_THALLIUM_CHLORIDE  # scripted group (container) (typed FeaturePython)
  Dunit = g/cm3
  Dvalue = 7.004
  Group = -> [Tl_element001,Cl_element026]
  conduct = 2
  density = 1
  expand = 3
  formula = G4_THALLIUM_CHLORIDE
  name = G4_THALLIUM_CHLORIDE
  specific = 4
FEATURE [App::DocumentObjectGroupPython] H_element100  label="H_element : 0.147"  # scripted group (container) (typed FeaturePython)
  n = 0.105
FEATURE [App::DocumentObjectGroupPython] C_element110  label="C_element : 0.256"  # scripted group (container) (typed FeaturePython)
  n = 0.256
FEATURE [App::DocumentObjectGroupPython] N_element042  label="N_element : 0.760"  # scripted group (container) (typed FeaturePython)
  n = 0.027
FEATURE [App::DocumentObjectGroupPython] O_element094  label="O_element : 0.602"  # scripted group (container) (typed FeaturePython)
  n = 0.602
FEATURE [App::DocumentObjectGroupPython] Na_element019  label="Na_element : 0.102"  # scripted group (container) (typed FeaturePython)
  n = 0.001
FEATURE [App::DocumentObjectGroupPython] P_element011  label="P_element : 0.109"  # scripted group (container) (typed FeaturePython)
  n = 0.002
FEATURE [App::DocumentObjectGroupPython] S_element022  label="S_element : 0.023"  # scripted group (container) (typed FeaturePython)
  n = 0.003
FEATURE [App::DocumentObjectGroupPython] Cl_element027  label="Cl_element : 0.591"  # scripted group (container) (typed FeaturePython)
  n = 0.002
FEATURE [App::DocumentObjectGroupPython] K_element012  label="K_element : 0.018"  # scripted group (container) (typed FeaturePython)
  n = 0.002
FEATURE [App::DocumentObjectGroupPython] G4_TISSUE_SOFT_ICRP  # scripted group (container) (typed FeaturePython)
  Dunit = g/cm3
  Dvalue = 1.03
  Group = -> [H_element100,C_element110,N_element042,O_element094,Na_element019,P_element011,S_element022,Cl_element027,K_element012]
  conduct = 2
  density = 1
  expand = 3
  formula = G4_TISSUE_SOFT_ICRP
  name = G4_TISSUE_SOFT_ICRP
  specific = 4
FEATURE [App::DocumentObjectGroupPython] H_element101  label="H_element : 0.148"  # scripted group (container) (typed FeaturePython)
  n = 0.101
FEATURE [App::DocumentObjectGroupPython] C_element111  label="C_element : 0.111"  # scripted group (container) (typed FeaturePython)
  n = 0.111
FEATURE [App::DocumentObjectGroupPython] N_element043  label="N_element : 0.026"  # scripted group (container) (typed FeaturePython)
  n = 0.026
FEATURE [App::DocumentObjectGroupPython] O_element095  label="O_element : 0.762"  # scripted group (container) (typed FeaturePython)
  n = 0.762
FEATURE [App::DocumentObjectGroupPython] G4_TISSUE_SOFT_ICRU_4  label="G4_TISSUE_SOFT_ICRU-4"  # scripted group (container) (typed FeaturePython)
  Dunit = g/cm3
  Dvalue = 1
  Group = -> [H_element101,C_element111,N_element043,O_element095]
  conduct = 2
  density = 1
  expand = 3
  formula = G4_TISSUE_SOFT_ICRU-4
  name = G4_TISSUE_SOFT_ICRU-4
  specific = 4
FEATURE [App::DocumentObjectGroupPython] H_element102  label="H_element : 0.149"  # scripted group (container) (typed FeaturePython)
  n = 0.101869
FEATURE [App::DocumentObjectGroupPython] C_element112  label="C_element : 0.456"  # scripted group (container) (typed FeaturePython)
  n = 0.456179
FEATURE [App::DocumentObjectGroupPython] N_element044  label="N_element : 0.761"  # scripted group (container) (typed FeaturePython)
  n = 0.035172
FEATURE [App::DocumentObjectGroupPython] O_element096  label="O_element : 0.407"  # scripted group (container) (typed FeaturePython)
  n = 0.40678
FEATURE [App::DocumentObjectGroupPython] G4_TISSUE_METHANE  label="G4_TISSUE-METHANE"  # scripted group (container) (typed FeaturePython)
  Dunit = g/cm3
  Dvalue = 0.00106409
  Group = -> [H_element102,C_element112,N_element044,O_element096]
  conduct = 2
  density = 1
  expand = 3
  formula = G4_TISSUE-METHANE
  name = G4_TISSUE-METHANE
  specific = 4
FEATURE [App::DocumentObjectGroupPython] H_element103  label="H_element : 0.103"  # scripted group (container) (typed FeaturePython)
  n = 0.102672
FEATURE [App::DocumentObjectGroupPython] C_element113  label="C_element : 0.569"  # scripted group (container) (typed FeaturePython)
  n = 0.56894
FEATURE [App::DocumentObjectGroupPython] N_element045  label="N_element : 0.762"  # scripted group (container) (typed FeaturePython)
  n = 0.035022
FEATURE [App::DocumentObjectGroupPython] O_element097  label="O_element : 0.293"  # scripted group (container) (typed FeaturePython)
  n = 0.293366
FEATURE [App::DocumentObjectGroupPython] G4_TISSUE_PROPANE  label="G4_TISSUE-PROPANE"  # scripted group (container) (typed FeaturePython)
  Dunit = g/cm3
  Dvalue = 0.00182628
  Group = -> [H_element103,C_element113,N_element045,O_element097]
  conduct = 2
  density = 1
  expand = 3
  formula = G4_TISSUE-PROPANE
  name = G4_TISSUE-PROPANE
  specific = 4
FEATURE [App::DocumentObjectGroupPython] Ti_element003  label="Ti_element : 1"  # scripted group (container) (typed FeaturePython)
  n = 1
  ref = Ti_element
FEATURE [App::DocumentObjectGroupPython] O_element098  label="O_element : 052"  # scripted group (container) (typed FeaturePython)
  n = 2
  ref = O_element
FEATURE [App::DocumentObjectGroupPython] G4_TITANIUM_DIOXIDE  # scripted group (container) (typed FeaturePython)
  Dunit = g/cm3
  Dvalue = 4.26
  Group = -> [Ti_element003,O_element098]
  conduct = 2
  density = 1
  expand = 3
  formula = G4_TITANIUM_DIOXIDE
  name = G4_TITANIUM_DIOXIDE
  specific = 4
FEATURE [App::DocumentObjectGroupPython] C_element114  label="C_element : 061"  # scripted group (container) (typed FeaturePython)
  n = 7
  ref = C_element
FEATURE [App::DocumentObjectGroupPython] H_element104  label="H_element : 055"  # scripted group (container) (typed FeaturePython)
  n = 8
  ref = H_element
FEATURE [App::DocumentObjectGroupPython] G4_TOLUENE  # scripted group (container) (typed FeaturePython)
  Dunit = g/cm3
  Dvalue = 0.8669
  Group = -> [C_element114,H_element104]
  conduct = 2
  density = 1
  expand = 3
  formula = G4_TOLUENE
  name = G4_TOLUENE
  specific = 4
FEATURE [App::DocumentObjectGroupPython] C_element115  label="C_element : 062"  # scripted group (container) (typed FeaturePython)
  n = 2
  ref = C_element
FEATURE [App::DocumentObjectGroupPython] H_element105  label="H_element : 056"  # scripted group (container) (typed FeaturePython)
  n = 1
  ref = H_element
FEATURE [App::DocumentObjectGroupPython] Cl_element028  label="Cl_element : 014"  # scripted group (container) (typed FeaturePython)
  n = 3
  ref = Cl_element
FEATURE [App::DocumentObjectGroupPython] G4_TRICHLOROETHYLENE  # scripted group (container) (typed FeaturePython)
  Dunit = g/cm3
  Dvalue = 1.46
  Group = -> [C_element115,H_element105,Cl_element028]
  conduct = 2
  density = 1
  expand = 3
  formula = G4_TRICHLOROETHYLENE
  name = G4_TRICHLOROETHYLENE
  specific = 4
FEATURE [App::DocumentObjectGroupPython] C_element116  label="C_element : 063"  # scripted group (container) (typed FeaturePython)
  n = 6
  ref = C_element
FEATURE [App::DocumentObjectGroupPython] H_element106  label="H_element : 15"  # scripted group (container) (typed FeaturePython)
  n = 15
  ref = H_element
FEATURE [App::DocumentObjectGroupPython] O_element099  label="O_element : 053"  # scripted group (container) (typed FeaturePython)
  n = 4
  ref = O_element
FEATURE [App::DocumentObjectGroupPython] P_element012  label="P_element : 1"  # scripted group (container) (typed FeaturePython)
  n = 1
  ref = P_element
FEATURE [App::DocumentObjectGroupPython] G4_TRIETHYL_PHOSPHATE  # scripted group (container) (typed FeaturePython)
  Dunit = g/cm3
  Dvalue = 1.07
  Group = -> [C_element116,H_element106,O_element099,P_element012]
  conduct = 2
  density = 1
  expand = 3
  formula = G4_TRIETHYL_PHOSPHATE
  name = G4_TRIETHYL_PHOSPHATE
  specific = 4
FEATURE [App::DocumentObjectGroupPython] W_element003  label="W_element : 003"  # scripted group (container) (typed FeaturePython)
  n = 1
  ref = W_element
FEATURE [App::DocumentObjectGroupPython] F_element017  label="F_element : 6"  # scripted group (container) (typed FeaturePython)
  n = 6
  ref = F_element
FEATURE [App::DocumentObjectGroupPython] G4_TUNGSTEN_HEXAFLUORIDE  # scripted group (container) (typed FeaturePython)
  Dunit = g/cm3
  Dvalue = 2.4
  Group = -> [W_element003,F_element017]
  conduct = 2
  density = 1
  expand = 3
  formula = G4_TUNGSTEN_HEXAFLUORIDE
  name = G4_TUNGSTEN_HEXAFLUORIDE
  specific = 4
FEATURE [App::DocumentObjectGroupPython] U_element001  label="U_element : 1"  # scripted group (container) (typed FeaturePython)
  n = 1
  ref = U_element
FEATURE [App::DocumentObjectGroupPython] C_element117  label="C_element : 064"  # scripted group (container) (typed FeaturePython)
  n = 2
  ref = C_element
FEATURE [App::DocumentObjectGroupPython] G4_URANIUM_DICARBIDE  # scripted group (container) (typed FeaturePython)
  Dunit = g/cm3
  Dvalue = 11.28
  Group = -> [U_element001,C_element117]
  conduct = 2
  density = 1
  expand = 3
  formula = G4_URANIUM_DICARBIDE
  name = G4_URANIUM_DICARBIDE
  specific = 4
FEATURE [App::DocumentObjectGroupPython] U_element002  label="U_element : 002"  # scripted group (container) (typed FeaturePython)
  n = 1
  ref = U_element
FEATURE [App::DocumentObjectGroupPython] C_element118  label="C_element : 065"  # scripted group (container) (typed FeaturePython)
  n = 1
  ref = C_element
FEATURE [App::DocumentObjectGroupPython] G4_URANIUM_MONOCARBIDE  # scripted group (container) (typed FeaturePython)
  Dunit = g/cm3
  Dvalue = 13.63
  Group = -> [U_element002,C_element118]
  conduct = 2
  density = 1
  expand = 3
  formula = G4_URANIUM_MONOCARBIDE
  name = G4_URANIUM_MONOCARBIDE
  specific = 4
FEATURE [App::DocumentObjectGroupPython] U_element003  label="U_element : 003"  # scripted group (container) (typed FeaturePython)
  n = 1
  ref = U_element
FEATURE [App::DocumentObjectGroupPython] O_element100  label="O_element : 054"  # scripted group (container) (typed FeaturePython)
  n = 2
  ref = O_element
FEATURE [App::DocumentObjectGroupPython] G4_URANIUM_OXIDE  # scripted group (container) (typed FeaturePython)
  Dunit = g/cm3
  Dvalue = 10.96
  Group = -> [U_element003,O_element100]
  conduct = 2
  density = 1
  expand = 3
  formula = G4_URANIUM_OXIDE
  name = G4_URANIUM_OXIDE
  specific = 4
FEATURE [App::DocumentObjectGroupPython] C_element119  label="C_element : 066"  # scripted group (container) (typed FeaturePython)
  n = 1
  ref = C_element
FEATURE [App::DocumentObjectGroupPython] H_element107  label="H_element : 057"  # scripted group (container) (typed FeaturePython)
  n = 4
  ref = H_element
FEATURE [App::DocumentObjectGroupPython] N_element046  label="N_element : 019"  # scripted group (container) (typed FeaturePython)
  n = 2
  ref = N_element
FEATURE [App::DocumentObjectGroupPython] O_element101  label="O_element : 055"  # scripted group (container) (typed FeaturePython)
  n = 1
  ref = O_element
FEATURE [App::DocumentObjectGroupPython] G4_UREA  # scripted group (container) (typed FeaturePython)
  Dunit = g/cm3
  Dvalue = 1.323
  Group = -> [C_element119,H_element107,N_element046,O_element101]
  conduct = 2
  density = 1
  expand = 3
  formula = G4_UREA
  name = G4_UREA
  specific = 4
FEATURE [App::DocumentObjectGroupPython] C_element120  label="C_element : 067"  # scripted group (container) (typed FeaturePython)
  n = 5
  ref = C_element
FEATURE [App::DocumentObjectGroupPython] H_element108  label="H_element : 058"  # scripted group (container) (typed FeaturePython)
  n = 11
  ref = H_element
FEATURE [App::DocumentObjectGroupPython] N_element047  label="N_element : 020"  # scripted group (container) (typed FeaturePython)
  n = 1
  ref = N_element
FEATURE [App::DocumentObjectGroupPython] O_element102  label="O_element : 056"  # scripted group (container) (typed FeaturePython)
  n = 2
  ref = O_element
FEATURE [App::DocumentObjectGroupPython] G4_VALINE  # scripted group (container) (typed FeaturePython)
  Dunit = g/cm3
  Dvalue = 1.23
  Group = -> [C_element120,H_element108,N_element047,O_element102]
  conduct = 2
  density = 1
  expand = 3
  formula = G4_VALINE
  name = G4_VALINE
  specific = 4
FEATURE [App::DocumentObjectGroupPython] H_element109  label="H_element : 0.009"  # scripted group (container) (typed FeaturePython)
  n = 0.009417
FEATURE [App::DocumentObjectGroupPython] C_element121  label="C_element : 0.281"  # scripted group (container) (typed FeaturePython)
  n = 0.280555
FEATURE [App::DocumentObjectGroupPython] F_element018  label="F_element : 0.710"  # scripted group (container) (typed FeaturePython)
  n = 0.710028
FEATURE [App::DocumentObjectGroupPython] G4_VITON  # scripted group (container) (typed FeaturePython)
  Dunit = g/cm3
  Dvalue = 1.8
  Group = -> [H_element109,C_element121,F_element018]
  conduct = 2
  density = 1
  expand = 3
  formula = G4_VITON
  name = G4_VITON
  specific = 4
FEATURE [App::DocumentObjectGroupPython] H_element110  label="H_element : 059"  # scripted group (container) (typed FeaturePython)
  n = 2
  ref = H_element
FEATURE [App::DocumentObjectGroupPython] O_element103  label="O_element : 057"  # scripted group (container) (typed FeaturePython)
  n = 1
  ref = O_element
FEATURE [App::DocumentObjectGroupPython] G4_WATER  # scripted group (container) (typed FeaturePython)
  Dunit = g/cm3
  Dvalue = 1
  Group = -> [H_element110,O_element103]
  conduct = 2
  density = 1
  expand = 3
  formula = G4_WATER
  name = G4_WATER
  specific = 4
FEATURE [App::DocumentObjectGroupPython] H_element111  label="H_element : 060"  # scripted group (container) (typed FeaturePython)
  n = 2
  ref = H_element
FEATURE [App::DocumentObjectGroupPython] O_element104  label="O_element : 058"  # scripted group (container) (typed FeaturePython)
  n = 1
  ref = O_element
FEATURE [App::DocumentObjectGroupPython] G4_WATER_VAPOR  # scripted group (container) (typed FeaturePython)
  Dunit = g/cm3
  Dvalue = 0.000756182
  Group = -> [H_element111,O_element104]
  conduct = 2
  density = 1
  expand = 3
  formula = G4_WATER_VAPOR
  name = G4_WATER_VAPOR
  specific = 4
FEATURE [App::DocumentObjectGroupPython] C_element122  label="C_element : 068"  # scripted group (container) (typed FeaturePython)
  n = 8
  ref = C_element
FEATURE [App::DocumentObjectGroupPython] H_element112  label="H_element : 061"  # scripted group (container) (typed FeaturePython)
  n = 10
  ref = H_element
FEATURE [App::DocumentObjectGroupPython] G4_XYLENE  # scripted group (container) (typed FeaturePython)
  Dunit = g/cm3
  Dvalue = 0.87
  Group = -> [C_element122,H_element112]
  conduct = 2
  density = 1
  expand = 3
  formula = G4_XYLENE
  name = G4_XYLENE
  specific = 4
FEATURE [App::DocumentObjectGroupPython] C_element123  label="C_element : 069"  # scripted group (container) (typed FeaturePython)
  n = 1
  ref = C_element
FEATURE [App::DocumentObjectGroupPython] G4_GRAPHITE  # scripted group (container) (typed FeaturePython)
  Dunit = g/cm3
  Dvalue = 2.21
  Group = -> [C_element123]
  conduct = 2
  density = 1
  expand = 3
  formula = G4_GRAPHITE
  name = G4_GRAPHITE
  specific = 4
FEATURE [App::DocumentObjectGroupPython] NIST  # scripted group (container) (typed FeaturePython)
  Group = -> [G4_A_150_TISSUE,G4_ACETONE,G4_ACETYLENE,G4_ADENINE,G4_ADIPOSE_TISSUE_ICRP,G4_AIR,G4_ALANINE,G4_ALUMINUM_OXIDE,G4_AMBER,G4_AMMONIA,G4_ANILINE,G4_ANTHRACENE,G4_B_100_BONE,G4_BAKELITE,G4_BARIUM_FLUORIDE,G4_BARIUM_SULFATE,G4_BENZENE,G4_BERYLLIUM_OXIDE,G4_BGO,G4_BLOOD_ICRP,G4_BONE_COMPACT_ICRU,G4_BONE_CORTICAL_ICRP,G4_BORON_CARBIDE,G4_BORON_OXIDE,G4_BRAIN_ICRP,G4_BUTANE,G4_N_BUTYL_ALCOHOL,G4_C_552,+152 more]
FEATURE [App::DocumentObjectGroupPython] H_element113  label="H_element : 062"  # scripted group (container) (typed FeaturePython)
  n = 1
  ref = H_element
FEATURE [App::DocumentObjectGroupPython] G4_H  # scripted group (container) (typed FeaturePython)
  Dunit = g/cm3
  Dvalue = 8.3748e-05
  Group = -> [H_element113]
  conduct = 2
  density = 1
  expand = 3
  formula = H
  name = G4_H
  specific = 4
FEATURE [App::DocumentObjectGroupPython] He_element001  label="He_element : 1"  # scripted group (container) (typed FeaturePython)
  n = 1
  ref = He_element
FEATURE [App::DocumentObjectGroupPython] G4_He  # scripted group (container) (typed FeaturePython)
  Dunit = g/cm3
  Dvalue = 0.000166322
  Group = -> [He_element001]
  conduct = 2
  density = 1
  expand = 3
  formula = He
  name = G4_He
  specific = 4
FEATURE [App::DocumentObjectGroupPython] Li_element008  label="Li_element : 008"  # scripted group (container) (typed FeaturePython)
  n = 1
  ref = Li_element
FEATURE [App::DocumentObjectGroupPython] G4_Li  # scripted group (container) (typed FeaturePython)
  Dunit = g/cm3
  Dvalue = 0.534
  Group = -> [Li_element008]
  conduct = 2
  density = 1
  expand = 3
  formula = Li
  name = G4_Li
  specific = 4
FEATURE [App::DocumentObjectGroupPython] Be_element002  label="Be_element : 002"  # scripted group (container) (typed FeaturePython)
  n = 1
  ref = Be_element
FEATURE [App::DocumentObjectGroupPython] G4_Be  # scripted group (container) (typed FeaturePython)
  Dunit = g/cm3
  Dvalue = 1.848
  Group = -> [Be_element002]
  conduct = 2
  density = 1
  expand = 3
  formula = Be
  name = G4_Be
  specific = 4
FEATURE [App::DocumentObjectGroupPython] B_element007  label="B_element : 007"  # scripted group (container) (typed FeaturePython)
  n = 1
  ref = B_element
FEATURE [App::DocumentObjectGroupPython] G4_B  # scripted group (container) (typed FeaturePython)
  Dunit = g/cm3
  Dvalue = 2.37
  Group = -> [B_element007]
  conduct = 2
  density = 1
  expand = 3
  formula = B
  name = G4_B
  specific = 4
FEATURE [App::DocumentObjectGroupPython] C_element124  label="C_element : 070"  # scripted group (container) (typed FeaturePython)
  n = 1
  ref = C_element
FEATURE [App::DocumentObjectGroupPython] G4_C  # scripted group (container) (typed FeaturePython)
  Dunit = g/cm3
  Dvalue = 2
  Group = -> [C_element124]
  conduct = 2
  density = 1
  expand = 3
  formula = C
  name = G4_C
  specific = 4
FEATURE [App::DocumentObjectGroupPython] N_element048  label="N_element : 021"  # scripted group (container) (typed FeaturePython)
  n = 1
  ref = N_element
FEATURE [App::DocumentObjectGroupPython] G4_N  # scripted group (container) (typed FeaturePython)
  Dunit = g/cm3
  Dvalue = 0.0011652
  Group = -> [N_element048]
  conduct = 2
  density = 1
  expand = 3
  formula = N
  name = G4_N
  specific = 4
FEATURE [App::DocumentObjectGroupPython] O_element105  label="O_element : 059"  # scripted group (container) (typed FeaturePython)
  n = 1
  ref = O_element
FEATURE [App::DocumentObjectGroupPython] G4_O  # scripted group (container) (typed FeaturePython)
  Dunit = g/cm3
  Dvalue = 0.00133151
  Group = -> [O_element105]
  conduct = 2
  density = 1
  expand = 3
  formula = O
  name = G4_O
  specific = 4
FEATURE [App::DocumentObjectGroupPython] F_element019  label="F_element : 008"  # scripted group (container) (typed FeaturePython)
  n = 1
  ref = F_element
FEATURE [App::DocumentObjectGroupPython] G4_F  # scripted group (container) (typed FeaturePython)
  Dunit = g/cm3
  Dvalue = 0.00158029
  Group = -> [F_element019]
  conduct = 2
  density = 1
  expand = 3
  formula = F
  name = G4_F
  specific = 4
FEATURE [App::DocumentObjectGroupPython] Ne_element001  label="Ne_element : 1"  # scripted group (container) (typed FeaturePython)
  n = 1
  ref = Ne_element
FEATURE [App::DocumentObjectGroupPython] G4_Ne  # scripted group (container) (typed FeaturePython)
  Dunit = g/cm3
  Dvalue = 0.000838505
  Group = -> [Ne_element001]
  conduct = 2
  density = 1
  expand = 3
  formula = Ne
  name = G4_Ne
  specific = 4
FEATURE [App::DocumentObjectGroupPython] Na_element020  label="Na_element : 005"  # scripted group (container) (typed FeaturePython)
  n = 1
  ref = Na_element
FEATURE [App::DocumentObjectGroupPython] G4_Na  # scripted group (container) (typed FeaturePython)
  Dunit = g/cm3
  Dvalue = 0.971
  Group = -> [Na_element020]
  conduct = 2
  density = 1
  expand = 3
  formula = Na
  name = G4_Na
  specific = 4
FEATURE [App::DocumentObjectGroupPython] Mg_element011  label="Mg_element : 005"  # scripted group (container) (typed FeaturePython)
  n = 1
  ref = Mg_element
FEATURE [App::DocumentObjectGroupPython] G4_Mg  # scripted group (container) (typed FeaturePython)
  Dunit = g/cm3
  Dvalue = 1.74
  Group = -> [Mg_element011]
  conduct = 2
  density = 1
  expand = 3
  formula = Mg
  name = G4_Mg
  specific = 4
FEATURE [App::DocumentObjectGroupPython] Al_element004  label="Al_element : 1"  # scripted group (container) (typed FeaturePython)
  n = 1
  ref = Al_element
FEATURE [App::DocumentObjectGroupPython] G4_Al  # scripted group (container) (typed FeaturePython)
  Dunit = g/cm3
  Dvalue = 2.699
  Group = -> [Al_element004]
  conduct = 2
  density = 1
  expand = 3
  formula = Al
  name = G4_Al
  specific = 4
FEATURE [App::DocumentObjectGroupPython] Si_element007  label="Si_element : 002"  # scripted group (container) (typed FeaturePython)
  n = 1
  ref = Si_element
FEATURE [App::DocumentObjectGroupPython] G4_Si  # scripted group (container) (typed FeaturePython)
  Dunit = g/cm3
  Dvalue = 2.33
  Group = -> [Si_element007]
  conduct = 2
  density = 1
  expand = 3
  formula = Si
  name = G4_Si
  specific = 4
FEATURE [App::DocumentObjectGroupPython] P_element013  label="P_element : 002"  # scripted group (container) (typed FeaturePython)
  n = 1
  ref = P_element
FEATURE [App::DocumentObjectGroupPython] G4_P  # scripted group (container) (typed FeaturePython)
  Dunit = g/cm3
  Dvalue = 2.2
  Group = -> [P_element013]
  conduct = 2
  density = 1
  expand = 3
  formula = P
  name = G4_P
  specific = 4
FEATURE [App::DocumentObjectGroupPython] S_element023  label="S_element : 007"  # scripted group (container) (typed FeaturePython)
  n = 1
  ref = S_element
FEATURE [App::DocumentObjectGroupPython] G4_S  # scripted group (container) (typed FeaturePython)
  Dunit = g/cm3
  Dvalue = 2
  Group = -> [S_element023]
  conduct = 2
  density = 1
  expand = 3
  formula = S
  name = G4_S
  specific = 4
FEATURE [App::DocumentObjectGroupPython] Cl_element029  label="Cl_element : 015"  # scripted group (container) (typed FeaturePython)
  n = 1
  ref = Cl_element
FEATURE [App::DocumentObjectGroupPython] G4_Cl  # scripted group (container) (typed FeaturePython)
  Dunit = g/cm3
  Dvalue = 0.00299473
  Group = -> [Cl_element029]
  conduct = 2
  density = 1
  expand = 3
  formula = Cl
  name = G4_Cl
  specific = 4
FEATURE [App::DocumentObjectGroupPython] Ar_element002  label="Ar_element : 1"  # scripted group (container) (typed FeaturePython)
  n = 1
  ref = Ar_element
FEATURE [App::DocumentObjectGroupPython] G4_Ar  # scripted group (container) (typed FeaturePython)
  Dunit = g/cm3
  Dvalue = 0.00166201
  Group = -> [Ar_element002]
  conduct = 2
  density = 1
  expand = 3
  formula = Ar
  name = G4_Ar
  specific = 4
FEATURE [App::DocumentObjectGroupPython] K_element013  label="K_element : 003"  # scripted group (container) (typed FeaturePython)
  n = 1
  ref = K_element
FEATURE [App::DocumentObjectGroupPython] G4_K  # scripted group (container) (typed FeaturePython)
  Dunit = g/cm3
  Dvalue = 0.862
  Group = -> [K_element013]
  conduct = 2
  density = 1
  expand = 3
  formula = K
  name = G4_K
  specific = 4
FEATURE [App::DocumentObjectGroupPython] Ca_element014  label="Ca_element : 007"  # scripted group (container) (typed FeaturePython)
  n = 1
  ref = Ca_element
FEATURE [App::DocumentObjectGroupPython] G4_Ca  # scripted group (container) (typed FeaturePython)
  Dunit = g/cm3
  Dvalue = 1.55
  Group = -> [Ca_element014]
  conduct = 2
  density = 1
  expand = 3
  formula = Ca
  name = G4_Ca
  specific = 4
FEATURE [App::DocumentObjectGroupPython] Sc_element001  label="Sc_element : 1"  # scripted group (container) (typed FeaturePython)
  n = 1
  ref = Sc_element
FEATURE [App::DocumentObjectGroupPython] G4_Sc  # scripted group (container) (typed FeaturePython)
  Dunit = g/cm3
  Dvalue = 2.989
  Group = -> [Sc_element001]
  conduct = 2
  density = 1
  expand = 3
  formula = Sc
  name = G4_Sc
  specific = 4
FEATURE [App::DocumentObjectGroupPython] Ti_element004  label="Ti_element : 002"  # scripted group (container) (typed FeaturePython)
  n = 1
  ref = Ti_element
FEATURE [App::DocumentObjectGroupPython] G4_Ti  # scripted group (container) (typed FeaturePython)
  Dunit = g/cm3
  Dvalue = 4.54
  Group = -> [Ti_element004]
  conduct = 2
  density = 1
  expand = 3
  formula = Ti
  name = G4_Ti
  specific = 4
FEATURE [App::DocumentObjectGroupPython] V_element001  label="V_element : 1"  # scripted group (container) (typed FeaturePython)
  n = 1
  ref = V_element
FEATURE [App::DocumentObjectGroupPython] G4_V  # scripted group (container) (typed FeaturePython)
  Dunit = g/cm3
  Dvalue = 6.11
  Group = -> [V_element001]
  conduct = 2
  density = 1
  expand = 3
  formula = V
  name = G4_V
  specific = 4
FEATURE [App::DocumentObjectGroupPython] Cr_element001  label="Cr_element : 1"  # scripted group (container) (typed FeaturePython)
  n = 1
  ref = Cr_element
FEATURE [App::DocumentObjectGroupPython] G4_Cr  # scripted group (container) (typed FeaturePython)
  Dunit = g/cm3
  Dvalue = 7.18
  Group = -> [Cr_element001]
  conduct = 2
  density = 1
  expand = 3
  formula = Cr
  name = G4_Cr
  specific = 4
FEATURE [App::DocumentObjectGroupPython] Mn_element001  label="Mn_element : 1"  # scripted group (container) (typed FeaturePython)
  n = 1
  ref = Mn_element
FEATURE [App::DocumentObjectGroupPython] G4_Mn  # scripted group (container) (typed FeaturePython)
  Dunit = g/cm3
  Dvalue = 7.44
  Group = -> [Mn_element001]
  conduct = 2
  density = 1
  expand = 3
  formula = Mn
  name = G4_Mn
  specific = 4
FEATURE [App::DocumentObjectGroupPython] Fe_element007  label="Fe_element : 004"  # scripted group (container) (typed FeaturePython)
  n = 1
  ref = Fe_element
FEATURE [App::DocumentObjectGroupPython] G4_Fe  # scripted group (container) (typed FeaturePython)
  Dunit = g/cm3
  Dvalue = 7.874
  Group = -> [Fe_element007]
  conduct = 2
  density = 1
  expand = 3
  formula = Fe
  name = G4_Fe
  specific = 4
FEATURE [App::DocumentObjectGroupPython] Co_element001  label="Co_element : 1"  # scripted group (container) (typed FeaturePython)
  n = 1
  ref = Co_element
FEATURE [App::DocumentObjectGroupPython] G4_Co  # scripted group (container) (typed FeaturePython)
  Dunit = g/cm3
  Dvalue = 8.9
  Group = -> [Co_element001]
  conduct = 2
  density = 1
  expand = 3
  formula = Co
  name = G4_Co
  specific = 4
FEATURE [App::DocumentObjectGroupPython] Ni_element001  label="Ni_element : 1"  # scripted group (container) (typed FeaturePython)
  n = 1
  ref = Ni_element
FEATURE [App::DocumentObjectGroupPython] G4_Ni  # scripted group (container) (typed FeaturePython)
  Dunit = g/cm3
  Dvalue = 8.902
  Group = -> [Ni_element001]
  conduct = 2
  density = 1
  expand = 3
  formula = Ni
  name = G4_Ni
  specific = 4
FEATURE [App::DocumentObjectGroupPython] Cu_element001  label="Cu_element : 1"  # scripted group (container) (typed FeaturePython)
  n = 1
  ref = Cu_element
FEATURE [App::DocumentObjectGroupPython] G4_Cu  # scripted group (container) (typed FeaturePython)
  Dunit = g/cm3
  Dvalue = 8.96
  Group = -> [Cu_element001]
  conduct = 2
  density = 1
  expand = 3
  formula = Cu
  name = G4_Cu
  specific = 4
FEATURE [App::DocumentObjectGroupPython] Zn_element001  label="Zn_element : 1"  # scripted group (container) (typed FeaturePython)
  n = 1
  ref = Zn_element
FEATURE [App::DocumentObjectGroupPython] G4_Zn  # scripted group (container) (typed FeaturePython)
  Dunit = g/cm3
  Dvalue = 7.133
  Group = -> [Zn_element001]
  conduct = 2
  density = 1
  expand = 3
  formula = Zn
  name = G4_Zn
  specific = 4
FEATURE [App::DocumentObjectGroupPython] Ga_element002  label="Ga_element : 002"  # scripted group (container) (typed FeaturePython)
  n = 1
  ref = Ga_element
FEATURE [App::DocumentObjectGroupPython] G4_Ga  # scripted group (container) (typed FeaturePython)
  Dunit = g/cm3
  Dvalue = 5.904
  Group = -> [Ga_element002]
  conduct = 2
  density = 1
  expand = 3
  formula = Ga
  name = G4_Ga
  specific = 4
FEATURE [App::DocumentObjectGroupPython] Ge_element002  label="Ge_element : 1"  # scripted group (container) (typed FeaturePython)
  n = 1
  ref = Ge_element
FEATURE [App::DocumentObjectGroupPython] G4_Ge  # scripted group (container) (typed FeaturePython)
  Dunit = g/cm3
  Dvalue = 5.323
  Group = -> [Ge_element002]
  conduct = 2
  density = 1
  expand = 3
  formula = Ge
  name = G4_Ge
  specific = 4
FEATURE [App::DocumentObjectGroupPython] As_element003  label="As_element : 002"  # scripted group (container) (typed FeaturePython)
  n = 1
  ref = As_element
FEATURE [App::DocumentObjectGroupPython] G4_As  # scripted group (container) (typed FeaturePython)
  Dunit = g/cm3
  Dvalue = 5.73
  Group = -> [As_element003]
  conduct = 2
  density = 1
  expand = 3
  formula = As
  name = G4_As
  specific = 4
FEATURE [App::DocumentObjectGroupPython] Se_element001  label="Se_element : 1"  # scripted group (container) (typed FeaturePython)
  n = 1
  ref = Se_element
FEATURE [App::DocumentObjectGroupPython] G4_Se  # scripted group (container) (typed FeaturePython)
  Dunit = g/cm3
  Dvalue = 4.5
  Group = -> [Se_element001]
  conduct = 2
  density = 1
  expand = 3
  formula = Se
  name = G4_Se
  specific = 4
FEATURE [App::DocumentObjectGroupPython] Br_element007  label="Br_element : 004"  # scripted group (container) (typed FeaturePython)
  n = 1
  ref = Br_element
FEATURE [App::DocumentObjectGroupPython] G4_Br  # scripted group (container) (typed FeaturePython)
  Dunit = g/cm3
  Dvalue = 0.0070721
  Group = -> [Br_element007]
  conduct = 2
  density = 1
  expand = 3
  formula = Br
  name = G4_Br
  specific = 4
FEATURE [App::DocumentObjectGroupPython] Kr_element001  label="Kr_element : 1"  # scripted group (container) (typed FeaturePython)
  n = 1
  ref = Kr_element
FEATURE [App::DocumentObjectGroupPython] G4_Kr  # scripted group (container) (typed FeaturePython)
  Dunit = g/cm3
  Dvalue = 0.00347832
  Group = -> [Kr_element001]
  conduct = 2
  density = 1
  expand = 3
  formula = Kr
  name = G4_Kr
  specific = 4
FEATURE [App::DocumentObjectGroupPython] Rb_element001  label="Rb_element : 1"  # scripted group (container) (typed FeaturePython)
  n = 1
  ref = Rb_element
FEATURE [App::DocumentObjectGroupPython] G4_Rb  # scripted group (container) (typed FeaturePython)
  Dunit = g/cm3
  Dvalue = 1.532
  Group = -> [Rb_element001]
  conduct = 2
  density = 1
  expand = 3
  formula = Rb
  name = G4_Rb
  specific = 4
FEATURE [App::DocumentObjectGroupPython] Sr_element001  label="Sr_element : 1"  # scripted group (container) (typed FeaturePython)
  n = 1
  ref = Sr_element
FEATURE [App::DocumentObjectGroupPython] G4_Sr  # scripted group (container) (typed FeaturePython)
  Dunit = g/cm3
  Dvalue = 2.54
  Group = -> [Sr_element001]
  conduct = 2
  density = 1
  expand = 3
  formula = Sr
  name = G4_Sr
  specific = 4
FEATURE [App::DocumentObjectGroupPython] Y_element001  label="Y_element : 1"  # scripted group (container) (typed FeaturePython)
  n = 1
  ref = Y_element
FEATURE [App::DocumentObjectGroupPython] G4_Y  # scripted group (container) (typed FeaturePython)
  Dunit = g/cm3
  Dvalue = 4.469
  Group = -> [Y_element001]
  conduct = 2
  density = 1
  expand = 3
  formula = Y
  name = G4_Y
  specific = 4
FEATURE [App::DocumentObjectGroupPython] Zr_element001  label="Zr_element : 1"  # scripted group (container) (typed FeaturePython)
  n = 1
  ref = Zr_element
FEATURE [App::DocumentObjectGroupPython] G4_Zr  # scripted group (container) (typed FeaturePython)
  Dunit = g/cm3
  Dvalue = 6.506
  Group = -> [Zr_element001]
  conduct = 2
  density = 1
  expand = 3
  formula = Zr
  name = G4_Zr
  specific = 4
FEATURE [App::DocumentObjectGroupPython] Nb_element001  label="Nb_element : 1"  # scripted group (container) (typed FeaturePython)
  n = 1
  ref = Nb_element
FEATURE [App::DocumentObjectGroupPython] G4_Nb  # scripted group (container) (typed FeaturePython)
  Dunit = g/cm3
  Dvalue = 8.57
  Group = -> [Nb_element001]
  conduct = 2
  density = 1
  expand = 3
  formula = Nb
  name = G4_Nb
  specific = 4
FEATURE [App::DocumentObjectGroupPython] Mo_element001  label="Mo_element : 1"  # scripted group (container) (typed FeaturePython)
  n = 1
  ref = Mo_element
FEATURE [App::DocumentObjectGroupPython] G4_Mo  # scripted group (container) (typed FeaturePython)
  Dunit = g/cm3
  Dvalue = 10.22
  Group = -> [Mo_element001]
  conduct = 2
  density = 1
  expand = 3
  formula = Mo
  name = G4_Mo
  specific = 4
FEATURE [App::DocumentObjectGroupPython] Tc_element001  label="Tc_element : 1"  # scripted group (container) (typed FeaturePython)
  n = 1
  ref = Tc_element
FEATURE [App::DocumentObjectGroupPython] G4_Tc  # scripted group (container) (typed FeaturePython)
  Dunit = g/cm3
  Dvalue = 11.5
  Group = -> [Tc_element001]
  conduct = 2
  density = 1
  expand = 3
  formula = Tc
  name = G4_Tc
  specific = 4
FEATURE [App::DocumentObjectGroupPython] Ru_element001  label="Ru_element : 1"  # scripted group (container) (typed FeaturePython)
  n = 1
  ref = Ru_element
FEATURE [App::DocumentObjectGroupPython] G4_Ru  # scripted group (container) (typed FeaturePython)
  Dunit = g/cm3
  Dvalue = 12.41
  Group = -> [Ru_element001]
  conduct = 2
  density = 1
  expand = 3
  formula = Ru
  name = G4_Ru
  specific = 4
FEATURE [App::DocumentObjectGroupPython] Rh_element001  label="Rh_element : 1"  # scripted group (container) (typed FeaturePython)
  n = 1
  ref = Rh_element
FEATURE [App::DocumentObjectGroupPython] G4_Rh  # scripted group (container) (typed FeaturePython)
  Dunit = g/cm3
  Dvalue = 12.41
  Group = -> [Rh_element001]
  conduct = 2
  density = 1
  expand = 3
  formula = Rh
  name = G4_Rh
  specific = 4
FEATURE [App::DocumentObjectGroupPython] Pd_element001  label="Pd_element : 1"  # scripted group (container) (typed FeaturePython)
  n = 1
  ref = Pd_element
FEATURE [App::DocumentObjectGroupPython] G4_Pd  # scripted group (container) (typed FeaturePython)
  Dunit = g/cm3
  Dvalue = 12.02
  Group = -> [Pd_element001]
  conduct = 2
  density = 1
  expand = 3
  formula = Pd
  name = G4_Pd
  specific = 4
FEATURE [App::DocumentObjectGroupPython] Ag_element006  label="Ag_element : 004"  # scripted group (container) (typed FeaturePython)
  n = 1
  ref = Ag_element
FEATURE [App::DocumentObjectGroupPython] G4_Ag  # scripted group (container) (typed FeaturePython)
  Dunit = g/cm3
  Dvalue = 10.5
  Group = -> [Ag_element006]
  conduct = 2
  density = 1
  expand = 3
  formula = Ag
  name = G4_Ag
  specific = 4
FEATURE [App::DocumentObjectGroupPython] Cd_element003  label="Cd_element : 003"  # scripted group (container) (typed FeaturePython)
  n = 1
  ref = Cd_element
FEATURE [App::DocumentObjectGroupPython] G4_Cd  # scripted group (container) (typed FeaturePython)
  Dunit = g/cm3
  Dvalue = 8.65
  Group = -> [Cd_element003]
  conduct = 2
  density = 1
  expand = 3
  formula = Cd
  name = G4_Cd
  specific = 4
FEATURE [App::DocumentObjectGroupPython] In_element001  label="In_element : 1"  # scripted group (container) (typed FeaturePython)
  n = 1
  ref = In_element
FEATURE [App::DocumentObjectGroupPython] G4_In  # scripted group (container) (typed FeaturePython)
  Dunit = g/cm3
  Dvalue = 7.31
  Group = -> [In_element001]
  conduct = 2
  density = 1
  expand = 3
  formula = In
  name = G4_In
  specific = 4
FEATURE [App::DocumentObjectGroupPython] Sn_element001  label="Sn_element : 1"  # scripted group (container) (typed FeaturePython)
  n = 1
  ref = Sn_element
FEATURE [App::DocumentObjectGroupPython] G4_Sn  # scripted group (container) (typed FeaturePython)
  Dunit = g/cm3
  Dvalue = 7.31
  Group = -> [Sn_element001]
  conduct = 2
  density = 1
  expand = 3
  formula = Sn
  name = G4_Sn
  specific = 4
FEATURE [App::DocumentObjectGroupPython] Sb_element001  label="Sb_element : 1"  # scripted group (container) (typed FeaturePython)
  n = 1
  ref = Sb_element
FEATURE [App::DocumentObjectGroupPython] G4_Sb  # scripted group (container) (typed FeaturePython)
  Dunit = g/cm3
  Dvalue = 6.691
  Group = -> [Sb_element001]
  conduct = 2
  density = 1
  expand = 3
  formula = Sb
  name = G4_Sb
  specific = 4
FEATURE [App::DocumentObjectGroupPython] Te_element002  label="Te_element : 002"  # scripted group (container) (typed FeaturePython)
  n = 1
  ref = Te_element
FEATURE [App::DocumentObjectGroupPython] G4_Te  # scripted group (container) (typed FeaturePython)
  Dunit = g/cm3
  Dvalue = 6.24
  Group = -> [Te_element002]
  conduct = 2
  density = 1
  expand = 3
  formula = Te
  name = G4_Te
  specific = 4
FEATURE [App::DocumentObjectGroupPython] I_element010  label="I_element : 006"  # scripted group (container) (typed FeaturePython)
  n = 1
  ref = I_element
FEATURE [App::DocumentObjectGroupPython] G4_I  # scripted group (container) (typed FeaturePython)
  Dunit = g/cm3
  Dvalue = 4.93
  Group = -> [I_element010]
  conduct = 2
  density = 1
  expand = 3
  formula = I
  name = G4_I
  specific = 4
FEATURE [App::DocumentObjectGroupPython] Xe_element001  label="Xe_element : 1"  # scripted group (container) (typed FeaturePython)
  n = 1
  ref = Xe_element
FEATURE [App::DocumentObjectGroupPython] G4_Xe  # scripted group (container) (typed FeaturePython)
  Dunit = g/cm3
  Dvalue = 0.00548536
  Group = -> [Xe_element001]
  conduct = 2
  density = 1
  expand = 3
  formula = Xe
  name = G4_Xe
  specific = 4
FEATURE [App::DocumentObjectGroupPython] Cs_element003  label="Cs_element : 003"  # scripted group (container) (typed FeaturePython)
  n = 1
  ref = Cs_element
FEATURE [App::DocumentObjectGroupPython] G4_Cs  # scripted group (container) (typed FeaturePython)
  Dunit = g/cm3
  Dvalue = 1.873
  Group = -> [Cs_element003]
  conduct = 2
  density = 1
  expand = 3
  formula = Cs
  name = G4_Cs
  specific = 4
FEATURE [App::DocumentObjectGroupPython] Ba_element003  label="Ba_element : 003"  # scripted group (container) (typed FeaturePython)
  n = 1
  ref = Ba_element
FEATURE [App::DocumentObjectGroupPython] G4_Ba  # scripted group (container) (typed FeaturePython)
  Dunit = g/cm3
  Dvalue = 3.5
  Group = -> [Ba_element003]
  conduct = 2
  density = 1
  expand = 3
  formula = Ba
  name = G4_Ba
  specific = 4
FEATURE [App::DocumentObjectGroupPython] La_element003  label="La_element : 003"  # scripted group (container) (typed FeaturePython)
  n = 1
  ref = La_element
FEATURE [App::DocumentObjectGroupPython] G4_La  # scripted group (container) (typed FeaturePython)
  Dunit = g/cm3
  Dvalue = 6.154
  Group = -> [La_element003]
  conduct = 2
  density = 1
  expand = 3
  formula = La
  name = G4_La
  specific = 4
FEATURE [App::DocumentObjectGroupPython] Ce_element002  label="Ce_element : 1"  # scripted group (container) (typed FeaturePython)
  n = 1
  ref = Ce_element
FEATURE [App::DocumentObjectGroupPython] G4_Ce  # scripted group (container) (typed FeaturePython)
  Dunit = g/cm3
  Dvalue = 6.657
  Group = -> [Ce_element002]
  conduct = 2
  density = 1
  expand = 3
  formula = Ce
  name = G4_Ce
  specific = 4
FEATURE [App::DocumentObjectGroupPython] Pr_element001  label="Pr_element : 1"  # scripted group (container) (typed FeaturePython)
  n = 1
  ref = Pr_element
FEATURE [App::DocumentObjectGroupPython] G4_Pr  # scripted group (container) (typed FeaturePython)
  Dunit = g/cm3
  Dvalue = 6.71
  Group = -> [Pr_element001]
  conduct = 2
  density = 1
  expand = 3
  formula = Pr
  name = G4_Pr
  specific = 4
FEATURE [App::DocumentObjectGroupPython] Nd_element001  label="Nd_element : 1"  # scripted group (container) (typed FeaturePython)
  n = 1
  ref = Nd_element
FEATURE [App::DocumentObjectGroupPython] G4_Nd  # scripted group (container) (typed FeaturePython)
  Dunit = g/cm3
  Dvalue = 6.9
  Group = -> [Nd_element001]
  conduct = 2
  density = 1
  expand = 3
  formula = Nd
  name = G4_Nd
  specific = 4
FEATURE [App::DocumentObjectGroupPython] Pm_element001  label="Pm_element : 1"  # scripted group (container) (typed FeaturePython)
  n = 1
  ref = Pm_element
FEATURE [App::DocumentObjectGroupPython] G4_Pm  # scripted group (container) (typed FeaturePython)
  Dunit = g/cm3
  Dvalue = 7.22
  Group = -> [Pm_element001]
  conduct = 2
  density = 1
  expand = 3
  formula = Pm
  name = G4_Pm
  specific = 4
FEATURE [App::DocumentObjectGroupPython] Sm_element001  label="Sm_element : 1"  # scripted group (container) (typed FeaturePython)
  n = 1
  ref = Sm_element
FEATURE [App::DocumentObjectGroupPython] G4_Sm  # scripted group (container) (typed FeaturePython)
  Dunit = g/cm3
  Dvalue = 7.46
  Group = -> [Sm_element001]
  conduct = 2
  density = 1
  expand = 3
  formula = Sm
  name = G4_Sm
  specific = 4
FEATURE [App::DocumentObjectGroupPython] Eu_element001  label="Eu_element : 1"  # scripted group (container) (typed FeaturePython)
  n = 1
  ref = Eu_element
FEATURE [App::DocumentObjectGroupPython] G4_Eu  # scripted group (container) (typed FeaturePython)
  Dunit = g/cm3
  Dvalue = 5.243
  Group = -> [Eu_element001]
  conduct = 2
  density = 1
  expand = 3
  formula = Eu
  name = G4_Eu
  specific = 4
FEATURE [App::DocumentObjectGroupPython] Gd_element002  label="Gd_element : 1"  # scripted group (container) (typed FeaturePython)
  n = 1
  ref = Gd_element
FEATURE [App::DocumentObjectGroupPython] G4_Gd  # scripted group (container) (typed FeaturePython)
  Dunit = g/cm3
  Dvalue = 7.9004
  Group = -> [Gd_element002]
  conduct = 2
  density = 1
  expand = 3
  formula = Gd
  name = G4_Gd
  specific = 4
FEATURE [App::DocumentObjectGroupPython] Tb_element001  label="Tb_element : 1"  # scripted group (container) (typed FeaturePython)
  n = 1
  ref = Tb_element
FEATURE [App::DocumentObjectGroupPython] G4_Tb  # scripted group (container) (typed FeaturePython)
  Dunit = g/cm3
  Dvalue = 8.229
  Group = -> [Tb_element001]
  conduct = 2
  density = 1
  expand = 3
  formula = Tb
  name = G4_Tb
  specific = 4
FEATURE [App::DocumentObjectGroupPython] Dy_element001  label="Dy_element : 1"  # scripted group (container) (typed FeaturePython)
  n = 1
  ref = Dy_element
FEATURE [App::DocumentObjectGroupPython] G4_Dy  # scripted group (container) (typed FeaturePython)
  Dunit = g/cm3
  Dvalue = 8.55
  Group = -> [Dy_element001]
  conduct = 2
  density = 1
  expand = 3
  formula = Dy
  name = G4_Dy
  specific = 4
FEATURE [App::DocumentObjectGroupPython] Ho_element001  label="Ho_element : 1"  # scripted group (container) (typed FeaturePython)
  n = 1
  ref = Ho_element
FEATURE [App::DocumentObjectGroupPython] G4_Ho  # scripted group (container) (typed FeaturePython)
  Dunit = g/cm3
  Dvalue = 8.795
  Group = -> [Ho_element001]
  conduct = 2
  density = 1
  expand = 3
  formula = Ho
  name = G4_Ho
  specific = 4
FEATURE [App::DocumentObjectGroupPython] Er_element001  label="Er_element : 1"  # scripted group (container) (typed FeaturePython)
  n = 1
  ref = Er_element
FEATURE [App::DocumentObjectGroupPython] G4_Er  # scripted group (container) (typed FeaturePython)
  Dunit = g/cm3
  Dvalue = 9.066
  Group = -> [Er_element001]
  conduct = 2
  density = 1
  expand = 3
  formula = Er
  name = G4_Er
  specific = 4
FEATURE [App::DocumentObjectGroupPython] Tm_element001  label="Tm_element : 1"  # scripted group (container) (typed FeaturePython)
  n = 1
  ref = Tm_element
FEATURE [App::DocumentObjectGroupPython] G4_Tm  # scripted group (container) (typed FeaturePython)
  Dunit = g/cm3
  Dvalue = 9.321
  Group = -> [Tm_element001]
  conduct = 2
  density = 1
  expand = 3
  formula = Tm
  name = G4_Tm
  specific = 4
FEATURE [App::DocumentObjectGroupPython] Yb_element001  label="Yb_element : 1"  # scripted group (container) (typed FeaturePython)
  n = 1
  ref = Yb_element
FEATURE [App::DocumentObjectGroupPython] G4_Yb  # scripted group (container) (typed FeaturePython)
  Dunit = g/cm3
  Dvalue = 6.73
  Group = -> [Yb_element001]
  conduct = 2
  density = 1
  expand = 3
  formula = Yb
  name = G4_Yb
  specific = 4
FEATURE [App::DocumentObjectGroupPython] Lu_element001  label="Lu_element : 1"  # scripted group (container) (typed FeaturePython)
  n = 1
  ref = Lu_element
FEATURE [App::DocumentObjectGroupPython] G4_Lu  # scripted group (container) (typed FeaturePython)
  Dunit = g/cm3
  Dvalue = 9.84
  Group = -> [Lu_element001]
  conduct = 2
  density = 1
  expand = 3
  formula = Lu
  name = G4_Lu
  specific = 4
FEATURE [App::DocumentObjectGroupPython] Hf_element001  label="Hf_element : 1"  # scripted group (container) (typed FeaturePython)
  n = 1
  ref = Hf_element
FEATURE [App::DocumentObjectGroupPython] G4_Hf  # scripted group (container) (typed FeaturePython)
  Dunit = g/cm3
  Dvalue = 13.31
  Group = -> [Hf_element001]
  conduct = 2
  density = 1
  expand = 3
  formula = Hf
  name = G4_Hf
  specific = 4
FEATURE [App::DocumentObjectGroupPython] Ta_element001  label="Ta_element : 1"  # scripted group (container) (typed FeaturePython)
  n = 1
  ref = Ta_element
FEATURE [App::DocumentObjectGroupPython] G4_Ta  # scripted group (container) (typed FeaturePython)
  Dunit = g/cm3
  Dvalue = 16.654
  Group = -> [Ta_element001]
  conduct = 2
  density = 1
  expand = 3
  formula = Ta
  name = G4_Ta
  specific = 4
FEATURE [App::DocumentObjectGroupPython] W_element004  label="W_element : 004"  # scripted group (container) (typed FeaturePython)
  n = 1
  ref = W_element
FEATURE [App::DocumentObjectGroupPython] G4_W  # scripted group (container) (typed FeaturePython)
  Dunit = g/cm3
  Dvalue = 19.3
  Group = -> [W_element004]
  conduct = 2
  density = 1
  expand = 3
  formula = W
  name = G4_W
  specific = 4
FEATURE [App::DocumentObjectGroupPython] Re_element001  label="Re_element : 1"  # scripted group (container) (typed FeaturePython)
  n = 1
  ref = Re_element
FEATURE [App::DocumentObjectGroupPython] G4_Re  # scripted group (container) (typed FeaturePython)
  Dunit = g/cm3
  Dvalue = 21.02
  Group = -> [Re_element001]
  conduct = 2
  density = 1
  expand = 3
  formula = Re
  name = G4_Re
  specific = 4
FEATURE [App::DocumentObjectGroupPython] Os_element001  label="Os_element : 1"  # scripted group (container) (typed FeaturePython)
  n = 1
  ref = Os_element
FEATURE [App::DocumentObjectGroupPython] G4_Os  # scripted group (container) (typed FeaturePython)
  Dunit = g/cm3
  Dvalue = 22.57
  Group = -> [Os_element001]
  conduct = 2
  density = 1
  expand = 3
  formula = Os
  name = G4_Os
  specific = 4
FEATURE [App::DocumentObjectGroupPython] Ir_element001  label="Ir_element : 1"  # scripted group (container) (typed FeaturePython)
  n = 1
  ref = Ir_element
FEATURE [App::DocumentObjectGroupPython] G4_Ir  # scripted group (container) (typed FeaturePython)
  Dunit = g/cm3
  Dvalue = 22.42
  Group = -> [Ir_element001]
  conduct = 2
  density = 1
  expand = 3
  formula = Ir
  name = G4_Ir
  specific = 4
FEATURE [App::DocumentObjectGroupPython] Pt_element001  label="Pt_element : 1"  # scripted group (container) (typed FeaturePython)
  n = 1
  ref = Pt_element
FEATURE [App::DocumentObjectGroupPython] G4_Pt  # scripted group (container) (typed FeaturePython)
  Dunit = g/cm3
  Dvalue = 21.45
  Group = -> [Pt_element001]
  conduct = 2
  density = 1
  expand = 3
  formula = Pt
  name = G4_Pt
  specific = 4
FEATURE [App::DocumentObjectGroupPython] Au_element001  label="Au_element : 1"  # scripted group (container) (typed FeaturePython)
  n = 1
  ref = Au_element
FEATURE [App::DocumentObjectGroupPython] G4_Au  # scripted group (container) (typed FeaturePython)
  Dunit = g/cm3
  Dvalue = 19.32
  Group = -> [Au_element001]
  conduct = 2
  density = 1
  expand = 3
  formula = Au
  name = G4_Au
  specific = 4
FEATURE [App::DocumentObjectGroupPython] Hg_element002  label="Hg_element : 002"  # scripted group (container) (typed FeaturePython)
  n = 1
  ref = Hg_element
FEATURE [App::DocumentObjectGroupPython] G4_Hg  # scripted group (container) (typed FeaturePython)
  Dunit = g/cm3
  Dvalue = 13.546
  Group = -> [Hg_element002]
  conduct = 2
  density = 1
  expand = 3
  formula = Hg
  name = G4_Hg
  specific = 4
FEATURE [App::DocumentObjectGroupPython] Tl_element002  label="Tl_element : 002"  # scripted group (container) (typed FeaturePython)
  n = 1
  ref = Tl_element
FEATURE [App::DocumentObjectGroupPython] G4_Tl  # scripted group (container) (typed FeaturePython)
  Dunit = g/cm3
  Dvalue = 11.72
  Group = -> [Tl_element002]
  conduct = 2
  density = 1
  expand = 3
  formula = Tl
  name = G4_Tl
  specific = 4
FEATURE [App::DocumentObjectGroupPython] Pb_element003  label="Pb_element : 1"  # scripted group (container) (typed FeaturePython)
  n = 1
  ref = Pb_element
FEATURE [App::DocumentObjectGroupPython] G4_Pb  # scripted group (container) (typed FeaturePython)
  Dunit = g/cm3
  Dvalue = 11.35
  Group = -> [Pb_element003]
  conduct = 2
  density = 1
  expand = 3
  formula = Pb
  name = G4_Pb
  specific = 4
FEATURE [App::DocumentObjectGroupPython] Bi_element002  label="Bi_element : 1"  # scripted group (container) (typed FeaturePython)
  n = 1
  ref = Bi_element
FEATURE [App::DocumentObjectGroupPython] G4_Bi  # scripted group (container) (typed FeaturePython)
  Dunit = g/cm3
  Dvalue = 9.747
  Group = -> [Bi_element002]
  conduct = 2
  density = 1
  expand = 3
  formula = Bi
  name = G4_Bi
  specific = 4
FEATURE [App::DocumentObjectGroupPython] Po_element001  label="Po_element : 1"  # scripted group (container) (typed FeaturePython)
  n = 1
  ref = Po_element
FEATURE [App::DocumentObjectGroupPython] G4_Po  # scripted group (container) (typed FeaturePython)
  Dunit = g/cm3
  Dvalue = 9.32
  Group = -> [Po_element001]
  conduct = 2
  density = 1
  expand = 3
  formula = Po
  name = G4_Po
  specific = 4
FEATURE [App::DocumentObjectGroupPython] At_element001  label="At_element : 1"  # scripted group (container) (typed FeaturePython)
  n = 1
  ref = At_element
FEATURE [App::DocumentObjectGroupPython] G4_At  # scripted group (container) (typed FeaturePython)
  Dunit = g/cm3
  Dvalue = 9.32
  Group = -> [At_element001]
  conduct = 2
  density = 1
  expand = 3
  formula = At
  name = G4_At
  specific = 4
FEATURE [App::DocumentObjectGroupPython] Rn_element001  label="Rn_element : 1"  # scripted group (container) (typed FeaturePython)
  n = 1
  ref = Rn_element
FEATURE [App::DocumentObjectGroupPython] G4_Rn  # scripted group (container) (typed FeaturePython)
  Dunit = g/cm3
  Dvalue = 0.00900662
  Group = -> [Rn_element001]
  conduct = 2
  density = 1
  expand = 3
  formula = Rn
  name = G4_Rn
  specific = 4
FEATURE [App::DocumentObjectGroupPython] Fr_element001  label="Fr_element : 1"  # scripted group (container) (typed FeaturePython)
  n = 1
  ref = Fr_element
FEATURE [App::DocumentObjectGroupPython] G4_Fr  # scripted group (container) (typed FeaturePython)
  Dunit = g/cm3
  Dvalue = 1
  Group = -> [Fr_element001]
  conduct = 2
  density = 1
  expand = 3
  formula = Fr
  name = G4_Fr
  specific = 4
FEATURE [App::DocumentObjectGroupPython] Ra_element001  label="Ra_element : 1"  # scripted group (container) (typed FeaturePython)
  n = 1
  ref = Ra_element
FEATURE [App::DocumentObjectGroupPython] G4_Ra  # scripted group (container) (typed FeaturePython)
  Dunit = g/cm3
  Dvalue = 5
  Group = -> [Ra_element001]
  conduct = 2
  density = 1
  expand = 3
  formula = Ra
  name = G4_Ra
  specific = 4
FEATURE [App::DocumentObjectGroupPython] Ac_element001  label="Ac_element : 1"  # scripted group (container) (typed FeaturePython)
  n = 1
  ref = Ac_element
FEATURE [App::DocumentObjectGroupPython] G4_Ac  # scripted group (container) (typed FeaturePython)
  Dunit = g/cm3
  Dvalue = 10.07
  Group = -> [Ac_element001]
  conduct = 2
  density = 1
  expand = 3
  formula = Ac
  name = G4_Ac
  specific = 4
FEATURE [App::DocumentObjectGroupPython] Th_element001  label="Th_element : 1"  # scripted group (container) (typed FeaturePython)
  n = 1
  ref = Th_element
FEATURE [App::DocumentObjectGroupPython] G4_Th  # scripted group (container) (typed FeaturePython)
  Dunit = g/cm3
  Dvalue = 11.72
  Group = -> [Th_element001]
  conduct = 2
  density = 1
  expand = 3
  formula = Th
  name = G4_Th
  specific = 4
FEATURE [App::DocumentObjectGroupPython] Pa_element001  label="Pa_element : 1"  # scripted group (container) (typed FeaturePython)
  n = 1
  ref = Pa_element
FEATURE [App::DocumentObjectGroupPython] G4_Pa  # scripted group (container) (typed FeaturePython)
  Dunit = g/cm3
  Dvalue = 15.37
  Group = -> [Pa_element001]
  conduct = 2
  density = 1
  expand = 3
  formula = Pa
  name = G4_Pa
  specific = 4
FEATURE [App::DocumentObjectGroupPython] U_element004  label="U_element : 004"  # scripted group (container) (typed FeaturePython)
  n = 1
  ref = U_element
FEATURE [App::DocumentObjectGroupPython] G4_U  # scripted group (container) (typed FeaturePython)
  Dunit = g/cm3
  Dvalue = 18.95
  Group = -> [U_element004]
  conduct = 2
  density = 1
  expand = 3
  formula = U
  name = G4_U
  specific = 4
FEATURE [App::DocumentObjectGroupPython] Np_element001  label="Np_element : 1"  # scripted group (container) (typed FeaturePython)
  n = 1
  ref = Np_element
FEATURE [App::DocumentObjectGroupPython] G4_Np  # scripted group (container) (typed FeaturePython)
  Dunit = g/cm3
  Dvalue = 20.25
  Group = -> [Np_element001]
  conduct = 2
  density = 1
  expand = 3
  formula = Np
  name = G4_Np
  specific = 4
FEATURE [App::DocumentObjectGroupPython] Pu_element002  label="Pu_element : 002"  # scripted group (container) (typed FeaturePython)
  n = 1
  ref = Pu_element
FEATURE [App::DocumentObjectGroupPython] G4_Pu  # scripted group (container) (typed FeaturePython)
  Dunit = g/cm3
  Dvalue = 19.84
  Group = -> [Pu_element002]
  conduct = 2
  density = 1
  expand = 3
  formula = Pu
  name = G4_Pu
  specific = 4
FEATURE [App::DocumentObjectGroupPython] Am_element001  label="Am_element : 1"  # scripted group (container) (typed FeaturePython)
  n = 1
  ref = Am_element
FEATURE [App::DocumentObjectGroupPython] G4_Am  # scripted group (container) (typed FeaturePython)
  Dunit = g/cm3
  Dvalue = 13.67
  Group = -> [Am_element001]
  conduct = 2
  density = 1
  expand = 3
  formula = Am
  name = G4_Am
  specific = 4
FEATURE [App::DocumentObjectGroupPython] Cm_element001  label="Cm_element : 1"  # scripted group (container) (typed FeaturePython)
  n = 1
  ref = Cm_element
FEATURE [App::DocumentObjectGroupPython] G4_Cm  # scripted group (container) (typed FeaturePython)
  Dunit = g/cm3
  Dvalue = 13.51
  Group = -> [Cm_element001]
  conduct = 2
  density = 1
  expand = 3
  formula = Cm
  name = G4_Cm
  specific = 4
FEATURE [App::DocumentObjectGroupPython] Bk_element001  label="Bk_element : 1"  # scripted group (container) (typed FeaturePython)
  n = 1
  ref = Bk_element
FEATURE [App::DocumentObjectGroupPython] G4_Bk  # scripted group (container) (typed FeaturePython)
  Dunit = g/cm3
  Dvalue = 14
  Group = -> [Bk_element001]
  conduct = 2
  density = 1
  expand = 3
  formula = Bk
  name = G4_Bk
  specific = 4
FEATURE [App::DocumentObjectGroupPython] Cf_element001  label="Cf_element : 1"  # scripted group (container) (typed FeaturePython)
  n = 1
  ref = Cf_element
FEATURE [App::DocumentObjectGroupPython] G4_Cf  # scripted group (container) (typed FeaturePython)
  Dunit = g/cm3
  Dvalue = 10
  Group = -> [Cf_element001]
  conduct = 2
  density = 1
  expand = 3
  formula = Cf
  name = G4_Cf
  specific = 4
FEATURE [App::DocumentObjectGroupPython] Element  # scripted group (container) (typed FeaturePython)
  Group = -> [G4_H,G4_He,G4_Li,G4_Be,G4_B,G4_C,G4_N,G4_O,G4_F,G4_Ne,G4_Na,G4_Mg,G4_Al,G4_Si,G4_P,G4_S,G4_Cl,G4_Ar,G4_K,G4_Ca,G4_Sc,G4_Ti,G4_V,G4_Cr,G4_Mn,G4_Fe,G4_Co,G4_Ni,G4_Cu,G4_Zn,G4_Ga,G4_Ge,G4_As,G4_Se,G4_Br,G4_Kr,G4_Rb,G4_Sr,G4_Y,G4_Zr,G4_Nb,G4_Mo,G4_Tc,G4_Ru,G4_Rh,G4_Pd,G4_Ag,G4_Cd,G4_In,G4_Sn,G4_Sb,G4_Te,G4_I,G4_Xe,G4_Cs,G4_Ba,G4_La,G4_Ce,G4_Pr,G4_Nd,G4_Pm,G4_Sm,G4_Eu,G4_Gd,G4_Tb,G4_Dy,G4_Ho,G4_Er,+30 more]
FEATURE [App::DocumentObjectGroupPython] H_element114  label="H_element : 063"  # scripted group (container) (typed FeaturePython)
  n = 2
  ref = H_element
FEATURE [App::DocumentObjectGroupPython] G4_lH2  # scripted group (container) (typed FeaturePython)
  Dunit = g/cm3
  Dvalue = 0.0708
  Group = -> [H_element114]
  conduct = 2
  density = 1
  expand = 3
  formula = G4_lH2
  name = G4_lH2
  specific = 4
FEATURE [App::DocumentObjectGroupPython] N_element049  label="N_element : 022"  # scripted group (container) (typed FeaturePython)
  n = 2
  ref = N_element
FEATURE [App::DocumentObjectGroupPython] G4_lN2  # scripted group (container) (typed FeaturePython)
  Dunit = g/cm3
  Dvalue = 0.807
  Group = -> [N_element049]
  conduct = 2
  density = 1
  expand = 3
  formula = G4_lN2
  name = G4_lN2
  specific = 4
FEATURE [App::DocumentObjectGroupPython] O_element106  label="O_element : 060"  # scripted group (container) (typed FeaturePython)
  n = 2
  ref = O_element
FEATURE [App::DocumentObjectGroupPython] G4_lO2  # scripted group (container) (typed FeaturePython)
  Dunit = g/cm3
  Dvalue = 1.141
  Group = -> [O_element106]
  conduct = 2
  density = 1
  expand = 3
  formula = G4_lO2
  name = G4_lO2
  specific = 4
FEATURE [App::DocumentObjectGroupPython] Ar  label="Ar : 1"  # scripted group (container) (typed FeaturePython)
  n = 1
  ref = Ar
FEATURE [App::DocumentObjectGroupPython] G4_lAr  # scripted group (container) (typed FeaturePython)
  Dunit = g/cm3
  Dvalue = 1.396
  Group = -> [Ar]
  conduct = 2
  density = 1
  expand = 3
  formula = G4_lAr
  name = G4_lAr
  specific = 4
FEATURE [App::DocumentObjectGroupPython] Br  label="Br : 1"  # scripted group (container) (typed FeaturePython)
  n = 1
  ref = Br
FEATURE [App::DocumentObjectGroupPython] G4_lBr  # scripted group (container) (typed FeaturePython)
  Dunit = g/cm3
  Dvalue = 3.1028
  Group = -> [Br]
  conduct = 2
  density = 1
  expand = 3
  formula = G4_lBr
  name = G4_lBr
  specific = 4
FEATURE [App::DocumentObjectGroupPython] Kr  label="Kr : 1"  # scripted group (container) (typed FeaturePython)
  n = 1
  ref = Kr
FEATURE [App::DocumentObjectGroupPython] G4_lKr  # scripted group (container) (typed FeaturePython)
  Dunit = g/cm3
  Dvalue = 2.418
  Group = -> [Kr]
  conduct = 2
  density = 1
  expand = 3
  formula = G4_lKr
  name = G4_lKr
  specific = 4
FEATURE [App::DocumentObjectGroupPython] Xe  label="Xe : 1"  # scripted group (container) (typed FeaturePython)
  n = 1
  ref = Xe
FEATURE [App::DocumentObjectGroupPython] G4_lXe  # scripted group (container) (typed FeaturePython)
  Dunit = g/cm3
  Dvalue = 2.953
  Group = -> [Xe]
  conduct = 2
  density = 1
  expand = 3
  formula = G4_lXe
  name = G4_lXe
  specific = 4
FEATURE [App::DocumentObjectGroupPython] O_element107  label="O_element : 061"  # scripted group (container) (typed FeaturePython)
  n = 4
  ref = O_element
FEATURE [App::DocumentObjectGroupPython] Pb_element004  label="Pb_element : 002"  # scripted group (container) (typed FeaturePython)
  n = 1
  ref = Pb_element
FEATURE [App::DocumentObjectGroupPython] W_element005  label="W_element : 005"  # scripted group (container) (typed FeaturePython)
  n = 1
  ref = W_element
FEATURE [App::DocumentObjectGroupPython] G4_PbWO4  # scripted group (container) (typed FeaturePython)
  Dunit = g/cm3
  Dvalue = 8.28
  Group = -> [O_element107,Pb_element004,W_element005]
  conduct = 2
  density = 1
  expand = 3
  formula = G4_PbWO4
  name = G4_PbWO4
  specific = 4
FEATURE [App::DocumentObjectGroupPython] alactic  label="alactic : 1"  # scripted group (container) (typed FeaturePython)
  n = 1
  ref = alactic
FEATURE [App::DocumentObjectGroupPython] G4_Galactic  # scripted group (container) (typed FeaturePython)
  Dunit = g/cm3
  Dvalue = 0
  Group = -> [alactic]
  conduct = 2
  density = 1
  expand = 3
  formula = G4_Galactic
  name = G4_Galactic
  specific = 4
FEATURE [App::DocumentObjectGroupPython] RAPHITE_POROUS  label="RAPHITE_POROUS : 1"  # scripted group (container) (typed FeaturePython)
  n = 1
  ref = RAPHITE_POROUS
FEATURE [App::DocumentObjectGroupPython] G4_GRAPHITE_POROUS  # scripted group (container) (typed FeaturePython)
  Dunit = g/cm3
  Dvalue = 1.7
  Group = -> [RAPHITE_POROUS]
  conduct = 2
  density = 1
  expand = 3
  formula = G4_GRAPHITE_POROUS
  name = G4_GRAPHITE_POROUS
  specific = 4
FEATURE [App::DocumentObjectGroupPython] H_element115  label="H_element : 0.150"  # scripted group (container) (typed FeaturePython)
  n = 0.080538
FEATURE [App::DocumentObjectGroupPython] C_element125  label="C_element : 0.600"  # scripted group (container) (typed FeaturePython)
  n = 0.599848
FEATURE [App::DocumentObjectGroupPython] O_element108  label="O_element : 0.320"  # scripted group (container) (typed FeaturePython)
  n = 0.319614
FEATURE [App::DocumentObjectGroupPython] G4_LUCITE  # scripted group (container) (typed FeaturePython)
  Dunit = g/cm3
  Dvalue = 1.19
  Group = -> [H_element115,C_element125,O_element108]
  conduct = 2
  density = 1
  expand = 3
  formula = G4_LUCITE
  name = G4_LUCITE
  specific = 4
FEATURE [App::DocumentObjectGroupPython] Cu_element002  label="Cu_element : 62"  # scripted group (container) (typed FeaturePython)
  n = 62
  ref = Cu_element
FEATURE [App::DocumentObjectGroupPython] Zn_element002  label="Zn_element : 35"  # scripted group (container) (typed FeaturePython)
  n = 35
  ref = Zn_element
FEATURE [App::DocumentObjectGroupPython] Pb_element005  label="Pb_element : 3"  # scripted group (container) (typed FeaturePython)
  n = 3
  ref = Pb_element
FEATURE [App::DocumentObjectGroupPython] G4_BRASS  # scripted group (container) (typed FeaturePython)
  Dunit = g/cm3
  Dvalue = 8.52
  Group = -> [Cu_element002,Zn_element002,Pb_element005]
  conduct = 2
  density = 1
  expand = 3
  formula = G4_BRASS
  name = G4_BRASS
  specific = 4
FEATURE [App::DocumentObjectGroupPython] Cu_element003  label="Cu_element : 89"  # scripted group (container) (typed FeaturePython)
  n = 89
  ref = Cu_element
FEATURE [App::DocumentObjectGroupPython] Zn_element003  label="Zn_element : 9"  # scripted group (container) (typed FeaturePython)
  n = 9
  ref = Zn_element
FEATURE [App::DocumentObjectGroupPython] Pb_element006  label="Pb_element : 2"  # scripted group (container) (typed FeaturePython)
  n = 2
  ref = Pb_element
FEATURE [App::DocumentObjectGroupPython] G4_BRONZE  # scripted group (container) (typed FeaturePython)
  Dunit = g/cm3
  Dvalue = 8.82
  Group = -> [Cu_element003,Zn_element003,Pb_element006]
  conduct = 2
  density = 1
  expand = 3
  formula = G4_BRONZE
  name = G4_BRONZE
  specific = 4
FEATURE [App::DocumentObjectGroupPython] Fe_element008  label="Fe_element : 74"  # scripted group (container) (typed FeaturePython)
  n = 74
  ref = Fe_element
FEATURE [App::DocumentObjectGroupPython] Cr_element002  label="Cr_element : 18"  # scripted group (container) (typed FeaturePython)
  n = 18
  ref = Cr_element
FEATURE [App::DocumentObjectGroupPython] Ni_element002  label="Ni_element : 8"  # scripted group (container) (typed FeaturePython)
  n = 8
  ref = Ni_element
FEATURE [App::DocumentObjectGroupPython] G4_STAINLESS_STEEL  label="G4_STAINLESS-STEEL"  # scripted group (container) (typed FeaturePython)
  Dunit = g/cm3
  Dvalue = 8
  Group = -> [Fe_element008,Cr_element002,Ni_element002]
  conduct = 2
  density = 1
  expand = 3
  formula = G4_STAINLESS-STEEL
  name = G4_STAINLESS-STEEL
  specific = 4
FEATURE [App::DocumentObjectGroupPython] H_element116  label="H_element : 064"  # scripted group (container) (typed FeaturePython)
  n = 18
  ref = H_element
FEATURE [App::DocumentObjectGroupPython] C_element126  label="C_element : 071"  # scripted group (container) (typed FeaturePython)
  n = 12
  ref = C_element
FEATURE [App::DocumentObjectGroupPython] O_element109  label="O_element : 062"  # scripted group (container) (typed FeaturePython)
  n = 7
  ref = O_element
FEATURE [App::DocumentObjectGroupPython] G4_CR39  # scripted group (container) (typed FeaturePython)
  Dunit = g/cm3
  Dvalue = 1.32
  Group = -> [H_element116,C_element126,O_element109]
  conduct = 2
  density = 1
  expand = 3
  formula = G4_CR39
  name = G4_CR39
  specific = 4
FEATURE [App::DocumentObjectGroupPython] H_element117  label="H_element : 38"  # scripted group (container) (typed FeaturePython)
  n = 38
  ref = H_element
FEATURE [App::DocumentObjectGroupPython] C_element127  label="C_element : 072"  # scripted group (container) (typed FeaturePython)
  n = 18
  ref = C_element
FEATURE [App::DocumentObjectGroupPython] O_element110  label="O_element : 063"  # scripted group (container) (typed FeaturePython)
  n = 1
  ref = O_element
FEATURE [App::DocumentObjectGroupPython] G4_OCTADECANOL  # scripted group (container) (typed FeaturePython)
  Dunit = g/cm3
  Dvalue = 0.812
  Group = -> [H_element117,C_element127,O_element110]
  conduct = 2
  density = 1
  expand = 3
  formula = G4_OCTADECANOL
  name = G4_OCTADECANOL
  specific = 4
FEATURE [App::DocumentObjectGroupPython] HEP  # scripted group (container) (typed FeaturePython)
  Group = -> [G4_lH2,G4_lN2,G4_lO2,G4_lAr,G4_lBr,G4_lKr,G4_lXe,G4_PbWO4,G4_Galactic,G4_GRAPHITE_POROUS,G4_LUCITE,G4_BRASS,G4_BRONZE,G4_STAINLESS_STEEL,G4_CR39,G4_OCTADECANOL]
FEATURE [App::DocumentObjectGroupPython] C_element128  label="C_element : 073"  # scripted group (container) (typed FeaturePython)
  n = 14
  ref = C_element
FEATURE [App::DocumentObjectGroupPython] H_element118  label="H_element : 065"  # scripted group (container) (typed FeaturePython)
  n = 10
  ref = H_element
FEATURE [App::DocumentObjectGroupPython] O_element111  label="O_element : 064"  # scripted group (container) (typed FeaturePython)
  n = 2
  ref = O_element
FEATURE [App::DocumentObjectGroupPython] N_element050  label="N_element : 023"  # scripted group (container) (typed FeaturePython)
  n = 2
  ref = N_element
FEATURE [App::DocumentObjectGroupPython] G4_KEVLAR  # scripted group (container) (typed FeaturePython)
  Dunit = g/cm3
  Dvalue = 1.44
  Group = -> [C_element128,H_element118,O_element111,N_element050]
  conduct = 2
  density = 1
  expand = 3
  formula = G4_KEVLAR
  name = G4_KEVLAR
  specific = 4
FEATURE [App::DocumentObjectGroupPython] C_element129  label="C_element : 074"  # scripted group (container) (typed FeaturePython)
  n = 10
  ref = C_element
FEATURE [App::DocumentObjectGroupPython] H_element119  label="H_element : 066"  # scripted group (container) (typed FeaturePython)
  n = 8
  ref = H_element
FEATURE [App::DocumentObjectGroupPython] O_element112  label="O_element : 065"  # scripted group (container) (typed FeaturePython)
  n = 4
  ref = O_element
FEATURE [App::DocumentObjectGroupPython] G4_DACRON  # scripted group (container) (typed FeaturePython)
  Dunit = g/cm3
  Dvalue = 1.4
  Group = -> [C_element129,H_element119,O_element112]
  conduct = 2
  density = 1
  expand = 3
  formula = G4_DACRON
  name = G4_DACRON
  specific = 4
FEATURE [App::DocumentObjectGroupPython] C_element130  label="C_element : 075"  # scripted group (container) (typed FeaturePython)
  n = 4
  ref = C_element
FEATURE [App::DocumentObjectGroupPython] H_element120  label="H_element : 067"  # scripted group (container) (typed FeaturePython)
  n = 5
  ref = H_element
FEATURE [App::DocumentObjectGroupPython] Cl_element030  label="Cl_element : 016"  # scripted group (container) (typed FeaturePython)
  n = 1
  ref = Cl_element
FEATURE [App::DocumentObjectGroupPython] G4_NEOPRENE  # scripted group (container) (typed FeaturePython)
  Dunit = g/cm3
  Dvalue = 1.23
  Group = -> [C_element130,H_element120,Cl_element030]
  conduct = 2
  density = 1
  expand = 3
  formula = G4_NEOPRENE
  name = G4_NEOPRENE
  specific = 4
FEATURE [App::DocumentObjectGroupPython] Space  # scripted group (container) (typed FeaturePython)
  Group = -> [G4_KEVLAR,G4_DACRON,G4_NEOPRENE]
FEATURE [App::DocumentObjectGroupPython] H_element121  label="H_element : 068"  # scripted group (container) (typed FeaturePython)
  n = 5
  ref = H_element
FEATURE [App::DocumentObjectGroupPython] C_element131  label="C_element : 076"  # scripted group (container) (typed FeaturePython)
  n = 4
  ref = C_element
FEATURE [App::DocumentObjectGroupPython] N_element051  label="N_element : 3"  # scripted group (container) (typed FeaturePython)
  n = 3
  ref = N_element
FEATURE [App::DocumentObjectGroupPython] O_element113  label="O_element : 066"  # scripted group (container) (typed FeaturePython)
  n = 1
  ref = O_element
FEATURE [App::DocumentObjectGroupPython] G4_CYTOSINE  # scripted group (container) (typed FeaturePython)
  Dunit = g/cm3
  Dvalue = 1.55
  Group = -> [H_element121,C_element131,N_element051,O_element113]
  conduct = 2
  density = 1
  expand = 3
  formula = G4_CYTOSINE
  name = G4_CYTOSINE
  specific = 4
FEATURE [App::DocumentObjectGroupPython] H_element122  label="H_element : 069"  # scripted group (container) (typed FeaturePython)
  n = 6
  ref = H_element
FEATURE [App::DocumentObjectGroupPython] C_element132  label="C_element : 077"  # scripted group (container) (typed FeaturePython)
  n = 5
  ref = C_element
FEATURE [App::DocumentObjectGroupPython] N_element052  label="N_element : 024"  # scripted group (container) (typed FeaturePython)
  n = 2
  ref = N_element
FEATURE [App::DocumentObjectGroupPython] O_element114  label="O_element : 067"  # scripted group (container) (typed FeaturePython)
  n = 2
  ref = O_element
FEATURE [App::DocumentObjectGroupPython] G4_THYMINE  # scripted group (container) (typed FeaturePython)
  Dunit = g/cm3
  Dvalue = 1.23
  Group = -> [H_element122,C_element132,N_element052,O_element114]
  conduct = 2
  density = 1
  expand = 3
  formula = G4_THYMINE
  name = G4_THYMINE
  specific = 4
FEATURE [App::DocumentObjectGroupPython] H_element123  label="H_element : 070"  # scripted group (container) (typed FeaturePython)
  n = 4
  ref = H_element
FEATURE [App::DocumentObjectGroupPython] C_element133  label="C_element : 078"  # scripted group (container) (typed FeaturePython)
  n = 4
  ref = C_element
FEATURE [App::DocumentObjectGroupPython] N_element053  label="N_element : 025"  # scripted group (container) (typed FeaturePython)
  n = 2
  ref = N_element
FEATURE [App::DocumentObjectGroupPython] O_element115  label="O_element : 068"  # scripted group (container) (typed FeaturePython)
  n = 2
  ref = O_element
FEATURE [App::DocumentObjectGroupPython] G4_URACIL  # scripted group (container) (typed FeaturePython)
  Dunit = g/cm3
  Dvalue = 1.32
  Group = -> [H_element123,C_element133,N_element053,O_element115]
  conduct = 2
  density = 1
  expand = 3
  formula = G4_URACIL
  name = G4_URACIL
  specific = 4
FEATURE [App::DocumentObjectGroupPython] H_element124  label="H_element : 071"  # scripted group (container) (typed FeaturePython)
  n = 4
  ref = H_element
FEATURE [App::DocumentObjectGroupPython] C_element134  label="C_element : 079"  # scripted group (container) (typed FeaturePython)
  n = 5
  ref = C_element
FEATURE [App::DocumentObjectGroupPython] N_element054  label="N_element : 026"  # scripted group (container) (typed FeaturePython)
  n = 5
  ref = N_element
FEATURE [App::DocumentObjectGroupPython] G4_DNA_ADENINE  # scripted group (container) (typed FeaturePython)
  Dunit = g/cm3
  Dvalue = 1
  Group = -> [H_element124,C_element134,N_element054]
  conduct = 2
  density = 1
  expand = 3
  formula = G4_DNA_ADENINE
  name = G4_DNA_ADENINE
  specific = 4
FEATURE [App::DocumentObjectGroupPython] H_element125  label="H_element : 072"  # scripted group (container) (typed FeaturePython)
  n = 4
  ref = H_element
FEATURE [App::DocumentObjectGroupPython] C_element135  label="C_element : 080"  # scripted group (container) (typed FeaturePython)
  n = 5
  ref = C_element
FEATURE [App::DocumentObjectGroupPython] N_element055  label="N_element : 027"  # scripted group (container) (typed FeaturePython)
  n = 5
  ref = N_element
FEATURE [App::DocumentObjectGroupPython] O_element116  label="O_element : 069"  # scripted group (container) (typed FeaturePython)
  n = 1
  ref = O_element
FEATURE [App::DocumentObjectGroupPython] G4_DNA_GUANINE  # scripted group (container) (typed FeaturePython)
  Dunit = g/cm3
  Dvalue = 1
  Group = -> [H_element125,C_element135,N_element055,O_element116]
  conduct = 2
  density = 1
  expand = 3
  formula = G4_DNA_GUANINE
  name = G4_DNA_GUANINE
  specific = 4
FEATURE [App::DocumentObjectGroupPython] H_element126  label="H_element : 073"  # scripted group (container) (typed FeaturePython)
  n = 4
  ref = H_element
FEATURE [App::DocumentObjectGroupPython] C_element136  label="C_element : 081"  # scripted group (container) (typed FeaturePython)
  n = 4
  ref = C_element
FEATURE [App::DocumentObjectGroupPython] N_element056  label="N_element : 028"  # scripted group (container) (typed FeaturePython)
  n = 3
  ref = N_element
FEATURE [App::DocumentObjectGroupPython] O_element117  label="O_element : 070"  # scripted group (container) (typed FeaturePython)
  n = 1
  ref = O_element
FEATURE [App::DocumentObjectGroupPython] G4_DNA_CYTOSINE  # scripted group (container) (typed FeaturePython)
  Dunit = g/cm3
  Dvalue = 1
  Group = -> [H_element126,C_element136,N_element056,O_element117]
  conduct = 2
  density = 1
  expand = 3
  formula = G4_DNA_CYTOSINE
  name = G4_DNA_CYTOSINE
  specific = 4
FEATURE [App::DocumentObjectGroupPython] H_element127  label="H_element : 074"  # scripted group (container) (typed FeaturePython)
  n = 5
  ref = H_element
FEATURE [App::DocumentObjectGroupPython] C_element137  label="C_element : 082"  # scripted group (container) (typed FeaturePython)
  n = 5
  ref = C_element
FEATURE [App::DocumentObjectGroupPython] N_element057  label="N_element : 029"  # scripted group (container) (typed FeaturePython)
  n = 2
  ref = N_element
FEATURE [App::DocumentObjectGroupPython] O_element118  label="O_element : 071"  # scripted group (container) (typed FeaturePython)
  n = 2
  ref = O_element
FEATURE [App::DocumentObjectGroupPython] G4_DNA_THYMINE  # scripted group (container) (typed FeaturePython)
  Dunit = g/cm3
  Dvalue = 1
  Group = -> [H_element127,C_element137,N_element057,O_element118]
  conduct = 2
  density = 1
  expand = 3
  formula = G4_DNA_THYMINE
  name = G4_DNA_THYMINE
  specific = 4
FEATURE [App::DocumentObjectGroupPython] H_element128  label="H_element : 075"  # scripted group (container) (typed FeaturePython)
  n = 3
  ref = H_element
FEATURE [App::DocumentObjectGroupPython] C_element138  label="C_element : 083"  # scripted group (container) (typed FeaturePython)
  n = 4
  ref = C_element
FEATURE [App::DocumentObjectGroupPython] N_element058  label="N_element : 030"  # scripted group (container) (typed FeaturePython)
  n = 2
  ref = N_element
FEATURE [App::DocumentObjectGroupPython] O_element119  label="O_element : 072"  # scripted group (container) (typed FeaturePython)
  n = 2
  ref = O_element
FEATURE [App::DocumentObjectGroupPython] G4_DNA_URACIL  # scripted group (container) (typed FeaturePython)
  Dunit = g/cm3
  Dvalue = 1
  Group = -> [H_element128,C_element138,N_element058,O_element119]
  conduct = 2
  density = 1
  expand = 3
  formula = G4_DNA_URACIL
  name = G4_DNA_URACIL
  specific = 4
FEATURE [App::DocumentObjectGroupPython] H_element129  label="H_element : 076"  # scripted group (container) (typed FeaturePython)
  n = 10
  ref = H_element
FEATURE [App::DocumentObjectGroupPython] C_element139  label="C_element : 084"  # scripted group (container) (typed FeaturePython)
  n = 10
  ref = C_element
FEATURE [App::DocumentObjectGroupPython] N_element059  label="N_element : 031"  # scripted group (container) (typed FeaturePython)
  n = 5
  ref = N_element
FEATURE [App::DocumentObjectGroupPython] O_element120  label="O_element : 073"  # scripted group (container) (typed FeaturePython)
  n = 4
  ref = O_element
FEATURE [App::DocumentObjectGroupPython] G4_DNA_ADENOSINE  # scripted group (container) (typed FeaturePython)
  Dunit = g/cm3
  Dvalue = 1
  Group = -> [H_element129,C_element139,N_element059,O_element120]
  conduct = 2
  density = 1
  expand = 3
  formula = G4_DNA_ADENOSINE
  name = G4_DNA_ADENOSINE
  specific = 4
FEATURE [App::DocumentObjectGroupPython] H_element130  label="H_element : 077"  # scripted group (container) (typed FeaturePython)
  n = 10
  ref = H_element
FEATURE [App::DocumentObjectGroupPython] C_element140  label="C_element : 085"  # scripted group (container) (typed FeaturePython)
  n = 10
  ref = C_element
FEATURE [App::DocumentObjectGroupPython] N_element060  label="N_element : 032"  # scripted group (container) (typed FeaturePython)
  n = 5
  ref = N_element
FEATURE [App::DocumentObjectGroupPython] O_element121  label="O_element : 074"  # scripted group (container) (typed FeaturePython)
  n = 5
  ref = O_element
FEATURE [App::DocumentObjectGroupPython] G4_DNA_GUANOSINE  # scripted group (container) (typed FeaturePython)
  Dunit = g/cm3
  Dvalue = 1
  Group = -> [H_element130,C_element140,N_element060,O_element121]
  conduct = 2
  density = 1
  expand = 3
  formula = G4_DNA_GUANOSINE
  name = G4_DNA_GUANOSINE
  specific = 4
FEATURE [App::DocumentObjectGroupPython] H_element131  label="H_element : 078"  # scripted group (container) (typed FeaturePython)
  n = 10
  ref = H_element
FEATURE [App::DocumentObjectGroupPython] C_element141  label="C_element : 086"  # scripted group (container) (typed FeaturePython)
  n = 9
  ref = C_element
FEATURE [App::DocumentObjectGroupPython] N_element061  label="N_element : 033"  # scripted group (container) (typed FeaturePython)
  n = 3
  ref = N_element
FEATURE [App::DocumentObjectGroupPython] O_element122  label="O_element : 075"  # scripted group (container) (typed FeaturePython)
  n = 5
  ref = O_element
FEATURE [App::DocumentObjectGroupPython] G4_DNA_CYTIDINE  # scripted group (container) (typed FeaturePython)
  Dunit = g/cm3
  Dvalue = 1
  Group = -> [H_element131,C_element141,N_element061,O_element122]
  conduct = 2
  density = 1
  expand = 3
  formula = G4_DNA_CYTIDINE
  name = G4_DNA_CYTIDINE
  specific = 4
FEATURE [App::DocumentObjectGroupPython] H_element132  label="H_element : 079"  # scripted group (container) (typed FeaturePython)
  n = 9
  ref = H_element
FEATURE [App::DocumentObjectGroupPython] C_element142  label="C_element : 087"  # scripted group (container) (typed FeaturePython)
  n = 9
  ref = C_element
FEATURE [App::DocumentObjectGroupPython] N_element062  label="N_element : 034"  # scripted group (container) (typed FeaturePython)
  n = 2
  ref = N_element
FEATURE [App::DocumentObjectGroupPython] O_element123  label="O_element : 076"  # scripted group (container) (typed FeaturePython)
  n = 6
  ref = O_element
FEATURE [App::DocumentObjectGroupPython] G4_DNA_URIDINE  # scripted group (container) (typed FeaturePython)
  Dunit = g/cm3
  Dvalue = 1
  Group = -> [H_element132,C_element142,N_element062,O_element123]
  conduct = 2
  density = 1
  expand = 3
  formula = G4_DNA_URIDINE
  name = G4_DNA_URIDINE
  specific = 4
FEATURE [App::DocumentObjectGroupPython] H_element133  label="H_element : 080"  # scripted group (container) (typed FeaturePython)
  n = 11
  ref = H_element
FEATURE [App::DocumentObjectGroupPython] C_element143  label="C_element : 088"  # scripted group (container) (typed FeaturePython)
  n = 10
  ref = C_element
FEATURE [App::DocumentObjectGroupPython] N_element063  label="N_element : 035"  # scripted group (container) (typed FeaturePython)
  n = 2
  ref = N_element
FEATURE [App::DocumentObjectGroupPython] O_element124  label="O_element : 077"  # scripted group (container) (typed FeaturePython)
  n = 6
  ref = O_element
FEATURE [App::DocumentObjectGroupPython] G4_DNA_METHYLURIDINE  # scripted group (container) (typed FeaturePython)
  Dunit = g/cm3
  Dvalue = 1
  Group = -> [H_element133,C_element143,N_element063,O_element124]
  conduct = 2
  density = 1
  expand = 3
  formula = G4_DNA_METHYLURIDINE
  name = G4_DNA_METHYLURIDINE
  specific = 4
FEATURE [App::DocumentObjectGroupPython] P_element014  label="P_element : 003"  # scripted group (container) (typed FeaturePython)
  n = 1
  ref = P_element
FEATURE [App::DocumentObjectGroupPython] O_element125  label="O_element : 078"  # scripted group (container) (typed FeaturePython)
  n = 3
  ref = O_element
FEATURE [App::DocumentObjectGroupPython] G4_DNA_MONOPHOSPHATE  # scripted group (container) (typed FeaturePython)
  Dunit = g/cm3
  Dvalue = 1
  Group = -> [P_element014,O_element125]
  conduct = 2
  density = 1
  expand = 3
  formula = G4_DNA_MONOPHOSPHATE
  name = G4_DNA_MONOPHOSPHATE
  specific = 4
FEATURE [App::DocumentObjectGroupPython] H_element134  label="H_element : 081"  # scripted group (container) (typed FeaturePython)
  n = 10
  ref = H_element
FEATURE [App::DocumentObjectGroupPython] C_element144  label="C_element : 089"  # scripted group (container) (typed FeaturePython)
  n = 10
  ref = C_element
FEATURE [App::DocumentObjectGroupPython] N_element064  label="N_element : 036"  # scripted group (container) (typed FeaturePython)
  n = 5
  ref = N_element
FEATURE [App::DocumentObjectGroupPython] O_element126  label="O_element : 079"  # scripted group (container) (typed FeaturePython)
  n = 7
  ref = O_element
FEATURE [App::DocumentObjectGroupPython] P_element015  label="P_element : 004"  # scripted group (container) (typed FeaturePython)
  n = 1
  ref = P_element
FEATURE [App::DocumentObjectGroupPython] G4_DNA_A  # scripted group (container) (typed FeaturePython)
  Dunit = g/cm3
  Dvalue = 1
  Group = -> [H_element134,C_element144,N_element064,O_element126,P_element015]
  conduct = 2
  density = 1
  expand = 3
  formula = G4_DNA_A
  name = G4_DNA_A
  specific = 4
FEATURE [App::DocumentObjectGroupPython] H_element135  label="H_element : 082"  # scripted group (container) (typed FeaturePython)
  n = 10
  ref = H_element
FEATURE [App::DocumentObjectGroupPython] C_element145  label="C_element : 090"  # scripted group (container) (typed FeaturePython)
  n = 10
  ref = C_element
FEATURE [App::DocumentObjectGroupPython] N_element065  label="N_element : 037"  # scripted group (container) (typed FeaturePython)
  n = 5
  ref = N_element
FEATURE [App::DocumentObjectGroupPython] O_element127  label="O_element : 8"  # scripted group (container) (typed FeaturePython)
  n = 8
  ref = O_element
FEATURE [App::DocumentObjectGroupPython] P_element016  label="P_element : 005"  # scripted group (container) (typed FeaturePython)
  n = 1
  ref = P_element
FEATURE [App::DocumentObjectGroupPython] G4_DNA_G  # scripted group (container) (typed FeaturePython)
  Dunit = g/cm3
  Dvalue = 1
  Group = -> [H_element135,C_element145,N_element065,O_element127,P_element016]
  conduct = 2
  density = 1
  expand = 3
  formula = G4_DNA_G
  name = G4_DNA_G
  specific = 4
FEATURE [App::DocumentObjectGroupPython] H_element136  label="H_element : 083"  # scripted group (container) (typed FeaturePython)
  n = 10
  ref = H_element
FEATURE [App::DocumentObjectGroupPython] C_element146  label="C_element : 091"  # scripted group (container) (typed FeaturePython)
  n = 9
  ref = C_element
FEATURE [App::DocumentObjectGroupPython] N_element066  label="N_element : 038"  # scripted group (container) (typed FeaturePython)
  n = 3
  ref = N_element
FEATURE [App::DocumentObjectGroupPython] O_element128  label="O_element : 080"  # scripted group (container) (typed FeaturePython)
  n = 8
  ref = O_element
FEATURE [App::DocumentObjectGroupPython] P_element017  label="P_element : 006"  # scripted group (container) (typed FeaturePython)
  n = 1
  ref = P_element
FEATURE [App::DocumentObjectGroupPython] G4_DNA_C  # scripted group (container) (typed FeaturePython)
  Dunit = g/cm3
  Dvalue = 1
  Group = -> [H_element136,C_element146,N_element066,O_element128,P_element017]
  conduct = 2
  density = 1
  expand = 3
  formula = G4_DNA_C
  name = G4_DNA_C
  specific = 4
FEATURE [App::DocumentObjectGroupPython] H_element137  label="H_element : 084"  # scripted group (container) (typed FeaturePython)
  n = 9
  ref = H_element
FEATURE [App::DocumentObjectGroupPython] C_element147  label="C_element : 092"  # scripted group (container) (typed FeaturePython)
  n = 9
  ref = C_element
FEATURE [App::DocumentObjectGroupPython] N_element067  label="N_element : 039"  # scripted group (container) (typed FeaturePython)
  n = 2
  ref = N_element
FEATURE [App::DocumentObjectGroupPython] O_element129  label="O_element : 9"  # scripted group (container) (typed FeaturePython)
  n = 9
  ref = O_element
FEATURE [App::DocumentObjectGroupPython] P_element018  label="P_element : 007"  # scripted group (container) (typed FeaturePython)
  n = 1
  ref = P_element
FEATURE [App::DocumentObjectGroupPython] G4_DNA_U  # scripted group (container) (typed FeaturePython)
  Dunit = g/cm3
  Dvalue = 1
  Group = -> [H_element137,C_element147,N_element067,O_element129,P_element018]
  conduct = 2
  density = 1
  expand = 3
  formula = G4_DNA_U
  name = G4_DNA_U
  specific = 4
FEATURE [App::DocumentObjectGroupPython] H_element138  label="H_element : 085"  # scripted group (container) (typed FeaturePython)
  n = 11
  ref = H_element
FEATURE [App::DocumentObjectGroupPython] C_element148  label="C_element : 093"  # scripted group (container) (typed FeaturePython)
  n = 10
  ref = C_element
FEATURE [App::DocumentObjectGroupPython] N_element068  label="N_element : 040"  # scripted group (container) (typed FeaturePython)
  n = 2
  ref = N_element
FEATURE [App::DocumentObjectGroupPython] O_element130  label="O_element : 081"  # scripted group (container) (typed FeaturePython)
  n = 9
  ref = O_element
FEATURE [App::DocumentObjectGroupPython] P_element019  label="P_element : 008"  # scripted group (container) (typed FeaturePython)
  n = 1
  ref = P_element
FEATURE [App::DocumentObjectGroupPython] G4_DNA_MU  # scripted group (container) (typed FeaturePython)
  Dunit = g/cm3
  Dvalue = 1
  Group = -> [H_element138,C_element148,N_element068,O_element130,P_element019]
  conduct = 2
  density = 1
  expand = 3
  formula = G4_DNA_MU
  name = G4_DNA_MU
  specific = 4
FEATURE [App::DocumentObjectGroupPython] BioChemical  # scripted group (container) (typed FeaturePython)
  Group = -> [G4_CYTOSINE,G4_THYMINE,G4_URACIL,G4_DNA_ADENINE,G4_DNA_GUANINE,G4_DNA_CYTOSINE,G4_DNA_THYMINE,G4_DNA_URACIL,G4_DNA_ADENOSINE,G4_DNA_GUANOSINE,G4_DNA_CYTIDINE,G4_DNA_URIDINE,G4_DNA_METHYLURIDINE,G4_DNA_MONOPHOSPHATE,G4_DNA_A,G4_DNA_G,G4_DNA_C,G4_DNA_U,G4_DNA_MU]
FEATURE [App::DocumentObjectGroupPython] G4Materials  # scripted group (container) (typed FeaturePython)
  Group = -> [NIST,Element,HEP,Space,BioChemical]
  version = 1
FEATURE [App::DocumentObjectGroupPython] Geant4  # scripted group (container) (typed FeaturePython)
  Group = -> [G4Isotopes,G4Elements,G4Materials]
FEATURE [App::DocumentObjectGroupPython] Materials  # scripted group (container) (typed FeaturePython)
  Group = -> [Geant4]
FEATURE [Part::FeaturePython] GDMLBox_WorldBox  # WARN: FeaturePython — macro-defined, semantics opaque (R4)
  lunit = 2
  material = 5
  x = 200
  y = 200
  z = 200
FEATURE [Part::FeaturePython] GDMLSphere_Sphere  # WARN: FeaturePython — macro-defined, semantics opaque (R4)
  Placement = pos=(20,0,0) rot=(0,0,1;0rad)
  aunit = 0
  deltaphi = 2.02
  deltatheta = 2.02
  lunit = 2
  material = 18
  rmax = 20
  rmin = 10
  startphi = 0
  starttheta = 0
FEATURE [Part::FeaturePython] GDMLTorus_Torus  # WARN: FeaturePython — macro-defined, semantics opaque (R4)
  aunit = deg
  deltaphi = 360
  lunit = 2
  material = 5
  rmax = 5
  rmin = 0
  rtor = 10
  startphi = 10
FEATURE [Part::MultiFuse] Fusion
  Shapes = -> [GDMLSphere_Sphere,GDMLTorus_Torus]
  material = 18
FEATURE [Part::FeaturePython] Array  # Draft array (typed FeaturePython)
  Angle = 360
  ArrayType = 0
  Axis = (0,0,1)
  Base = -> Fusion
  Center = (0,0,0)
  Fuse = false
  IntervalAxis = (0,0,0)
  IntervalX = (100,0,0)
  IntervalY = (0,100,0)
  IntervalZ = (0,0,100)
  NumberCircles = 3
  NumberPolar = 5
  NumberX = 2
  NumberY = 2
  NumberZ = 1
  Placement = pos=(-51,-45,0) rot=(0,0,1;0rad)
  RadialDistance = 50
  Symmetry = 1
  TangentialDistance = 25
  material = 261
FEATURE [App::Part] Part
  Group = -> [GDMLSphere_Sphere,GDMLTorus_Torus,Fusion,Array]
  Origin = -> Origin001
FEATURE [App::Part] worldVOL
  Group = -> [GDMLBox_WorldBox,Part]
  Origin = -> Origin
